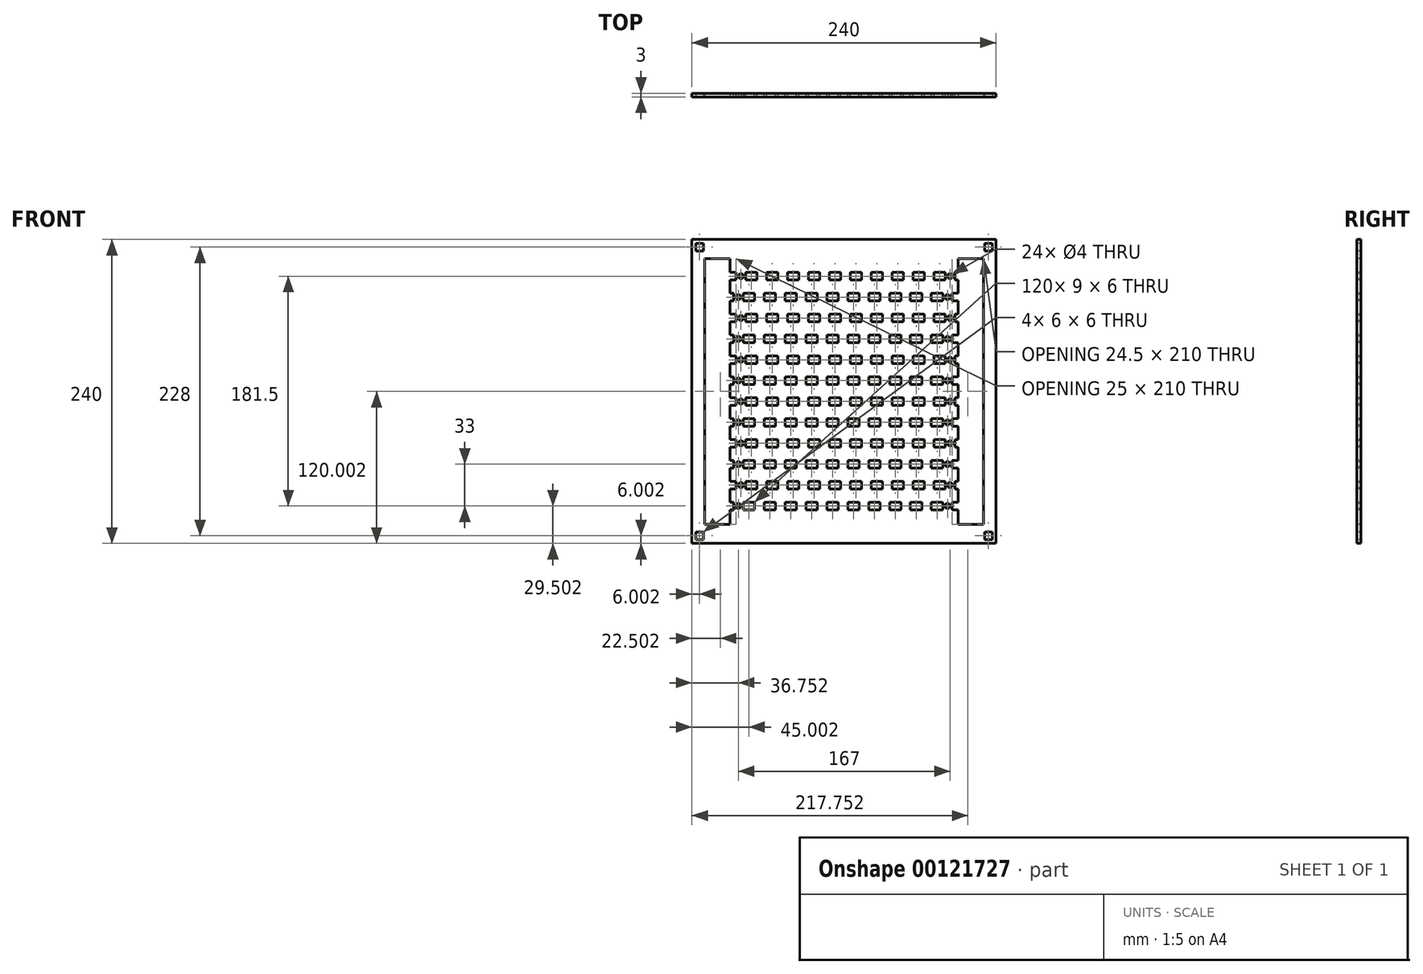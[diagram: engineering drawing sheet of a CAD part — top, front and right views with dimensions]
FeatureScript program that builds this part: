
annotation { "Feature Type Name" : "Feature", "Feature Type Description" : "" }
export const myFeature = defineFeature(function(context is Context, id is Id, definition is map)
    precondition{}
    {
        {
            var Q0;
            Q0=qCreatedBy(makeId("Front.planeOp"),FACE);
            var sketch = newSketch(context, id + "F0", { "sketchPlane" : qUnion([Q0])});
            skLineSegment(sketch, "E0.bottom", {"start": v(-121.79, 157.74) * mm, "end": v(118.21, 157.74) * mm});
            skLineSegment(sketch, "E0.top", {"start": v(-121.79, -82.26) * mm, "end": v(118.21, -82.26) * mm});
            skLineSegment(sketch, "E0.left", {"start": v(-121.79, 157.74) * mm, "end": v(-121.79, -82.26) * mm});
            skLineSegment(sketch, "E0.right", {"start": v(118.21, 157.74) * mm, "end": v(118.21, -82.26) * mm});
            skLineSegment(sketch, "E1.bottom", {"start": v(-95.79, 131.74) * mm, "end": v(-86.79, 131.74) * mm});
            skLineSegment(sketch, "E1.top", {"start": v(-95.79, 125.74) * mm, "end": v(-86.79, 125.74) * mm});
            skLineSegment(sketch, "E1.left", {"start": v(-95.79, 131.74) * mm, "end": v(-95.79, 125.74) * mm});
            skLineSegment(sketch, "E1.right", {"start": v(-86.79, 131.74) * mm, "end": v(-86.79, 125.74) * mm});
            skLineSegment(sketch, "E2.direction1", {"start": v(-95.79, 125.74) * mm, "end": v(-85.79, 125.74) * mm, "construction": true});
            skLineSegment(sketch, "E3.direction1", {"start": v(-95.79, 125.74) * mm, "end": v(-79.29, 125.74) * mm, "construction": true});
            skLineSegment(sketch, "E3.direction2", {"start": v(-95.79, 125.74) * mm, "end": v(-95.79, 92.74) * mm, "construction": true});
            skLineSegment(sketch, "E4.0.1.0", {"start": v(-79.29, 125.74) * mm, "end": v(-69.29, 125.74) * mm, "construction": true});
            skLineSegment(sketch, "E4.3.1.0", {"start": v(-70.29, 131.74) * mm, "end": v(-70.29, 125.74) * mm});
            skLineSegment(sketch, "E4.6.1.0", {"start": v(-79.29, 131.74) * mm, "end": v(-79.29, 125.74) * mm});
            skLineSegment(sketch, "E4.9.1.0", {"start": v(-79.29, 131.74) * mm, "end": v(-70.29, 131.74) * mm});
            skLineSegment(sketch, "E4.12.1.0", {"start": v(-79.29, 125.74) * mm, "end": v(-70.29, 125.74) * mm});
            skLineSegment(sketch, "E4.0.2.0", {"start": v(-62.79, 125.74) * mm, "end": v(-52.79, 125.74) * mm, "construction": true});
            skLineSegment(sketch, "E4.3.2.0", {"start": v(-53.79, 131.74) * mm, "end": v(-53.79, 125.74) * mm});
            skLineSegment(sketch, "E4.6.2.0", {"start": v(-62.79, 131.74) * mm, "end": v(-62.79, 125.74) * mm});
            skLineSegment(sketch, "E4.9.2.0", {"start": v(-62.79, 131.74) * mm, "end": v(-53.79, 131.74) * mm});
            skLineSegment(sketch, "E4.12.2.0", {"start": v(-62.79, 125.74) * mm, "end": v(-53.79, 125.74) * mm});
            skLineSegment(sketch, "E4.0.3.0", {"start": v(-46.29, 125.74) * mm, "end": v(-36.29, 125.74) * mm, "construction": true});
            skLineSegment(sketch, "E4.3.3.0", {"start": v(-37.29, 131.74) * mm, "end": v(-37.29, 125.74) * mm});
            skLineSegment(sketch, "E4.6.3.0", {"start": v(-46.29, 131.74) * mm, "end": v(-46.29, 125.74) * mm});
            skLineSegment(sketch, "E4.9.3.0", {"start": v(-46.29, 131.74) * mm, "end": v(-37.29, 131.74) * mm});
            skLineSegment(sketch, "E4.12.3.0", {"start": v(-46.29, 125.74) * mm, "end": v(-37.29, 125.74) * mm});
            skLineSegment(sketch, "E4.0.4.0", {"start": v(-29.79, 125.74) * mm, "end": v(-19.79, 125.74) * mm, "construction": true});
            skLineSegment(sketch, "E4.3.4.0", {"start": v(-20.79, 131.74) * mm, "end": v(-20.79, 125.74) * mm});
            skLineSegment(sketch, "E4.6.4.0", {"start": v(-29.79, 131.74) * mm, "end": v(-29.79, 125.74) * mm});
            skLineSegment(sketch, "E4.9.4.0", {"start": v(-29.79, 131.74) * mm, "end": v(-20.79, 131.74) * mm});
            skLineSegment(sketch, "E4.12.4.0", {"start": v(-29.79, 125.74) * mm, "end": v(-20.79, 125.74) * mm});
            skLineSegment(sketch, "E4.0.5.0", {"start": v(-13.29, 125.74) * mm, "end": v(-3.29, 125.74) * mm, "construction": true});
            skLineSegment(sketch, "E4.3.5.0", {"start": v(-4.29, 131.74) * mm, "end": v(-4.29, 125.74) * mm});
            skLineSegment(sketch, "E4.6.5.0", {"start": v(-13.29, 131.74) * mm, "end": v(-13.29, 125.74) * mm});
            skLineSegment(sketch, "E4.9.5.0", {"start": v(-13.29, 131.74) * mm, "end": v(-4.29, 131.74) * mm});
            skLineSegment(sketch, "E4.12.5.0", {"start": v(-13.29, 125.74) * mm, "end": v(-4.29, 125.74) * mm});
            skLineSegment(sketch, "E4.0.6.0", {"start": v(3.21, 125.74) * mm, "end": v(13.21, 125.74) * mm, "construction": true});
            skLineSegment(sketch, "E4.3.6.0", {"start": v(12.21, 131.74) * mm, "end": v(12.21, 125.74) * mm});
            skLineSegment(sketch, "E4.6.6.0", {"start": v(3.21, 131.74) * mm, "end": v(3.21, 125.74) * mm});
            skLineSegment(sketch, "E4.9.6.0", {"start": v(3.21, 131.74) * mm, "end": v(12.21, 131.74) * mm});
            skLineSegment(sketch, "E4.12.6.0", {"start": v(3.21, 125.74) * mm, "end": v(12.21, 125.74) * mm});
            skLineSegment(sketch, "E4.0.7.0", {"start": v(19.71, 125.74) * mm, "end": v(29.71, 125.74) * mm, "construction": true});
            skLineSegment(sketch, "E4.3.7.0", {"start": v(28.71, 131.74) * mm, "end": v(28.71, 125.74) * mm});
            skLineSegment(sketch, "E4.6.7.0", {"start": v(19.71, 131.74) * mm, "end": v(19.71, 125.74) * mm});
            skLineSegment(sketch, "E4.9.7.0", {"start": v(19.71, 131.74) * mm, "end": v(28.71, 131.74) * mm});
            skLineSegment(sketch, "E4.12.7.0", {"start": v(19.71, 125.74) * mm, "end": v(28.71, 125.74) * mm});
            skLineSegment(sketch, "E4.0.8.0", {"start": v(36.21, 125.74) * mm, "end": v(46.21, 125.74) * mm, "construction": true});
            skLineSegment(sketch, "E4.3.8.0", {"start": v(45.21, 131.74) * mm, "end": v(45.21, 125.74) * mm});
            skLineSegment(sketch, "E4.6.8.0", {"start": v(36.21, 131.74) * mm, "end": v(36.21, 125.74) * mm});
            skLineSegment(sketch, "E4.9.8.0", {"start": v(36.21, 131.74) * mm, "end": v(45.21, 131.74) * mm});
            skLineSegment(sketch, "E4.12.8.0", {"start": v(36.21, 125.74) * mm, "end": v(45.21, 125.74) * mm});
            skLineSegment(sketch, "E4.0.9.0", {"start": v(52.71, 125.74) * mm, "end": v(62.71, 125.74) * mm, "construction": true});
            skLineSegment(sketch, "E4.3.9.0", {"start": v(61.71, 131.74) * mm, "end": v(61.71, 125.74) * mm});
            skLineSegment(sketch, "E4.6.9.0", {"start": v(52.71, 131.74) * mm, "end": v(52.71, 125.74) * mm});
            skLineSegment(sketch, "E4.9.9.0", {"start": v(52.71, 131.74) * mm, "end": v(61.71, 131.74) * mm});
            skLineSegment(sketch, "E4.12.9.0", {"start": v(52.71, 125.74) * mm, "end": v(61.71, 125.74) * mm});
            skLineSegment(sketch, "E4.0.10.0", {"start": v(69.21, 125.74) * mm, "end": v(79.21, 125.74) * mm, "construction": true});
            skLineSegment(sketch, "E4.3.10.0", {"start": v(78.21, 131.74) * mm, "end": v(78.21, 125.74) * mm});
            skLineSegment(sketch, "E4.6.10.0", {"start": v(69.21, 131.74) * mm, "end": v(69.21, 125.74) * mm});
            skLineSegment(sketch, "E4.9.10.0", {"start": v(69.21, 131.74) * mm, "end": v(78.21, 131.74) * mm});
            skLineSegment(sketch, "E4.12.10.0", {"start": v(69.21, 125.74) * mm, "end": v(78.21, 125.74) * mm});
            skLineSegment(sketch, "E4.0.11.0", {"start": v(85.71, 125.74) * mm, "end": v(95.71, 125.74) * mm, "construction": true});
            skLineSegment(sketch, "E4.3.11.0", {"start": v(94.71, 131.74) * mm, "end": v(94.71, 125.74) * mm});
            skLineSegment(sketch, "E4.6.11.0", {"start": v(85.71, 131.74) * mm, "end": v(85.71, 125.74) * mm});
            skLineSegment(sketch, "E4.9.11.0", {"start": v(85.71, 131.74) * mm, "end": v(94.71, 131.74) * mm});
            skLineSegment(sketch, "E4.12.11.0", {"start": v(85.71, 125.74) * mm, "end": v(94.71, 125.74) * mm});
            skLineSegment(sketch, "E5.0.0.1", {"start": v(-95.79, 92.74) * mm, "end": v(-85.79, 92.74) * mm, "construction": true});
            skLineSegment(sketch, "E5.3.0.1", {"start": v(-86.79, 98.74) * mm, "end": v(-86.79, 92.74) * mm});
            skLineSegment(sketch, "E5.6.0.1", {"start": v(-95.79, 98.74) * mm, "end": v(-95.79, 92.74) * mm});
            skLineSegment(sketch, "E5.9.0.1", {"start": v(-95.79, 98.74) * mm, "end": v(-86.79, 98.74) * mm});
            skLineSegment(sketch, "E5.12.0.1", {"start": v(-95.79, 92.74) * mm, "end": v(-86.79, 92.74) * mm});
            skLineSegment(sketch, "E5.0.0.2", {"start": v(-95.79, 59.74) * mm, "end": v(-85.79, 59.74) * mm, "construction": true});
            skLineSegment(sketch, "E5.3.0.2", {"start": v(-86.79, 65.74) * mm, "end": v(-86.79, 59.74) * mm});
            skLineSegment(sketch, "E5.6.0.2", {"start": v(-95.79, 65.74) * mm, "end": v(-95.79, 59.74) * mm});
            skLineSegment(sketch, "E5.9.0.2", {"start": v(-95.79, 65.74) * mm, "end": v(-86.79, 65.74) * mm});
            skLineSegment(sketch, "E5.12.0.2", {"start": v(-95.79, 59.74) * mm, "end": v(-86.79, 59.74) * mm});
            skLineSegment(sketch, "E5.0.0.3", {"start": v(-95.79, 26.74) * mm, "end": v(-85.79, 26.74) * mm, "construction": true});
            skLineSegment(sketch, "E5.3.0.3", {"start": v(-86.79, 32.74) * mm, "end": v(-86.79, 26.74) * mm});
            skLineSegment(sketch, "E5.6.0.3", {"start": v(-95.79, 32.74) * mm, "end": v(-95.79, 26.74) * mm});
            skLineSegment(sketch, "E5.9.0.3", {"start": v(-95.79, 32.74) * mm, "end": v(-86.79, 32.74) * mm});
            skLineSegment(sketch, "E5.12.0.3", {"start": v(-95.79, 26.74) * mm, "end": v(-86.79, 26.74) * mm});
            skLineSegment(sketch, "E5.0.0.4", {"start": v(-95.79, -6.26) * mm, "end": v(-85.79, -6.26) * mm, "construction": true});
            skLineSegment(sketch, "E5.3.0.4", {"start": v(-86.79, -0.26) * mm, "end": v(-86.79, -6.26) * mm});
            skLineSegment(sketch, "E5.6.0.4", {"start": v(-95.79, -0.26) * mm, "end": v(-95.79, -6.26) * mm});
            skLineSegment(sketch, "E5.9.0.4", {"start": v(-95.79, -0.26) * mm, "end": v(-86.79, -0.26) * mm});
            skLineSegment(sketch, "E5.12.0.4", {"start": v(-95.79, -6.26) * mm, "end": v(-86.79, -6.26) * mm});
            skLineSegment(sketch, "E5.0.0.5", {"start": v(-95.79, -39.26) * mm, "end": v(-85.79, -39.26) * mm, "construction": true});
            skLineSegment(sketch, "E5.3.0.5", {"start": v(-86.79, -33.26) * mm, "end": v(-86.79, -39.26) * mm});
            skLineSegment(sketch, "E5.6.0.5", {"start": v(-95.79, -33.26) * mm, "end": v(-95.79, -39.26) * mm});
            skLineSegment(sketch, "E5.9.0.5", {"start": v(-95.79, -33.26) * mm, "end": v(-86.79, -33.26) * mm});
            skLineSegment(sketch, "E5.12.0.5", {"start": v(-95.79, -39.26) * mm, "end": v(-86.79, -39.26) * mm});
            skLineSegment(sketch, "E5.0.1.1", {"start": v(-79.29, 92.74) * mm, "end": v(-69.29, 92.74) * mm, "construction": true});
            skLineSegment(sketch, "E5.3.1.1", {"start": v(-70.29, 98.74) * mm, "end": v(-70.29, 92.74) * mm});
            skLineSegment(sketch, "E5.6.1.1", {"start": v(-79.29, 98.74) * mm, "end": v(-79.29, 92.74) * mm});
            skLineSegment(sketch, "E5.9.1.1", {"start": v(-79.29, 98.74) * mm, "end": v(-70.29, 98.74) * mm});
            skLineSegment(sketch, "E5.12.1.1", {"start": v(-79.29, 92.74) * mm, "end": v(-70.29, 92.74) * mm});
            skLineSegment(sketch, "E5.0.1.2", {"start": v(-79.29, 59.74) * mm, "end": v(-69.29, 59.74) * mm, "construction": true});
            skLineSegment(sketch, "E5.3.1.2", {"start": v(-70.29, 65.74) * mm, "end": v(-70.29, 59.74) * mm});
            skLineSegment(sketch, "E5.6.1.2", {"start": v(-79.29, 65.74) * mm, "end": v(-79.29, 59.74) * mm});
            skLineSegment(sketch, "E5.9.1.2", {"start": v(-79.29, 65.74) * mm, "end": v(-70.29, 65.74) * mm});
            skLineSegment(sketch, "E5.12.1.2", {"start": v(-79.29, 59.74) * mm, "end": v(-70.29, 59.74) * mm});
            skLineSegment(sketch, "E5.0.1.3", {"start": v(-79.29, 26.74) * mm, "end": v(-69.29, 26.74) * mm, "construction": true});
            skLineSegment(sketch, "E5.3.1.3", {"start": v(-70.29, 32.74) * mm, "end": v(-70.29, 26.74) * mm});
            skLineSegment(sketch, "E5.6.1.3", {"start": v(-79.29, 32.74) * mm, "end": v(-79.29, 26.74) * mm});
            skLineSegment(sketch, "E5.9.1.3", {"start": v(-79.29, 32.74) * mm, "end": v(-70.29, 32.74) * mm});
            skLineSegment(sketch, "E5.12.1.3", {"start": v(-79.29, 26.74) * mm, "end": v(-70.29, 26.74) * mm});
            skLineSegment(sketch, "E5.0.1.4", {"start": v(-79.29, -6.26) * mm, "end": v(-69.29, -6.26) * mm, "construction": true});
            skLineSegment(sketch, "E5.3.1.4", {"start": v(-70.29, -0.26) * mm, "end": v(-70.29, -6.26) * mm});
            skLineSegment(sketch, "E5.6.1.4", {"start": v(-79.29, -0.26) * mm, "end": v(-79.29, -6.26) * mm});
            skLineSegment(sketch, "E5.9.1.4", {"start": v(-79.29, -0.26) * mm, "end": v(-70.29, -0.26) * mm});
            skLineSegment(sketch, "E5.12.1.4", {"start": v(-79.29, -6.26) * mm, "end": v(-70.29, -6.26) * mm});
            skLineSegment(sketch, "E5.0.1.5", {"start": v(-79.29, -39.26) * mm, "end": v(-69.29, -39.26) * mm, "construction": true});
            skLineSegment(sketch, "E5.3.1.5", {"start": v(-70.29, -33.26) * mm, "end": v(-70.29, -39.26) * mm});
            skLineSegment(sketch, "E5.6.1.5", {"start": v(-79.29, -33.26) * mm, "end": v(-79.29, -39.26) * mm});
            skLineSegment(sketch, "E5.9.1.5", {"start": v(-79.29, -33.26) * mm, "end": v(-70.29, -33.26) * mm});
            skLineSegment(sketch, "E5.12.1.5", {"start": v(-79.29, -39.26) * mm, "end": v(-70.29, -39.26) * mm});
            skLineSegment(sketch, "E5.0.2.1", {"start": v(-62.79, 92.74) * mm, "end": v(-52.79, 92.74) * mm, "construction": true});
            skLineSegment(sketch, "E5.3.2.1", {"start": v(-53.79, 98.74) * mm, "end": v(-53.79, 92.74) * mm});
            skLineSegment(sketch, "E5.6.2.1", {"start": v(-62.79, 98.74) * mm, "end": v(-62.79, 92.74) * mm});
            skLineSegment(sketch, "E5.9.2.1", {"start": v(-62.79, 98.74) * mm, "end": v(-53.79, 98.74) * mm});
            skLineSegment(sketch, "E5.12.2.1", {"start": v(-62.79, 92.74) * mm, "end": v(-53.79, 92.74) * mm});
            skLineSegment(sketch, "E5.0.2.2", {"start": v(-62.79, 59.74) * mm, "end": v(-52.79, 59.74) * mm, "construction": true});
            skLineSegment(sketch, "E5.3.2.2", {"start": v(-53.79, 65.74) * mm, "end": v(-53.79, 59.74) * mm});
            skLineSegment(sketch, "E5.6.2.2", {"start": v(-62.79, 65.74) * mm, "end": v(-62.79, 59.74) * mm});
            skLineSegment(sketch, "E5.9.2.2", {"start": v(-62.79, 65.74) * mm, "end": v(-53.79, 65.74) * mm});
            skLineSegment(sketch, "E5.12.2.2", {"start": v(-62.79, 59.74) * mm, "end": v(-53.79, 59.74) * mm});
            skLineSegment(sketch, "E5.0.2.3", {"start": v(-62.79, 26.74) * mm, "end": v(-52.79, 26.74) * mm, "construction": true});
            skLineSegment(sketch, "E5.3.2.3", {"start": v(-53.79, 32.74) * mm, "end": v(-53.79, 26.74) * mm});
            skLineSegment(sketch, "E5.6.2.3", {"start": v(-62.79, 32.74) * mm, "end": v(-62.79, 26.74) * mm});
            skLineSegment(sketch, "E5.9.2.3", {"start": v(-62.79, 32.74) * mm, "end": v(-53.79, 32.74) * mm});
            skLineSegment(sketch, "E5.12.2.3", {"start": v(-62.79, 26.74) * mm, "end": v(-53.79, 26.74) * mm});
            skLineSegment(sketch, "E5.0.2.4", {"start": v(-62.79, -6.26) * mm, "end": v(-52.79, -6.26) * mm, "construction": true});
            skLineSegment(sketch, "E5.3.2.4", {"start": v(-53.79, -0.26) * mm, "end": v(-53.79, -6.26) * mm});
            skLineSegment(sketch, "E5.6.2.4", {"start": v(-62.79, -0.26) * mm, "end": v(-62.79, -6.26) * mm});
            skLineSegment(sketch, "E5.9.2.4", {"start": v(-62.79, -0.26) * mm, "end": v(-53.79, -0.26) * mm});
            skLineSegment(sketch, "E5.12.2.4", {"start": v(-62.79, -6.26) * mm, "end": v(-53.79, -6.26) * mm});
            skLineSegment(sketch, "E5.0.2.5", {"start": v(-62.79, -39.26) * mm, "end": v(-52.79, -39.26) * mm, "construction": true});
            skLineSegment(sketch, "E5.3.2.5", {"start": v(-53.79, -33.26) * mm, "end": v(-53.79, -39.26) * mm});
            skLineSegment(sketch, "E5.6.2.5", {"start": v(-62.79, -33.26) * mm, "end": v(-62.79, -39.26) * mm});
            skLineSegment(sketch, "E5.9.2.5", {"start": v(-62.79, -33.26) * mm, "end": v(-53.79, -33.26) * mm});
            skLineSegment(sketch, "E5.12.2.5", {"start": v(-62.79, -39.26) * mm, "end": v(-53.79, -39.26) * mm});
            skLineSegment(sketch, "E5.0.3.1", {"start": v(-46.29, 92.74) * mm, "end": v(-36.29, 92.74) * mm, "construction": true});
            skLineSegment(sketch, "E5.3.3.1", {"start": v(-37.29, 98.74) * mm, "end": v(-37.29, 92.74) * mm});
            skLineSegment(sketch, "E5.6.3.1", {"start": v(-46.29, 98.74) * mm, "end": v(-46.29, 92.74) * mm});
            skLineSegment(sketch, "E5.9.3.1", {"start": v(-46.29, 98.74) * mm, "end": v(-37.29, 98.74) * mm});
            skLineSegment(sketch, "E5.12.3.1", {"start": v(-46.29, 92.74) * mm, "end": v(-37.29, 92.74) * mm});
            skLineSegment(sketch, "E5.0.3.2", {"start": v(-46.29, 59.74) * mm, "end": v(-36.29, 59.74) * mm, "construction": true});
            skLineSegment(sketch, "E5.3.3.2", {"start": v(-37.29, 65.74) * mm, "end": v(-37.29, 59.74) * mm});
            skLineSegment(sketch, "E5.6.3.2", {"start": v(-46.29, 65.74) * mm, "end": v(-46.29, 59.74) * mm});
            skLineSegment(sketch, "E5.9.3.2", {"start": v(-46.29, 65.74) * mm, "end": v(-37.29, 65.74) * mm});
            skLineSegment(sketch, "E5.12.3.2", {"start": v(-46.29, 59.74) * mm, "end": v(-37.29, 59.74) * mm});
            skLineSegment(sketch, "E5.0.3.3", {"start": v(-46.29, 26.74) * mm, "end": v(-36.29, 26.74) * mm, "construction": true});
            skLineSegment(sketch, "E5.3.3.3", {"start": v(-37.29, 32.74) * mm, "end": v(-37.29, 26.74) * mm});
            skLineSegment(sketch, "E5.6.3.3", {"start": v(-46.29, 32.74) * mm, "end": v(-46.29, 26.74) * mm});
            skLineSegment(sketch, "E5.9.3.3", {"start": v(-46.29, 32.74) * mm, "end": v(-37.29, 32.74) * mm});
            skLineSegment(sketch, "E5.12.3.3", {"start": v(-46.29, 26.74) * mm, "end": v(-37.29, 26.74) * mm});
            skLineSegment(sketch, "E5.0.3.4", {"start": v(-46.29, -6.26) * mm, "end": v(-36.29, -6.26) * mm, "construction": true});
            skLineSegment(sketch, "E5.3.3.4", {"start": v(-37.29, -0.26) * mm, "end": v(-37.29, -6.26) * mm});
            skLineSegment(sketch, "E5.6.3.4", {"start": v(-46.29, -0.26) * mm, "end": v(-46.29, -6.26) * mm});
            skLineSegment(sketch, "E5.9.3.4", {"start": v(-46.29, -0.26) * mm, "end": v(-37.29, -0.26) * mm});
            skLineSegment(sketch, "E5.12.3.4", {"start": v(-46.29, -6.26) * mm, "end": v(-37.29, -6.26) * mm});
            skLineSegment(sketch, "E5.0.3.5", {"start": v(-46.29, -39.26) * mm, "end": v(-36.29, -39.26) * mm, "construction": true});
            skLineSegment(sketch, "E5.3.3.5", {"start": v(-37.29, -33.26) * mm, "end": v(-37.29, -39.26) * mm});
            skLineSegment(sketch, "E5.6.3.5", {"start": v(-46.29, -33.26) * mm, "end": v(-46.29, -39.26) * mm});
            skLineSegment(sketch, "E5.9.3.5", {"start": v(-46.29, -33.26) * mm, "end": v(-37.29, -33.26) * mm});
            skLineSegment(sketch, "E5.12.3.5", {"start": v(-46.29, -39.26) * mm, "end": v(-37.29, -39.26) * mm});
            skLineSegment(sketch, "E5.0.4.1", {"start": v(-29.79, 92.74) * mm, "end": v(-19.79, 92.74) * mm, "construction": true});
            skLineSegment(sketch, "E5.3.4.1", {"start": v(-20.79, 98.74) * mm, "end": v(-20.79, 92.74) * mm});
            skLineSegment(sketch, "E5.6.4.1", {"start": v(-29.79, 98.74) * mm, "end": v(-29.79, 92.74) * mm});
            skLineSegment(sketch, "E5.9.4.1", {"start": v(-29.79, 98.74) * mm, "end": v(-20.79, 98.74) * mm});
            skLineSegment(sketch, "E5.12.4.1", {"start": v(-29.79, 92.74) * mm, "end": v(-20.79, 92.74) * mm});
            skLineSegment(sketch, "E5.0.4.2", {"start": v(-29.79, 59.74) * mm, "end": v(-19.79, 59.74) * mm, "construction": true});
            skLineSegment(sketch, "E5.3.4.2", {"start": v(-20.79, 65.74) * mm, "end": v(-20.79, 59.74) * mm});
            skLineSegment(sketch, "E5.6.4.2", {"start": v(-29.79, 65.74) * mm, "end": v(-29.79, 59.74) * mm});
            skLineSegment(sketch, "E5.9.4.2", {"start": v(-29.79, 65.74) * mm, "end": v(-20.79, 65.74) * mm});
            skLineSegment(sketch, "E5.12.4.2", {"start": v(-29.79, 59.74) * mm, "end": v(-20.79, 59.74) * mm});
            skLineSegment(sketch, "E5.0.4.3", {"start": v(-29.79, 26.74) * mm, "end": v(-19.79, 26.74) * mm, "construction": true});
            skLineSegment(sketch, "E5.3.4.3", {"start": v(-20.79, 32.74) * mm, "end": v(-20.79, 26.74) * mm});
            skLineSegment(sketch, "E5.6.4.3", {"start": v(-29.79, 32.74) * mm, "end": v(-29.79, 26.74) * mm});
            skLineSegment(sketch, "E5.9.4.3", {"start": v(-29.79, 32.74) * mm, "end": v(-20.79, 32.74) * mm});
            skLineSegment(sketch, "E5.12.4.3", {"start": v(-29.79, 26.74) * mm, "end": v(-20.79, 26.74) * mm});
            skLineSegment(sketch, "E5.0.4.4", {"start": v(-29.79, -6.26) * mm, "end": v(-19.79, -6.26) * mm, "construction": true});
            skLineSegment(sketch, "E5.3.4.4", {"start": v(-20.79, -0.26) * mm, "end": v(-20.79, -6.26) * mm});
            skLineSegment(sketch, "E5.6.4.4", {"start": v(-29.79, -0.26) * mm, "end": v(-29.79, -6.26) * mm});
            skLineSegment(sketch, "E5.9.4.4", {"start": v(-29.79, -0.26) * mm, "end": v(-20.79, -0.26) * mm});
            skLineSegment(sketch, "E5.12.4.4", {"start": v(-29.79, -6.26) * mm, "end": v(-20.79, -6.26) * mm});
            skLineSegment(sketch, "E5.0.4.5", {"start": v(-29.79, -39.26) * mm, "end": v(-19.79, -39.26) * mm, "construction": true});
            skLineSegment(sketch, "E5.3.4.5", {"start": v(-20.79, -33.26) * mm, "end": v(-20.79, -39.26) * mm});
            skLineSegment(sketch, "E5.6.4.5", {"start": v(-29.79, -33.26) * mm, "end": v(-29.79, -39.26) * mm});
            skLineSegment(sketch, "E5.9.4.5", {"start": v(-29.79, -33.26) * mm, "end": v(-20.79, -33.26) * mm});
            skLineSegment(sketch, "E5.12.4.5", {"start": v(-29.79, -39.26) * mm, "end": v(-20.79, -39.26) * mm});
            skLineSegment(sketch, "E5.0.5.1", {"start": v(-13.29, 92.74) * mm, "end": v(-3.29, 92.74) * mm, "construction": true});
            skLineSegment(sketch, "E5.3.5.1", {"start": v(-4.29, 98.74) * mm, "end": v(-4.29, 92.74) * mm});
            skLineSegment(sketch, "E5.6.5.1", {"start": v(-13.29, 98.74) * mm, "end": v(-13.29, 92.74) * mm});
            skLineSegment(sketch, "E5.9.5.1", {"start": v(-13.29, 98.74) * mm, "end": v(-4.29, 98.74) * mm});
            skLineSegment(sketch, "E5.12.5.1", {"start": v(-13.29, 92.74) * mm, "end": v(-4.29, 92.74) * mm});
            skLineSegment(sketch, "E5.0.5.2", {"start": v(-13.29, 59.74) * mm, "end": v(-3.29, 59.74) * mm, "construction": true});
            skLineSegment(sketch, "E5.3.5.2", {"start": v(-4.29, 65.74) * mm, "end": v(-4.29, 59.74) * mm});
            skLineSegment(sketch, "E5.6.5.2", {"start": v(-13.29, 65.74) * mm, "end": v(-13.29, 59.74) * mm});
            skLineSegment(sketch, "E5.9.5.2", {"start": v(-13.29, 65.74) * mm, "end": v(-4.29, 65.74) * mm});
            skLineSegment(sketch, "E5.12.5.2", {"start": v(-13.29, 59.74) * mm, "end": v(-4.29, 59.74) * mm});
            skLineSegment(sketch, "E5.0.5.3", {"start": v(-13.29, 26.74) * mm, "end": v(-3.29, 26.74) * mm, "construction": true});
            skLineSegment(sketch, "E5.3.5.3", {"start": v(-4.29, 32.74) * mm, "end": v(-4.29, 26.74) * mm});
            skLineSegment(sketch, "E5.6.5.3", {"start": v(-13.29, 32.74) * mm, "end": v(-13.29, 26.74) * mm});
            skLineSegment(sketch, "E5.9.5.3", {"start": v(-13.29, 32.74) * mm, "end": v(-4.29, 32.74) * mm});
            skLineSegment(sketch, "E5.12.5.3", {"start": v(-13.29, 26.74) * mm, "end": v(-4.29, 26.74) * mm});
            skLineSegment(sketch, "E5.0.5.4", {"start": v(-13.29, -6.26) * mm, "end": v(-3.29, -6.26) * mm, "construction": true});
            skLineSegment(sketch, "E5.3.5.4", {"start": v(-4.29, -0.26) * mm, "end": v(-4.29, -6.26) * mm});
            skLineSegment(sketch, "E5.6.5.4", {"start": v(-13.29, -0.26) * mm, "end": v(-13.29, -6.26) * mm});
            skLineSegment(sketch, "E5.9.5.4", {"start": v(-13.29, -0.26) * mm, "end": v(-4.29, -0.26) * mm});
            skLineSegment(sketch, "E5.12.5.4", {"start": v(-13.29, -6.26) * mm, "end": v(-4.29, -6.26) * mm});
            skLineSegment(sketch, "E5.0.5.5", {"start": v(-13.29, -39.26) * mm, "end": v(-3.29, -39.26) * mm, "construction": true});
            skLineSegment(sketch, "E5.3.5.5", {"start": v(-4.29, -33.26) * mm, "end": v(-4.29, -39.26) * mm});
            skLineSegment(sketch, "E5.6.5.5", {"start": v(-13.29, -33.26) * mm, "end": v(-13.29, -39.26) * mm});
            skLineSegment(sketch, "E5.9.5.5", {"start": v(-13.29, -33.26) * mm, "end": v(-4.29, -33.26) * mm});
            skLineSegment(sketch, "E5.12.5.5", {"start": v(-13.29, -39.26) * mm, "end": v(-4.29, -39.26) * mm});
            skLineSegment(sketch, "E5.0.6.1", {"start": v(3.21, 92.74) * mm, "end": v(13.21, 92.74) * mm, "construction": true});
            skLineSegment(sketch, "E5.3.6.1", {"start": v(12.21, 98.74) * mm, "end": v(12.21, 92.74) * mm});
            skLineSegment(sketch, "E5.6.6.1", {"start": v(3.21, 98.74) * mm, "end": v(3.21, 92.74) * mm});
            skLineSegment(sketch, "E5.9.6.1", {"start": v(3.21, 98.74) * mm, "end": v(12.21, 98.74) * mm});
            skLineSegment(sketch, "E5.12.6.1", {"start": v(3.21, 92.74) * mm, "end": v(12.21, 92.74) * mm});
            skLineSegment(sketch, "E5.0.6.2", {"start": v(3.21, 59.74) * mm, "end": v(13.21, 59.74) * mm, "construction": true});
            skLineSegment(sketch, "E5.3.6.2", {"start": v(12.21, 65.74) * mm, "end": v(12.21, 59.74) * mm});
            skLineSegment(sketch, "E5.6.6.2", {"start": v(3.21, 65.74) * mm, "end": v(3.21, 59.74) * mm});
            skLineSegment(sketch, "E5.9.6.2", {"start": v(3.21, 65.74) * mm, "end": v(12.21, 65.74) * mm});
            skLineSegment(sketch, "E5.12.6.2", {"start": v(3.21, 59.74) * mm, "end": v(12.21, 59.74) * mm});
            skLineSegment(sketch, "E5.0.6.3", {"start": v(3.21, 26.74) * mm, "end": v(13.21, 26.74) * mm, "construction": true});
            skLineSegment(sketch, "E5.3.6.3", {"start": v(12.21, 32.74) * mm, "end": v(12.21, 26.74) * mm});
            skLineSegment(sketch, "E5.6.6.3", {"start": v(3.21, 32.74) * mm, "end": v(3.21, 26.74) * mm});
            skLineSegment(sketch, "E5.9.6.3", {"start": v(3.21, 32.74) * mm, "end": v(12.21, 32.74) * mm});
            skLineSegment(sketch, "E5.12.6.3", {"start": v(3.21, 26.74) * mm, "end": v(12.21, 26.74) * mm});
            skLineSegment(sketch, "E5.0.6.4", {"start": v(3.21, -6.26) * mm, "end": v(13.21, -6.26) * mm, "construction": true});
            skLineSegment(sketch, "E5.3.6.4", {"start": v(12.21, -0.26) * mm, "end": v(12.21, -6.26) * mm});
            skLineSegment(sketch, "E5.6.6.4", {"start": v(3.21, -0.26) * mm, "end": v(3.21, -6.26) * mm});
            skLineSegment(sketch, "E5.9.6.4", {"start": v(3.21, -0.26) * mm, "end": v(12.21, -0.26) * mm});
            skLineSegment(sketch, "E5.12.6.4", {"start": v(3.21, -6.26) * mm, "end": v(12.21, -6.26) * mm});
            skLineSegment(sketch, "E5.0.6.5", {"start": v(3.21, -39.26) * mm, "end": v(13.21, -39.26) * mm, "construction": true});
            skLineSegment(sketch, "E5.3.6.5", {"start": v(12.21, -33.26) * mm, "end": v(12.21, -39.26) * mm});
            skLineSegment(sketch, "E5.6.6.5", {"start": v(3.21, -33.26) * mm, "end": v(3.21, -39.26) * mm});
            skLineSegment(sketch, "E5.9.6.5", {"start": v(3.21, -33.26) * mm, "end": v(12.21, -33.26) * mm});
            skLineSegment(sketch, "E5.12.6.5", {"start": v(3.21, -39.26) * mm, "end": v(12.21, -39.26) * mm});
            skLineSegment(sketch, "E5.0.7.1", {"start": v(19.71, 92.74) * mm, "end": v(29.71, 92.74) * mm, "construction": true});
            skLineSegment(sketch, "E5.3.7.1", {"start": v(28.71, 98.74) * mm, "end": v(28.71, 92.74) * mm});
            skLineSegment(sketch, "E5.6.7.1", {"start": v(19.71, 98.74) * mm, "end": v(19.71, 92.74) * mm});
            skLineSegment(sketch, "E5.9.7.1", {"start": v(19.71, 98.74) * mm, "end": v(28.71, 98.74) * mm});
            skLineSegment(sketch, "E5.12.7.1", {"start": v(19.71, 92.74) * mm, "end": v(28.71, 92.74) * mm});
            skLineSegment(sketch, "E5.0.7.2", {"start": v(19.71, 59.74) * mm, "end": v(29.71, 59.74) * mm, "construction": true});
            skLineSegment(sketch, "E5.3.7.2", {"start": v(28.71, 65.74) * mm, "end": v(28.71, 59.74) * mm});
            skLineSegment(sketch, "E5.6.7.2", {"start": v(19.71, 65.74) * mm, "end": v(19.71, 59.74) * mm});
            skLineSegment(sketch, "E5.9.7.2", {"start": v(19.71, 65.74) * mm, "end": v(28.71, 65.74) * mm});
            skLineSegment(sketch, "E5.12.7.2", {"start": v(19.71, 59.74) * mm, "end": v(28.71, 59.74) * mm});
            skLineSegment(sketch, "E5.0.7.3", {"start": v(19.71, 26.74) * mm, "end": v(29.71, 26.74) * mm, "construction": true});
            skLineSegment(sketch, "E5.3.7.3", {"start": v(28.71, 32.74) * mm, "end": v(28.71, 26.74) * mm});
            skLineSegment(sketch, "E5.6.7.3", {"start": v(19.71, 32.74) * mm, "end": v(19.71, 26.74) * mm});
            skLineSegment(sketch, "E5.9.7.3", {"start": v(19.71, 32.74) * mm, "end": v(28.71, 32.74) * mm});
            skLineSegment(sketch, "E5.12.7.3", {"start": v(19.71, 26.74) * mm, "end": v(28.71, 26.74) * mm});
            skLineSegment(sketch, "E5.0.7.4", {"start": v(19.71, -6.26) * mm, "end": v(29.71, -6.26) * mm, "construction": true});
            skLineSegment(sketch, "E5.3.7.4", {"start": v(28.71, -0.26) * mm, "end": v(28.71, -6.26) * mm});
            skLineSegment(sketch, "E5.6.7.4", {"start": v(19.71, -0.26) * mm, "end": v(19.71, -6.26) * mm});
            skLineSegment(sketch, "E5.9.7.4", {"start": v(19.71, -0.26) * mm, "end": v(28.71, -0.26) * mm});
            skLineSegment(sketch, "E5.12.7.4", {"start": v(19.71, -6.26) * mm, "end": v(28.71, -6.26) * mm});
            skLineSegment(sketch, "E5.0.7.5", {"start": v(19.71, -39.26) * mm, "end": v(29.71, -39.26) * mm, "construction": true});
            skLineSegment(sketch, "E5.3.7.5", {"start": v(28.71, -33.26) * mm, "end": v(28.71, -39.26) * mm});
            skLineSegment(sketch, "E5.6.7.5", {"start": v(19.71, -33.26) * mm, "end": v(19.71, -39.26) * mm});
            skLineSegment(sketch, "E5.9.7.5", {"start": v(19.71, -33.26) * mm, "end": v(28.71, -33.26) * mm});
            skLineSegment(sketch, "E5.12.7.5", {"start": v(19.71, -39.26) * mm, "end": v(28.71, -39.26) * mm});
            skLineSegment(sketch, "E5.0.8.1", {"start": v(36.21, 92.74) * mm, "end": v(46.21, 92.74) * mm, "construction": true});
            skLineSegment(sketch, "E5.3.8.1", {"start": v(45.21, 98.74) * mm, "end": v(45.21, 92.74) * mm});
            skLineSegment(sketch, "E5.6.8.1", {"start": v(36.21, 98.74) * mm, "end": v(36.21, 92.74) * mm});
            skLineSegment(sketch, "E5.9.8.1", {"start": v(36.21, 98.74) * mm, "end": v(45.21, 98.74) * mm});
            skLineSegment(sketch, "E5.12.8.1", {"start": v(36.21, 92.74) * mm, "end": v(45.21, 92.74) * mm});
            skLineSegment(sketch, "E5.0.8.2", {"start": v(36.21, 59.74) * mm, "end": v(46.21, 59.74) * mm, "construction": true});
            skLineSegment(sketch, "E5.3.8.2", {"start": v(45.21, 65.74) * mm, "end": v(45.21, 59.74) * mm});
            skLineSegment(sketch, "E5.6.8.2", {"start": v(36.21, 65.74) * mm, "end": v(36.21, 59.74) * mm});
            skLineSegment(sketch, "E5.9.8.2", {"start": v(36.21, 65.74) * mm, "end": v(45.21, 65.74) * mm});
            skLineSegment(sketch, "E5.12.8.2", {"start": v(36.21, 59.74) * mm, "end": v(45.21, 59.74) * mm});
            skLineSegment(sketch, "E5.0.8.3", {"start": v(36.21, 26.74) * mm, "end": v(46.21, 26.74) * mm, "construction": true});
            skLineSegment(sketch, "E5.3.8.3", {"start": v(45.21, 32.74) * mm, "end": v(45.21, 26.74) * mm});
            skLineSegment(sketch, "E5.6.8.3", {"start": v(36.21, 32.74) * mm, "end": v(36.21, 26.74) * mm});
            skLineSegment(sketch, "E5.9.8.3", {"start": v(36.21, 32.74) * mm, "end": v(45.21, 32.74) * mm});
            skLineSegment(sketch, "E5.12.8.3", {"start": v(36.21, 26.74) * mm, "end": v(45.21, 26.74) * mm});
            skLineSegment(sketch, "E5.0.8.4", {"start": v(36.21, -6.26) * mm, "end": v(46.21, -6.26) * mm, "construction": true});
            skLineSegment(sketch, "E5.3.8.4", {"start": v(45.21, -0.26) * mm, "end": v(45.21, -6.26) * mm});
            skLineSegment(sketch, "E5.6.8.4", {"start": v(36.21, -0.26) * mm, "end": v(36.21, -6.26) * mm});
            skLineSegment(sketch, "E5.9.8.4", {"start": v(36.21, -0.26) * mm, "end": v(45.21, -0.26) * mm});
            skLineSegment(sketch, "E5.12.8.4", {"start": v(36.21, -6.26) * mm, "end": v(45.21, -6.26) * mm});
            skLineSegment(sketch, "E5.0.8.5", {"start": v(36.21, -39.26) * mm, "end": v(46.21, -39.26) * mm, "construction": true});
            skLineSegment(sketch, "E5.3.8.5", {"start": v(45.21, -33.26) * mm, "end": v(45.21, -39.26) * mm});
            skLineSegment(sketch, "E5.6.8.5", {"start": v(36.21, -33.26) * mm, "end": v(36.21, -39.26) * mm});
            skLineSegment(sketch, "E5.9.8.5", {"start": v(36.21, -33.26) * mm, "end": v(45.21, -33.26) * mm});
            skLineSegment(sketch, "E5.12.8.5", {"start": v(36.21, -39.26) * mm, "end": v(45.21, -39.26) * mm});
            skLineSegment(sketch, "E5.0.9.1", {"start": v(52.71, 92.74) * mm, "end": v(62.71, 92.74) * mm, "construction": true});
            skLineSegment(sketch, "E5.3.9.1", {"start": v(61.71, 98.74) * mm, "end": v(61.71, 92.74) * mm});
            skLineSegment(sketch, "E5.6.9.1", {"start": v(52.71, 98.74) * mm, "end": v(52.71, 92.74) * mm});
            skLineSegment(sketch, "E5.9.9.1", {"start": v(52.71, 98.74) * mm, "end": v(61.71, 98.74) * mm});
            skLineSegment(sketch, "E5.12.9.1", {"start": v(52.71, 92.74) * mm, "end": v(61.71, 92.74) * mm});
            skLineSegment(sketch, "E5.0.9.2", {"start": v(52.71, 59.74) * mm, "end": v(62.71, 59.74) * mm, "construction": true});
            skLineSegment(sketch, "E5.3.9.2", {"start": v(61.71, 65.74) * mm, "end": v(61.71, 59.74) * mm});
            skLineSegment(sketch, "E5.6.9.2", {"start": v(52.71, 65.74) * mm, "end": v(52.71, 59.74) * mm});
            skLineSegment(sketch, "E5.9.9.2", {"start": v(52.71, 65.74) * mm, "end": v(61.71, 65.74) * mm});
            skLineSegment(sketch, "E5.12.9.2", {"start": v(52.71, 59.74) * mm, "end": v(61.71, 59.74) * mm});
            skLineSegment(sketch, "E5.0.9.3", {"start": v(52.71, 26.74) * mm, "end": v(62.71, 26.74) * mm, "construction": true});
            skLineSegment(sketch, "E5.3.9.3", {"start": v(61.71, 32.74) * mm, "end": v(61.71, 26.74) * mm});
            skLineSegment(sketch, "E5.6.9.3", {"start": v(52.71, 32.74) * mm, "end": v(52.71, 26.74) * mm});
            skLineSegment(sketch, "E5.9.9.3", {"start": v(52.71, 32.74) * mm, "end": v(61.71, 32.74) * mm});
            skLineSegment(sketch, "E5.12.9.3", {"start": v(52.71, 26.74) * mm, "end": v(61.71, 26.74) * mm});
            skLineSegment(sketch, "E5.0.9.4", {"start": v(52.71, -6.26) * mm, "end": v(62.71, -6.26) * mm, "construction": true});
            skLineSegment(sketch, "E5.3.9.4", {"start": v(61.71, -0.26) * mm, "end": v(61.71, -6.26) * mm});
            skLineSegment(sketch, "E5.6.9.4", {"start": v(52.71, -0.26) * mm, "end": v(52.71, -6.26) * mm});
            skLineSegment(sketch, "E5.9.9.4", {"start": v(52.71, -0.26) * mm, "end": v(61.71, -0.26) * mm});
            skLineSegment(sketch, "E5.12.9.4", {"start": v(52.71, -6.26) * mm, "end": v(61.71, -6.26) * mm});
            skLineSegment(sketch, "E5.0.9.5", {"start": v(52.71, -39.26) * mm, "end": v(62.71, -39.26) * mm, "construction": true});
            skLineSegment(sketch, "E5.3.9.5", {"start": v(61.71, -33.26) * mm, "end": v(61.71, -39.26) * mm});
            skLineSegment(sketch, "E5.6.9.5", {"start": v(52.71, -33.26) * mm, "end": v(52.71, -39.26) * mm});
            skLineSegment(sketch, "E5.9.9.5", {"start": v(52.71, -33.26) * mm, "end": v(61.71, -33.26) * mm});
            skLineSegment(sketch, "E5.12.9.5", {"start": v(52.71, -39.26) * mm, "end": v(61.71, -39.26) * mm});
            skLineSegment(sketch, "E5.0.10.1", {"start": v(69.21, 92.74) * mm, "end": v(79.21, 92.74) * mm, "construction": true});
            skLineSegment(sketch, "E5.3.10.1", {"start": v(78.21, 98.74) * mm, "end": v(78.21, 92.74) * mm});
            skLineSegment(sketch, "E5.6.10.1", {"start": v(69.21, 98.74) * mm, "end": v(69.21, 92.74) * mm});
            skLineSegment(sketch, "E5.9.10.1", {"start": v(69.21, 98.74) * mm, "end": v(78.21, 98.74) * mm});
            skLineSegment(sketch, "E5.12.10.1", {"start": v(69.21, 92.74) * mm, "end": v(78.21, 92.74) * mm});
            skLineSegment(sketch, "E5.0.10.2", {"start": v(69.21, 59.74) * mm, "end": v(79.21, 59.74) * mm, "construction": true});
            skLineSegment(sketch, "E5.3.10.2", {"start": v(78.21, 65.74) * mm, "end": v(78.21, 59.74) * mm});
            skLineSegment(sketch, "E5.6.10.2", {"start": v(69.21, 65.74) * mm, "end": v(69.21, 59.74) * mm});
            skLineSegment(sketch, "E5.9.10.2", {"start": v(69.21, 65.74) * mm, "end": v(78.21, 65.74) * mm});
            skLineSegment(sketch, "E5.12.10.2", {"start": v(69.21, 59.74) * mm, "end": v(78.21, 59.74) * mm});
            skLineSegment(sketch, "E5.0.10.3", {"start": v(69.21, 26.74) * mm, "end": v(79.21, 26.74) * mm, "construction": true});
            skLineSegment(sketch, "E5.3.10.3", {"start": v(78.21, 32.74) * mm, "end": v(78.21, 26.74) * mm});
            skLineSegment(sketch, "E5.6.10.3", {"start": v(69.21, 32.74) * mm, "end": v(69.21, 26.74) * mm});
            skLineSegment(sketch, "E5.9.10.3", {"start": v(69.21, 32.74) * mm, "end": v(78.21, 32.74) * mm});
            skLineSegment(sketch, "E5.12.10.3", {"start": v(69.21, 26.74) * mm, "end": v(78.21, 26.74) * mm});
            skLineSegment(sketch, "E5.0.10.4", {"start": v(69.21, -6.26) * mm, "end": v(79.21, -6.26) * mm, "construction": true});
            skLineSegment(sketch, "E5.3.10.4", {"start": v(78.21, -0.26) * mm, "end": v(78.21, -6.26) * mm});
            skLineSegment(sketch, "E5.6.10.4", {"start": v(69.21, -0.26) * mm, "end": v(69.21, -6.26) * mm});
            skLineSegment(sketch, "E5.9.10.4", {"start": v(69.21, -0.26) * mm, "end": v(78.21, -0.26) * mm});
            skLineSegment(sketch, "E5.12.10.4", {"start": v(69.21, -6.26) * mm, "end": v(78.21, -6.26) * mm});
            skLineSegment(sketch, "E5.0.10.5", {"start": v(69.21, -39.26) * mm, "end": v(79.21, -39.26) * mm, "construction": true});
            skLineSegment(sketch, "E5.3.10.5", {"start": v(78.21, -33.26) * mm, "end": v(78.21, -39.26) * mm});
            skLineSegment(sketch, "E5.6.10.5", {"start": v(69.21, -33.26) * mm, "end": v(69.21, -39.26) * mm});
            skLineSegment(sketch, "E5.9.10.5", {"start": v(69.21, -33.26) * mm, "end": v(78.21, -33.26) * mm});
            skLineSegment(sketch, "E5.12.10.5", {"start": v(69.21, -39.26) * mm, "end": v(78.21, -39.26) * mm});
            skLineSegment(sketch, "E5.0.11.1", {"start": v(85.71, 92.74) * mm, "end": v(95.71, 92.74) * mm, "construction": true});
            skLineSegment(sketch, "E5.3.11.1", {"start": v(94.71, 98.74) * mm, "end": v(94.71, 92.74) * mm});
            skLineSegment(sketch, "E5.6.11.1", {"start": v(85.71, 98.74) * mm, "end": v(85.71, 92.74) * mm});
            skLineSegment(sketch, "E5.9.11.1", {"start": v(85.71, 98.74) * mm, "end": v(94.71, 98.74) * mm});
            skLineSegment(sketch, "E5.12.11.1", {"start": v(85.71, 92.74) * mm, "end": v(94.71, 92.74) * mm});
            skLineSegment(sketch, "E5.0.11.2", {"start": v(85.71, 59.74) * mm, "end": v(95.71, 59.74) * mm, "construction": true});
            skLineSegment(sketch, "E5.3.11.2", {"start": v(94.71, 65.74) * mm, "end": v(94.71, 59.74) * mm});
            skLineSegment(sketch, "E5.6.11.2", {"start": v(85.71, 65.74) * mm, "end": v(85.71, 59.74) * mm});
            skLineSegment(sketch, "E5.9.11.2", {"start": v(85.71, 65.74) * mm, "end": v(94.71, 65.74) * mm});
            skLineSegment(sketch, "E5.12.11.2", {"start": v(85.71, 59.74) * mm, "end": v(94.71, 59.74) * mm});
            skLineSegment(sketch, "E5.0.11.3", {"start": v(85.71, 26.74) * mm, "end": v(95.71, 26.74) * mm, "construction": true});
            skLineSegment(sketch, "E5.3.11.3", {"start": v(94.71, 32.74) * mm, "end": v(94.71, 26.74) * mm});
            skLineSegment(sketch, "E5.6.11.3", {"start": v(85.71, 32.74) * mm, "end": v(85.71, 26.74) * mm});
            skLineSegment(sketch, "E5.9.11.3", {"start": v(85.71, 32.74) * mm, "end": v(94.71, 32.74) * mm});
            skLineSegment(sketch, "E5.12.11.3", {"start": v(85.71, 26.74) * mm, "end": v(94.71, 26.74) * mm});
            skLineSegment(sketch, "E5.0.11.4", {"start": v(85.71, -6.26) * mm, "end": v(95.71, -6.26) * mm, "construction": true});
            skLineSegment(sketch, "E5.3.11.4", {"start": v(94.71, -0.26) * mm, "end": v(94.71, -6.26) * mm});
            skLineSegment(sketch, "E5.6.11.4", {"start": v(85.71, -0.26) * mm, "end": v(85.71, -6.26) * mm});
            skLineSegment(sketch, "E5.9.11.4", {"start": v(85.71, -0.26) * mm, "end": v(94.71, -0.26) * mm});
            skLineSegment(sketch, "E5.12.11.4", {"start": v(85.71, -6.26) * mm, "end": v(94.71, -6.26) * mm});
            skLineSegment(sketch, "E5.0.11.5", {"start": v(85.71, -39.26) * mm, "end": v(95.71, -39.26) * mm, "construction": true});
            skLineSegment(sketch, "E5.3.11.5", {"start": v(94.71, -33.26) * mm, "end": v(94.71, -39.26) * mm});
            skLineSegment(sketch, "E5.6.11.5", {"start": v(85.71, -33.26) * mm, "end": v(85.71, -39.26) * mm});
            skLineSegment(sketch, "E5.9.11.5", {"start": v(85.71, -33.26) * mm, "end": v(94.71, -33.26) * mm});
            skLineSegment(sketch, "E5.12.11.5", {"start": v(85.71, -39.26) * mm, "end": v(94.71, -39.26) * mm});
            skLineSegment(sketch, "E6.bottom", {"start": v(-97.79, 115.24) * mm, "end": v(-88.79, 115.24) * mm});
            skLineSegment(sketch, "E6.top", {"start": v(-97.79, 109.24) * mm, "end": v(-88.79, 109.24) * mm});
            skLineSegment(sketch, "E6.left", {"start": v(-97.79, 115.24) * mm, "end": v(-97.79, 109.24) * mm});
            skLineSegment(sketch, "E6.right", {"start": v(-88.79, 115.24) * mm, "end": v(-88.79, 109.24) * mm});
            skLineSegment(sketch, "E7.0.1.0", {"start": v(-97.79, 82.24) * mm, "end": v(-88.79, 82.24) * mm});
            skLineSegment(sketch, "E7.0.1.1", {"start": v(-88.79, 82.24) * mm, "end": v(-88.79, 76.24) * mm});
            skLineSegment(sketch, "E7.0.1.2", {"start": v(-97.79, 76.24) * mm, "end": v(-88.79, 76.24) * mm});
            skLineSegment(sketch, "E7.0.1.3", {"start": v(-97.79, 82.24) * mm, "end": v(-97.79, 76.24) * mm});
            skLineSegment(sketch, "E7.0.2.0", {"start": v(-97.79, 49.24) * mm, "end": v(-88.79, 49.24) * mm});
            skLineSegment(sketch, "E7.0.2.1", {"start": v(-88.79, 49.24) * mm, "end": v(-88.79, 43.24) * mm});
            skLineSegment(sketch, "E7.0.2.2", {"start": v(-97.79, 43.24) * mm, "end": v(-88.79, 43.24) * mm});
            skLineSegment(sketch, "E7.0.2.3", {"start": v(-97.79, 49.24) * mm, "end": v(-97.79, 43.24) * mm});
            skLineSegment(sketch, "E7.0.3.0", {"start": v(-97.79, 16.24) * mm, "end": v(-88.79, 16.24) * mm});
            skLineSegment(sketch, "E7.0.3.1", {"start": v(-88.79, 16.24) * mm, "end": v(-88.79, 10.24) * mm});
            skLineSegment(sketch, "E7.0.3.2", {"start": v(-97.79, 10.24) * mm, "end": v(-88.79, 10.24) * mm});
            skLineSegment(sketch, "E7.0.3.3", {"start": v(-97.79, 16.24) * mm, "end": v(-97.79, 10.24) * mm});
            skLineSegment(sketch, "E7.0.4.0", {"start": v(-97.79, -16.76) * mm, "end": v(-88.79, -16.76) * mm});
            skLineSegment(sketch, "E7.0.4.1", {"start": v(-88.79, -16.76) * mm, "end": v(-88.79, -22.76) * mm});
            skLineSegment(sketch, "E7.0.4.2", {"start": v(-97.79, -22.76) * mm, "end": v(-88.79, -22.76) * mm});
            skLineSegment(sketch, "E7.0.4.3", {"start": v(-97.79, -16.76) * mm, "end": v(-97.79, -22.76) * mm});
            skLineSegment(sketch, "E7.0.5.0", {"start": v(-97.79, -49.76) * mm, "end": v(-88.79, -49.76) * mm});
            skLineSegment(sketch, "E7.0.5.1", {"start": v(-88.79, -49.76) * mm, "end": v(-88.79, -55.76) * mm});
            skLineSegment(sketch, "E7.0.5.2", {"start": v(-97.79, -55.76) * mm, "end": v(-88.79, -55.76) * mm});
            skLineSegment(sketch, "E7.0.5.3", {"start": v(-97.79, -49.76) * mm, "end": v(-97.79, -55.76) * mm});
            skLineSegment(sketch, "E7.1.0.0", {"start": v(-81.29, 115.24) * mm, "end": v(-72.29, 115.24) * mm});
            skLineSegment(sketch, "E7.1.0.1", {"start": v(-72.29, 115.24) * mm, "end": v(-72.29, 109.24) * mm});
            skLineSegment(sketch, "E7.1.0.2", {"start": v(-81.29, 109.24) * mm, "end": v(-72.29, 109.24) * mm});
            skLineSegment(sketch, "E7.1.0.3", {"start": v(-81.29, 115.24) * mm, "end": v(-81.29, 109.24) * mm});
            skLineSegment(sketch, "E7.1.1.0", {"start": v(-81.29, 82.24) * mm, "end": v(-72.29, 82.24) * mm});
            skLineSegment(sketch, "E7.1.1.1", {"start": v(-72.29, 82.24) * mm, "end": v(-72.29, 76.24) * mm});
            skLineSegment(sketch, "E7.1.1.2", {"start": v(-81.29, 76.24) * mm, "end": v(-72.29, 76.24) * mm});
            skLineSegment(sketch, "E7.1.1.3", {"start": v(-81.29, 82.24) * mm, "end": v(-81.29, 76.24) * mm});
            skLineSegment(sketch, "E7.1.2.0", {"start": v(-81.29, 49.24) * mm, "end": v(-72.29, 49.24) * mm});
            skLineSegment(sketch, "E7.1.2.1", {"start": v(-72.29, 49.24) * mm, "end": v(-72.29, 43.24) * mm});
            skLineSegment(sketch, "E7.1.2.2", {"start": v(-81.29, 43.24) * mm, "end": v(-72.29, 43.24) * mm});
            skLineSegment(sketch, "E7.1.2.3", {"start": v(-81.29, 49.24) * mm, "end": v(-81.29, 43.24) * mm});
            skLineSegment(sketch, "E7.1.3.0", {"start": v(-81.29, 16.24) * mm, "end": v(-72.29, 16.24) * mm});
            skLineSegment(sketch, "E7.1.3.1", {"start": v(-72.29, 16.24) * mm, "end": v(-72.29, 10.24) * mm});
            skLineSegment(sketch, "E7.1.3.2", {"start": v(-81.29, 10.24) * mm, "end": v(-72.29, 10.24) * mm});
            skLineSegment(sketch, "E7.1.3.3", {"start": v(-81.29, 16.24) * mm, "end": v(-81.29, 10.24) * mm});
            skLineSegment(sketch, "E7.1.4.0", {"start": v(-81.29, -16.76) * mm, "end": v(-72.29, -16.76) * mm});
            skLineSegment(sketch, "E7.1.4.1", {"start": v(-72.29, -16.76) * mm, "end": v(-72.29, -22.76) * mm});
            skLineSegment(sketch, "E7.1.4.2", {"start": v(-81.29, -22.76) * mm, "end": v(-72.29, -22.76) * mm});
            skLineSegment(sketch, "E7.1.4.3", {"start": v(-81.29, -16.76) * mm, "end": v(-81.29, -22.76) * mm});
            skLineSegment(sketch, "E7.1.5.0", {"start": v(-81.29, -49.76) * mm, "end": v(-72.29, -49.76) * mm});
            skLineSegment(sketch, "E7.1.5.1", {"start": v(-72.29, -49.76) * mm, "end": v(-72.29, -55.76) * mm});
            skLineSegment(sketch, "E7.1.5.2", {"start": v(-81.29, -55.76) * mm, "end": v(-72.29, -55.76) * mm});
            skLineSegment(sketch, "E7.1.5.3", {"start": v(-81.29, -49.76) * mm, "end": v(-81.29, -55.76) * mm});
            skLineSegment(sketch, "E7.2.0.0", {"start": v(-64.79, 115.24) * mm, "end": v(-55.79, 115.24) * mm});
            skLineSegment(sketch, "E7.2.0.1", {"start": v(-55.79, 115.24) * mm, "end": v(-55.79, 109.24) * mm});
            skLineSegment(sketch, "E7.2.0.2", {"start": v(-64.79, 109.24) * mm, "end": v(-55.79, 109.24) * mm});
            skLineSegment(sketch, "E7.2.0.3", {"start": v(-64.79, 115.24) * mm, "end": v(-64.79, 109.24) * mm});
            skLineSegment(sketch, "E7.2.1.0", {"start": v(-64.79, 82.24) * mm, "end": v(-55.79, 82.24) * mm});
            skLineSegment(sketch, "E7.2.1.1", {"start": v(-55.79, 82.24) * mm, "end": v(-55.79, 76.24) * mm});
            skLineSegment(sketch, "E7.2.1.2", {"start": v(-64.79, 76.24) * mm, "end": v(-55.79, 76.24) * mm});
            skLineSegment(sketch, "E7.2.1.3", {"start": v(-64.79, 82.24) * mm, "end": v(-64.79, 76.24) * mm});
            skLineSegment(sketch, "E7.2.2.0", {"start": v(-64.79, 49.24) * mm, "end": v(-55.79, 49.24) * mm});
            skLineSegment(sketch, "E7.2.2.1", {"start": v(-55.79, 49.24) * mm, "end": v(-55.79, 43.24) * mm});
            skLineSegment(sketch, "E7.2.2.2", {"start": v(-64.79, 43.24) * mm, "end": v(-55.79, 43.24) * mm});
            skLineSegment(sketch, "E7.2.2.3", {"start": v(-64.79, 49.24) * mm, "end": v(-64.79, 43.24) * mm});
            skLineSegment(sketch, "E7.2.3.0", {"start": v(-64.79, 16.24) * mm, "end": v(-55.79, 16.24) * mm});
            skLineSegment(sketch, "E7.2.3.1", {"start": v(-55.79, 16.24) * mm, "end": v(-55.79, 10.24) * mm});
            skLineSegment(sketch, "E7.2.3.2", {"start": v(-64.79, 10.24) * mm, "end": v(-55.79, 10.24) * mm});
            skLineSegment(sketch, "E7.2.3.3", {"start": v(-64.79, 16.24) * mm, "end": v(-64.79, 10.24) * mm});
            skLineSegment(sketch, "E7.2.4.0", {"start": v(-64.79, -16.76) * mm, "end": v(-55.79, -16.76) * mm});
            skLineSegment(sketch, "E7.2.4.1", {"start": v(-55.79, -16.76) * mm, "end": v(-55.79, -22.76) * mm});
            skLineSegment(sketch, "E7.2.4.2", {"start": v(-64.79, -22.76) * mm, "end": v(-55.79, -22.76) * mm});
            skLineSegment(sketch, "E7.2.4.3", {"start": v(-64.79, -16.76) * mm, "end": v(-64.79, -22.76) * mm});
            skLineSegment(sketch, "E7.2.5.0", {"start": v(-64.79, -49.76) * mm, "end": v(-55.79, -49.76) * mm});
            skLineSegment(sketch, "E7.2.5.1", {"start": v(-55.79, -49.76) * mm, "end": v(-55.79, -55.76) * mm});
            skLineSegment(sketch, "E7.2.5.2", {"start": v(-64.79, -55.76) * mm, "end": v(-55.79, -55.76) * mm});
            skLineSegment(sketch, "E7.2.5.3", {"start": v(-64.79, -49.76) * mm, "end": v(-64.79, -55.76) * mm});
            skLineSegment(sketch, "E7.3.0.0", {"start": v(-48.29, 115.24) * mm, "end": v(-39.29, 115.24) * mm});
            skLineSegment(sketch, "E7.3.0.1", {"start": v(-39.29, 115.24) * mm, "end": v(-39.29, 109.24) * mm});
            skLineSegment(sketch, "E7.3.0.2", {"start": v(-48.29, 109.24) * mm, "end": v(-39.29, 109.24) * mm});
            skLineSegment(sketch, "E7.3.0.3", {"start": v(-48.29, 115.24) * mm, "end": v(-48.29, 109.24) * mm});
            skLineSegment(sketch, "E7.3.1.0", {"start": v(-48.29, 82.24) * mm, "end": v(-39.29, 82.24) * mm});
            skLineSegment(sketch, "E7.3.1.1", {"start": v(-39.29, 82.24) * mm, "end": v(-39.29, 76.24) * mm});
            skLineSegment(sketch, "E7.3.1.2", {"start": v(-48.29, 76.24) * mm, "end": v(-39.29, 76.24) * mm});
            skLineSegment(sketch, "E7.3.1.3", {"start": v(-48.29, 82.24) * mm, "end": v(-48.29, 76.24) * mm});
            skLineSegment(sketch, "E7.3.2.0", {"start": v(-48.29, 49.24) * mm, "end": v(-39.29, 49.24) * mm});
            skLineSegment(sketch, "E7.3.2.1", {"start": v(-39.29, 49.24) * mm, "end": v(-39.29, 43.24) * mm});
            skLineSegment(sketch, "E7.3.2.2", {"start": v(-48.29, 43.24) * mm, "end": v(-39.29, 43.24) * mm});
            skLineSegment(sketch, "E7.3.2.3", {"start": v(-48.29, 49.24) * mm, "end": v(-48.29, 43.24) * mm});
            skLineSegment(sketch, "E7.3.3.0", {"start": v(-48.29, 16.24) * mm, "end": v(-39.29, 16.24) * mm});
            skLineSegment(sketch, "E7.3.3.1", {"start": v(-39.29, 16.24) * mm, "end": v(-39.29, 10.24) * mm});
            skLineSegment(sketch, "E7.3.3.2", {"start": v(-48.29, 10.24) * mm, "end": v(-39.29, 10.24) * mm});
            skLineSegment(sketch, "E7.3.3.3", {"start": v(-48.29, 16.24) * mm, "end": v(-48.29, 10.24) * mm});
            skLineSegment(sketch, "E7.3.4.0", {"start": v(-48.29, -16.76) * mm, "end": v(-39.29, -16.76) * mm});
            skLineSegment(sketch, "E7.3.4.1", {"start": v(-39.29, -16.76) * mm, "end": v(-39.29, -22.76) * mm});
            skLineSegment(sketch, "E7.3.4.2", {"start": v(-48.29, -22.76) * mm, "end": v(-39.29, -22.76) * mm});
            skLineSegment(sketch, "E7.3.4.3", {"start": v(-48.29, -16.76) * mm, "end": v(-48.29, -22.76) * mm});
            skLineSegment(sketch, "E7.3.5.0", {"start": v(-48.29, -49.76) * mm, "end": v(-39.29, -49.76) * mm});
            skLineSegment(sketch, "E7.3.5.1", {"start": v(-39.29, -49.76) * mm, "end": v(-39.29, -55.76) * mm});
            skLineSegment(sketch, "E7.3.5.2", {"start": v(-48.29, -55.76) * mm, "end": v(-39.29, -55.76) * mm});
            skLineSegment(sketch, "E7.3.5.3", {"start": v(-48.29, -49.76) * mm, "end": v(-48.29, -55.76) * mm});
            skLineSegment(sketch, "E7.4.0.0", {"start": v(-31.79, 115.24) * mm, "end": v(-22.79, 115.24) * mm});
            skLineSegment(sketch, "E7.4.0.1", {"start": v(-22.79, 115.24) * mm, "end": v(-22.79, 109.24) * mm});
            skLineSegment(sketch, "E7.4.0.2", {"start": v(-31.79, 109.24) * mm, "end": v(-22.79, 109.24) * mm});
            skLineSegment(sketch, "E7.4.0.3", {"start": v(-31.79, 115.24) * mm, "end": v(-31.79, 109.24) * mm});
            skLineSegment(sketch, "E7.4.1.0", {"start": v(-31.79, 82.24) * mm, "end": v(-22.79, 82.24) * mm});
            skLineSegment(sketch, "E7.4.1.1", {"start": v(-22.79, 82.24) * mm, "end": v(-22.79, 76.24) * mm});
            skLineSegment(sketch, "E7.4.1.2", {"start": v(-31.79, 76.24) * mm, "end": v(-22.79, 76.24) * mm});
            skLineSegment(sketch, "E7.4.1.3", {"start": v(-31.79, 82.24) * mm, "end": v(-31.79, 76.24) * mm});
            skLineSegment(sketch, "E7.4.2.0", {"start": v(-31.79, 49.24) * mm, "end": v(-22.79, 49.24) * mm});
            skLineSegment(sketch, "E7.4.2.1", {"start": v(-22.79, 49.24) * mm, "end": v(-22.79, 43.24) * mm});
            skLineSegment(sketch, "E7.4.2.2", {"start": v(-31.79, 43.24) * mm, "end": v(-22.79, 43.24) * mm});
            skLineSegment(sketch, "E7.4.2.3", {"start": v(-31.79, 49.24) * mm, "end": v(-31.79, 43.24) * mm});
            skLineSegment(sketch, "E7.4.3.0", {"start": v(-31.79, 16.24) * mm, "end": v(-22.79, 16.24) * mm});
            skLineSegment(sketch, "E7.4.3.1", {"start": v(-22.79, 16.24) * mm, "end": v(-22.79, 10.24) * mm});
            skLineSegment(sketch, "E7.4.3.2", {"start": v(-31.79, 10.24) * mm, "end": v(-22.79, 10.24) * mm});
            skLineSegment(sketch, "E7.4.3.3", {"start": v(-31.79, 16.24) * mm, "end": v(-31.79, 10.24) * mm});
            skLineSegment(sketch, "E7.4.4.0", {"start": v(-31.79, -16.76) * mm, "end": v(-22.79, -16.76) * mm});
            skLineSegment(sketch, "E7.4.4.1", {"start": v(-22.79, -16.76) * mm, "end": v(-22.79, -22.76) * mm});
            skLineSegment(sketch, "E7.4.4.2", {"start": v(-31.79, -22.76) * mm, "end": v(-22.79, -22.76) * mm});
            skLineSegment(sketch, "E7.4.4.3", {"start": v(-31.79, -16.76) * mm, "end": v(-31.79, -22.76) * mm});
            skLineSegment(sketch, "E7.4.5.0", {"start": v(-31.79, -49.76) * mm, "end": v(-22.79, -49.76) * mm});
            skLineSegment(sketch, "E7.4.5.1", {"start": v(-22.79, -49.76) * mm, "end": v(-22.79, -55.76) * mm});
            skLineSegment(sketch, "E7.4.5.2", {"start": v(-31.79, -55.76) * mm, "end": v(-22.79, -55.76) * mm});
            skLineSegment(sketch, "E7.4.5.3", {"start": v(-31.79, -49.76) * mm, "end": v(-31.79, -55.76) * mm});
            skLineSegment(sketch, "E7.5.0.0", {"start": v(-15.29, 115.24) * mm, "end": v(-6.29, 115.24) * mm});
            skLineSegment(sketch, "E7.5.0.1", {"start": v(-6.29, 115.24) * mm, "end": v(-6.29, 109.24) * mm});
            skLineSegment(sketch, "E7.5.0.2", {"start": v(-15.29, 109.24) * mm, "end": v(-6.29, 109.24) * mm});
            skLineSegment(sketch, "E7.5.0.3", {"start": v(-15.29, 115.24) * mm, "end": v(-15.29, 109.24) * mm});
            skLineSegment(sketch, "E7.5.1.0", {"start": v(-15.29, 82.24) * mm, "end": v(-6.29, 82.24) * mm});
            skLineSegment(sketch, "E7.5.1.1", {"start": v(-6.29, 82.24) * mm, "end": v(-6.29, 76.24) * mm});
            skLineSegment(sketch, "E7.5.1.2", {"start": v(-15.29, 76.24) * mm, "end": v(-6.29, 76.24) * mm});
            skLineSegment(sketch, "E7.5.1.3", {"start": v(-15.29, 82.24) * mm, "end": v(-15.29, 76.24) * mm});
            skLineSegment(sketch, "E7.5.2.0", {"start": v(-15.29, 49.24) * mm, "end": v(-6.29, 49.24) * mm});
            skLineSegment(sketch, "E7.5.2.1", {"start": v(-6.29, 49.24) * mm, "end": v(-6.29, 43.24) * mm});
            skLineSegment(sketch, "E7.5.2.2", {"start": v(-15.29, 43.24) * mm, "end": v(-6.29, 43.24) * mm});
            skLineSegment(sketch, "E7.5.2.3", {"start": v(-15.29, 49.24) * mm, "end": v(-15.29, 43.24) * mm});
            skLineSegment(sketch, "E7.5.3.0", {"start": v(-15.29, 16.24) * mm, "end": v(-6.29, 16.24) * mm});
            skLineSegment(sketch, "E7.5.3.1", {"start": v(-6.29, 16.24) * mm, "end": v(-6.29, 10.24) * mm});
            skLineSegment(sketch, "E7.5.3.2", {"start": v(-15.29, 10.24) * mm, "end": v(-6.29, 10.24) * mm});
            skLineSegment(sketch, "E7.5.3.3", {"start": v(-15.29, 16.24) * mm, "end": v(-15.29, 10.24) * mm});
            skLineSegment(sketch, "E7.5.4.0", {"start": v(-15.29, -16.76) * mm, "end": v(-6.29, -16.76) * mm});
            skLineSegment(sketch, "E7.5.4.1", {"start": v(-6.29, -16.76) * mm, "end": v(-6.29, -22.76) * mm});
            skLineSegment(sketch, "E7.5.4.2", {"start": v(-15.29, -22.76) * mm, "end": v(-6.29, -22.76) * mm});
            skLineSegment(sketch, "E7.5.4.3", {"start": v(-15.29, -16.76) * mm, "end": v(-15.29, -22.76) * mm});
            skLineSegment(sketch, "E7.5.5.0", {"start": v(-15.29, -49.76) * mm, "end": v(-6.29, -49.76) * mm});
            skLineSegment(sketch, "E7.5.5.1", {"start": v(-6.29, -49.76) * mm, "end": v(-6.29, -55.76) * mm});
            skLineSegment(sketch, "E7.5.5.2", {"start": v(-15.29, -55.76) * mm, "end": v(-6.29, -55.76) * mm});
            skLineSegment(sketch, "E7.5.5.3", {"start": v(-15.29, -49.76) * mm, "end": v(-15.29, -55.76) * mm});
            skLineSegment(sketch, "E7.6.0.0", {"start": v(1.21, 115.24) * mm, "end": v(10.21, 115.24) * mm});
            skLineSegment(sketch, "E7.6.0.1", {"start": v(10.21, 115.24) * mm, "end": v(10.21, 109.24) * mm});
            skLineSegment(sketch, "E7.6.0.2", {"start": v(1.21, 109.24) * mm, "end": v(10.21, 109.24) * mm});
            skLineSegment(sketch, "E7.6.0.3", {"start": v(1.21, 115.24) * mm, "end": v(1.21, 109.24) * mm});
            skLineSegment(sketch, "E7.6.1.0", {"start": v(1.21, 82.24) * mm, "end": v(10.21, 82.24) * mm});
            skLineSegment(sketch, "E7.6.1.1", {"start": v(10.21, 82.24) * mm, "end": v(10.21, 76.24) * mm});
            skLineSegment(sketch, "E7.6.1.2", {"start": v(1.21, 76.24) * mm, "end": v(10.21, 76.24) * mm});
            skLineSegment(sketch, "E7.6.1.3", {"start": v(1.21, 82.24) * mm, "end": v(1.21, 76.24) * mm});
            skLineSegment(sketch, "E7.6.2.0", {"start": v(1.21, 49.24) * mm, "end": v(10.21, 49.24) * mm});
            skLineSegment(sketch, "E7.6.2.1", {"start": v(10.21, 49.24) * mm, "end": v(10.21, 43.24) * mm});
            skLineSegment(sketch, "E7.6.2.2", {"start": v(1.21, 43.24) * mm, "end": v(10.21, 43.24) * mm});
            skLineSegment(sketch, "E7.6.2.3", {"start": v(1.21, 49.24) * mm, "end": v(1.21, 43.24) * mm});
            skLineSegment(sketch, "E7.6.3.0", {"start": v(1.21, 16.24) * mm, "end": v(10.21, 16.24) * mm});
            skLineSegment(sketch, "E7.6.3.1", {"start": v(10.21, 16.24) * mm, "end": v(10.21, 10.24) * mm});
            skLineSegment(sketch, "E7.6.3.2", {"start": v(1.21, 10.24) * mm, "end": v(10.21, 10.24) * mm});
            skLineSegment(sketch, "E7.6.3.3", {"start": v(1.21, 16.24) * mm, "end": v(1.21, 10.24) * mm});
            skLineSegment(sketch, "E7.6.4.0", {"start": v(1.21, -16.76) * mm, "end": v(10.21, -16.76) * mm});
            skLineSegment(sketch, "E7.6.4.1", {"start": v(10.21, -16.76) * mm, "end": v(10.21, -22.76) * mm});
            skLineSegment(sketch, "E7.6.4.2", {"start": v(1.21, -22.76) * mm, "end": v(10.21, -22.76) * mm});
            skLineSegment(sketch, "E7.6.4.3", {"start": v(1.21, -16.76) * mm, "end": v(1.21, -22.76) * mm});
            skLineSegment(sketch, "E7.6.5.0", {"start": v(1.21, -49.76) * mm, "end": v(10.21, -49.76) * mm});
            skLineSegment(sketch, "E7.6.5.1", {"start": v(10.21, -49.76) * mm, "end": v(10.21, -55.76) * mm});
            skLineSegment(sketch, "E7.6.5.2", {"start": v(1.21, -55.76) * mm, "end": v(10.21, -55.76) * mm});
            skLineSegment(sketch, "E7.6.5.3", {"start": v(1.21, -49.76) * mm, "end": v(1.21, -55.76) * mm});
            skLineSegment(sketch, "E7.7.0.0", {"start": v(17.71, 115.24) * mm, "end": v(26.71, 115.24) * mm});
            skLineSegment(sketch, "E7.7.0.1", {"start": v(26.71, 115.24) * mm, "end": v(26.71, 109.24) * mm});
            skLineSegment(sketch, "E7.7.0.2", {"start": v(17.71, 109.24) * mm, "end": v(26.71, 109.24) * mm});
            skLineSegment(sketch, "E7.7.0.3", {"start": v(17.71, 115.24) * mm, "end": v(17.71, 109.24) * mm});
            skLineSegment(sketch, "E7.7.1.0", {"start": v(17.71, 82.24) * mm, "end": v(26.71, 82.24) * mm});
            skLineSegment(sketch, "E7.7.1.1", {"start": v(26.71, 82.24) * mm, "end": v(26.71, 76.24) * mm});
            skLineSegment(sketch, "E7.7.1.2", {"start": v(17.71, 76.24) * mm, "end": v(26.71, 76.24) * mm});
            skLineSegment(sketch, "E7.7.1.3", {"start": v(17.71, 82.24) * mm, "end": v(17.71, 76.24) * mm});
            skLineSegment(sketch, "E7.7.2.0", {"start": v(17.71, 49.24) * mm, "end": v(26.71, 49.24) * mm});
            skLineSegment(sketch, "E7.7.2.1", {"start": v(26.71, 49.24) * mm, "end": v(26.71, 43.24) * mm});
            skLineSegment(sketch, "E7.7.2.2", {"start": v(17.71, 43.24) * mm, "end": v(26.71, 43.24) * mm});
            skLineSegment(sketch, "E7.7.2.3", {"start": v(17.71, 49.24) * mm, "end": v(17.71, 43.24) * mm});
            skLineSegment(sketch, "E7.7.3.0", {"start": v(17.71, 16.24) * mm, "end": v(26.71, 16.24) * mm});
            skLineSegment(sketch, "E7.7.3.1", {"start": v(26.71, 16.24) * mm, "end": v(26.71, 10.24) * mm});
            skLineSegment(sketch, "E7.7.3.2", {"start": v(17.71, 10.24) * mm, "end": v(26.71, 10.24) * mm});
            skLineSegment(sketch, "E7.7.3.3", {"start": v(17.71, 16.24) * mm, "end": v(17.71, 10.24) * mm});
            skLineSegment(sketch, "E7.7.4.0", {"start": v(17.71, -16.76) * mm, "end": v(26.71, -16.76) * mm});
            skLineSegment(sketch, "E7.7.4.1", {"start": v(26.71, -16.76) * mm, "end": v(26.71, -22.76) * mm});
            skLineSegment(sketch, "E7.7.4.2", {"start": v(17.71, -22.76) * mm, "end": v(26.71, -22.76) * mm});
            skLineSegment(sketch, "E7.7.4.3", {"start": v(17.71, -16.76) * mm, "end": v(17.71, -22.76) * mm});
            skLineSegment(sketch, "E7.7.5.0", {"start": v(17.71, -49.76) * mm, "end": v(26.71, -49.76) * mm});
            skLineSegment(sketch, "E7.7.5.1", {"start": v(26.71, -49.76) * mm, "end": v(26.71, -55.76) * mm});
            skLineSegment(sketch, "E7.7.5.2", {"start": v(17.71, -55.76) * mm, "end": v(26.71, -55.76) * mm});
            skLineSegment(sketch, "E7.7.5.3", {"start": v(17.71, -49.76) * mm, "end": v(17.71, -55.76) * mm});
            skLineSegment(sketch, "E7.8.0.0", {"start": v(34.21, 115.24) * mm, "end": v(43.21, 115.24) * mm});
            skLineSegment(sketch, "E7.8.0.1", {"start": v(43.21, 115.24) * mm, "end": v(43.21, 109.24) * mm});
            skLineSegment(sketch, "E7.8.0.2", {"start": v(34.21, 109.24) * mm, "end": v(43.21, 109.24) * mm});
            skLineSegment(sketch, "E7.8.0.3", {"start": v(34.21, 115.24) * mm, "end": v(34.21, 109.24) * mm});
            skLineSegment(sketch, "E7.8.1.0", {"start": v(34.21, 82.24) * mm, "end": v(43.21, 82.24) * mm});
            skLineSegment(sketch, "E7.8.1.1", {"start": v(43.21, 82.24) * mm, "end": v(43.21, 76.24) * mm});
            skLineSegment(sketch, "E7.8.1.2", {"start": v(34.21, 76.24) * mm, "end": v(43.21, 76.24) * mm});
            skLineSegment(sketch, "E7.8.1.3", {"start": v(34.21, 82.24) * mm, "end": v(34.21, 76.24) * mm});
            skLineSegment(sketch, "E7.8.2.0", {"start": v(34.21, 49.24) * mm, "end": v(43.21, 49.24) * mm});
            skLineSegment(sketch, "E7.8.2.1", {"start": v(43.21, 49.24) * mm, "end": v(43.21, 43.24) * mm});
            skLineSegment(sketch, "E7.8.2.2", {"start": v(34.21, 43.24) * mm, "end": v(43.21, 43.24) * mm});
            skLineSegment(sketch, "E7.8.2.3", {"start": v(34.21, 49.24) * mm, "end": v(34.21, 43.24) * mm});
            skLineSegment(sketch, "E7.8.3.0", {"start": v(34.21, 16.24) * mm, "end": v(43.21, 16.24) * mm});
            skLineSegment(sketch, "E7.8.3.1", {"start": v(43.21, 16.24) * mm, "end": v(43.21, 10.24) * mm});
            skLineSegment(sketch, "E7.8.3.2", {"start": v(34.21, 10.24) * mm, "end": v(43.21, 10.24) * mm});
            skLineSegment(sketch, "E7.8.3.3", {"start": v(34.21, 16.24) * mm, "end": v(34.21, 10.24) * mm});
            skLineSegment(sketch, "E7.8.4.0", {"start": v(34.21, -16.76) * mm, "end": v(43.21, -16.76) * mm});
            skLineSegment(sketch, "E7.8.4.1", {"start": v(43.21, -16.76) * mm, "end": v(43.21, -22.76) * mm});
            skLineSegment(sketch, "E7.8.4.2", {"start": v(34.21, -22.76) * mm, "end": v(43.21, -22.76) * mm});
            skLineSegment(sketch, "E7.8.4.3", {"start": v(34.21, -16.76) * mm, "end": v(34.21, -22.76) * mm});
            skLineSegment(sketch, "E7.8.5.0", {"start": v(34.21, -49.76) * mm, "end": v(43.21, -49.76) * mm});
            skLineSegment(sketch, "E7.8.5.1", {"start": v(43.21, -49.76) * mm, "end": v(43.21, -55.76) * mm});
            skLineSegment(sketch, "E7.8.5.2", {"start": v(34.21, -55.76) * mm, "end": v(43.21, -55.76) * mm});
            skLineSegment(sketch, "E7.8.5.3", {"start": v(34.21, -49.76) * mm, "end": v(34.21, -55.76) * mm});
            skLineSegment(sketch, "E7.9.0.0", {"start": v(50.71, 115.24) * mm, "end": v(59.71, 115.24) * mm});
            skLineSegment(sketch, "E7.9.0.1", {"start": v(59.71, 115.24) * mm, "end": v(59.71, 109.24) * mm});
            skLineSegment(sketch, "E7.9.0.2", {"start": v(50.71, 109.24) * mm, "end": v(59.71, 109.24) * mm});
            skLineSegment(sketch, "E7.9.0.3", {"start": v(50.71, 115.24) * mm, "end": v(50.71, 109.24) * mm});
            skLineSegment(sketch, "E7.9.1.0", {"start": v(50.71, 82.24) * mm, "end": v(59.71, 82.24) * mm});
            skLineSegment(sketch, "E7.9.1.1", {"start": v(59.71, 82.24) * mm, "end": v(59.71, 76.24) * mm});
            skLineSegment(sketch, "E7.9.1.2", {"start": v(50.71, 76.24) * mm, "end": v(59.71, 76.24) * mm});
            skLineSegment(sketch, "E7.9.1.3", {"start": v(50.71, 82.24) * mm, "end": v(50.71, 76.24) * mm});
            skLineSegment(sketch, "E7.9.2.0", {"start": v(50.71, 49.24) * mm, "end": v(59.71, 49.24) * mm});
            skLineSegment(sketch, "E7.9.2.1", {"start": v(59.71, 49.24) * mm, "end": v(59.71, 43.24) * mm});
            skLineSegment(sketch, "E7.9.2.2", {"start": v(50.71, 43.24) * mm, "end": v(59.71, 43.24) * mm});
            skLineSegment(sketch, "E7.9.2.3", {"start": v(50.71, 49.24) * mm, "end": v(50.71, 43.24) * mm});
            skLineSegment(sketch, "E7.9.3.0", {"start": v(50.71, 16.24) * mm, "end": v(59.71, 16.24) * mm});
            skLineSegment(sketch, "E7.9.3.1", {"start": v(59.71, 16.24) * mm, "end": v(59.71, 10.24) * mm});
            skLineSegment(sketch, "E7.9.3.2", {"start": v(50.71, 10.24) * mm, "end": v(59.71, 10.24) * mm});
            skLineSegment(sketch, "E7.9.3.3", {"start": v(50.71, 16.24) * mm, "end": v(50.71, 10.24) * mm});
            skLineSegment(sketch, "E7.9.4.0", {"start": v(50.71, -16.76) * mm, "end": v(59.71, -16.76) * mm});
            skLineSegment(sketch, "E7.9.4.1", {"start": v(59.71, -16.76) * mm, "end": v(59.71, -22.76) * mm});
            skLineSegment(sketch, "E7.9.4.2", {"start": v(50.71, -22.76) * mm, "end": v(59.71, -22.76) * mm});
            skLineSegment(sketch, "E7.9.4.3", {"start": v(50.71, -16.76) * mm, "end": v(50.71, -22.76) * mm});
            skLineSegment(sketch, "E7.9.5.0", {"start": v(50.71, -49.76) * mm, "end": v(59.71, -49.76) * mm});
            skLineSegment(sketch, "E7.9.5.1", {"start": v(59.71, -49.76) * mm, "end": v(59.71, -55.76) * mm});
            skLineSegment(sketch, "E7.9.5.2", {"start": v(50.71, -55.76) * mm, "end": v(59.71, -55.76) * mm});
            skLineSegment(sketch, "E7.9.5.3", {"start": v(50.71, -49.76) * mm, "end": v(50.71, -55.76) * mm});
            skLineSegment(sketch, "E7.10.0.0", {"start": v(67.21, 115.24) * mm, "end": v(76.21, 115.24) * mm});
            skLineSegment(sketch, "E7.10.0.1", {"start": v(76.21, 115.24) * mm, "end": v(76.21, 109.24) * mm});
            skLineSegment(sketch, "E7.10.0.2", {"start": v(67.21, 109.24) * mm, "end": v(76.21, 109.24) * mm});
            skLineSegment(sketch, "E7.10.0.3", {"start": v(67.21, 115.24) * mm, "end": v(67.21, 109.24) * mm});
            skLineSegment(sketch, "E7.10.1.0", {"start": v(67.21, 82.24) * mm, "end": v(76.21, 82.24) * mm});
            skLineSegment(sketch, "E7.10.1.1", {"start": v(76.21, 82.24) * mm, "end": v(76.21, 76.24) * mm});
            skLineSegment(sketch, "E7.10.1.2", {"start": v(67.21, 76.24) * mm, "end": v(76.21, 76.24) * mm});
            skLineSegment(sketch, "E7.10.1.3", {"start": v(67.21, 82.24) * mm, "end": v(67.21, 76.24) * mm});
            skLineSegment(sketch, "E7.10.2.0", {"start": v(67.21, 49.24) * mm, "end": v(76.21, 49.24) * mm});
            skLineSegment(sketch, "E7.10.2.1", {"start": v(76.21, 49.24) * mm, "end": v(76.21, 43.24) * mm});
            skLineSegment(sketch, "E7.10.2.2", {"start": v(67.21, 43.24) * mm, "end": v(76.21, 43.24) * mm});
            skLineSegment(sketch, "E7.10.2.3", {"start": v(67.21, 49.24) * mm, "end": v(67.21, 43.24) * mm});
            skLineSegment(sketch, "E7.10.3.0", {"start": v(67.21, 16.24) * mm, "end": v(76.21, 16.24) * mm});
            skLineSegment(sketch, "E7.10.3.1", {"start": v(76.21, 16.24) * mm, "end": v(76.21, 10.24) * mm});
            skLineSegment(sketch, "E7.10.3.2", {"start": v(67.21, 10.24) * mm, "end": v(76.21, 10.24) * mm});
            skLineSegment(sketch, "E7.10.3.3", {"start": v(67.21, 16.24) * mm, "end": v(67.21, 10.24) * mm});
            skLineSegment(sketch, "E7.10.4.0", {"start": v(67.21, -16.76) * mm, "end": v(76.21, -16.76) * mm});
            skLineSegment(sketch, "E7.10.4.1", {"start": v(76.21, -16.76) * mm, "end": v(76.21, -22.76) * mm});
            skLineSegment(sketch, "E7.10.4.2", {"start": v(67.21, -22.76) * mm, "end": v(76.21, -22.76) * mm});
            skLineSegment(sketch, "E7.10.4.3", {"start": v(67.21, -16.76) * mm, "end": v(67.21, -22.76) * mm});
            skLineSegment(sketch, "E7.10.5.0", {"start": v(67.21, -49.76) * mm, "end": v(76.21, -49.76) * mm});
            skLineSegment(sketch, "E7.10.5.1", {"start": v(76.21, -49.76) * mm, "end": v(76.21, -55.76) * mm});
            skLineSegment(sketch, "E7.10.5.2", {"start": v(67.21, -55.76) * mm, "end": v(76.21, -55.76) * mm});
            skLineSegment(sketch, "E7.10.5.3", {"start": v(67.21, -49.76) * mm, "end": v(67.21, -55.76) * mm});
            skLineSegment(sketch, "E7.11.0.0", {"start": v(83.71, 115.24) * mm, "end": v(92.71, 115.24) * mm});
            skLineSegment(sketch, "E7.11.0.1", {"start": v(92.71, 115.24) * mm, "end": v(92.71, 109.24) * mm});
            skLineSegment(sketch, "E7.11.0.2", {"start": v(83.71, 109.24) * mm, "end": v(92.71, 109.24) * mm});
            skLineSegment(sketch, "E7.11.0.3", {"start": v(83.71, 115.24) * mm, "end": v(83.71, 109.24) * mm});
            skLineSegment(sketch, "E7.11.1.0", {"start": v(83.71, 82.24) * mm, "end": v(92.71, 82.24) * mm});
            skLineSegment(sketch, "E7.11.1.1", {"start": v(92.71, 82.24) * mm, "end": v(92.71, 76.24) * mm});
            skLineSegment(sketch, "E7.11.1.2", {"start": v(83.71, 76.24) * mm, "end": v(92.71, 76.24) * mm});
            skLineSegment(sketch, "E7.11.1.3", {"start": v(83.71, 82.24) * mm, "end": v(83.71, 76.24) * mm});
            skLineSegment(sketch, "E7.11.2.0", {"start": v(83.71, 49.24) * mm, "end": v(92.71, 49.24) * mm});
            skLineSegment(sketch, "E7.11.2.1", {"start": v(92.71, 49.24) * mm, "end": v(92.71, 43.24) * mm});
            skLineSegment(sketch, "E7.11.2.2", {"start": v(83.71, 43.24) * mm, "end": v(92.71, 43.24) * mm});
            skLineSegment(sketch, "E7.11.2.3", {"start": v(83.71, 49.24) * mm, "end": v(83.71, 43.24) * mm});
            skLineSegment(sketch, "E7.11.3.0", {"start": v(83.71, 16.24) * mm, "end": v(92.71, 16.24) * mm});
            skLineSegment(sketch, "E7.11.3.1", {"start": v(92.71, 16.24) * mm, "end": v(92.71, 10.24) * mm});
            skLineSegment(sketch, "E7.11.3.2", {"start": v(83.71, 10.24) * mm, "end": v(92.71, 10.24) * mm});
            skLineSegment(sketch, "E7.11.3.3", {"start": v(83.71, 16.24) * mm, "end": v(83.71, 10.24) * mm});
            skLineSegment(sketch, "E7.11.4.0", {"start": v(83.71, -16.76) * mm, "end": v(92.71, -16.76) * mm});
            skLineSegment(sketch, "E7.11.4.1", {"start": v(92.71, -16.76) * mm, "end": v(92.71, -22.76) * mm});
            skLineSegment(sketch, "E7.11.4.2", {"start": v(83.71, -22.76) * mm, "end": v(92.71, -22.76) * mm});
            skLineSegment(sketch, "E7.11.4.3", {"start": v(83.71, -16.76) * mm, "end": v(83.71, -22.76) * mm});
            skLineSegment(sketch, "E7.11.5.0", {"start": v(83.71, -49.76) * mm, "end": v(92.71, -49.76) * mm});
            skLineSegment(sketch, "E7.11.5.1", {"start": v(92.71, -49.76) * mm, "end": v(92.71, -55.76) * mm});
            skLineSegment(sketch, "E7.11.5.2", {"start": v(83.71, -55.76) * mm, "end": v(92.71, -55.76) * mm});
            skLineSegment(sketch, "E7.11.5.3", {"start": v(83.71, -49.76) * mm, "end": v(83.71, -55.76) * mm});
            skLineSegment(sketch, "E7.direction1", {"start": v(-97.79, 115.24) * mm, "end": v(-81.29, 115.24) * mm, "construction": true});
            skLineSegment(sketch, "E7.direction2", {"start": v(-97.79, 115.24) * mm, "end": v(-97.79, 82.24) * mm, "construction": true});
            skSolve(sketch);
        }
        {
            var Q0;
            Q0=makeQuery(id+"F0.imprint","IMPRINT",FACE,{"disambiguationData":[TD([[makeQuery(id+"F0.imprint","IMPRINT",EDGE,{"derivedFrom":sQuery(id+"F0.wireOp",EDGE,"E0.bottom")}),-1.0]])]});
            extrude(context, id + "F1", {"entities" : qUnion([Q0]), "depth" : 3 * mm});
        }
        {
            var Q0;
            Q0=makeQuery(id+"F1.opExtrude","CAP_FACE",FACE,{"disambiguationData":[OSD([sQuery(id+"F0.wireOp",EDGE,"E0.bottom"),sQuery(id+"F0.wireOp",EDGE,"E0.top"),sQuery(id+"F0.wireOp",EDGE,"E0.left"),sQuery(id+"F0.wireOp",EDGE,"E0.right"),sQuery(id+"F0.wireOp",EDGE,"E1.bottom"),sQuery(id+"F0.wireOp",EDGE,"E1.top"),sQuery(id+"F0.wireOp",EDGE,"E1.left"),sQuery(id+"F0.wireOp",EDGE,"E1.right"),sQuery(id+"F0.wireOp",EDGE,"E4.3.1.0"),sQuery(id+"F0.wireOp",EDGE,"E4.6.1.0"),sQuery(id+"F0.wireOp",EDGE,"E4.9.1.0"),sQuery(id+"F0.wireOp",EDGE,"E4.12.1.0"),sQuery(id+"F0.wireOp",EDGE,"E4.3.2.0"),sQuery(id+"F0.wireOp",EDGE,"E4.6.2.0"),sQuery(id+"F0.wireOp",EDGE,"E4.9.2.0"),sQuery(id+"F0.wireOp",EDGE,"E4.12.2.0"),sQuery(id+"F0.wireOp",EDGE,"E4.3.3.0"),sQuery(id+"F0.wireOp",EDGE,"E4.6.3.0"),sQuery(id+"F0.wireOp",EDGE,"E4.9.3.0"),sQuery(id+"F0.wireOp",EDGE,"E4.12.3.0"),sQuery(id+"F0.wireOp",EDGE,"E4.3.4.0"),sQuery(id+"F0.wireOp",EDGE,"E4.6.4.0"),sQuery(id+"F0.wireOp",EDGE,"E4.9.4.0"),sQuery(id+"F0.wireOp",EDGE,"E4.12.4.0"),sQuery(id+"F0.wireOp",EDGE,"E4.3.5.0"),sQuery(id+"F0.wireOp",EDGE,"E4.6.5.0"),sQuery(id+"F0.wireOp",EDGE,"E4.9.5.0"),sQuery(id+"F0.wireOp",EDGE,"E4.12.5.0"),sQuery(id+"F0.wireOp",EDGE,"E4.3.6.0"),sQuery(id+"F0.wireOp",EDGE,"E4.6.6.0"),sQuery(id+"F0.wireOp",EDGE,"E4.9.6.0"),sQuery(id+"F0.wireOp",EDGE,"E4.12.6.0"),sQuery(id+"F0.wireOp",EDGE,"E4.3.7.0"),sQuery(id+"F0.wireOp",EDGE,"E4.6.7.0"),sQuery(id+"F0.wireOp",EDGE,"E4.9.7.0"),sQuery(id+"F0.wireOp",EDGE,"E4.12.7.0"),sQuery(id+"F0.wireOp",EDGE,"E4.3.8.0"),sQuery(id+"F0.wireOp",EDGE,"E4.6.8.0"),sQuery(id+"F0.wireOp",EDGE,"E4.9.8.0"),sQuery(id+"F0.wireOp",EDGE,"E4.12.8.0"),sQuery(id+"F0.wireOp",EDGE,"E4.3.9.0"),sQuery(id+"F0.wireOp",EDGE,"E4.6.9.0"),sQuery(id+"F0.wireOp",EDGE,"E4.9.9.0"),sQuery(id+"F0.wireOp",EDGE,"E4.12.9.0"),sQuery(id+"F0.wireOp",EDGE,"E4.3.10.0"),sQuery(id+"F0.wireOp",EDGE,"E4.6.10.0"),sQuery(id+"F0.wireOp",EDGE,"E4.9.10.0"),sQuery(id+"F0.wireOp",EDGE,"E4.12.10.0"),sQuery(id+"F0.wireOp",EDGE,"E4.3.11.0"),sQuery(id+"F0.wireOp",EDGE,"E4.6.11.0"),sQuery(id+"F0.wireOp",EDGE,"E4.9.11.0"),sQuery(id+"F0.wireOp",EDGE,"E4.12.11.0"),sQuery(id+"F0.wireOp",EDGE,"E5.3.0.1"),sQuery(id+"F0.wireOp",EDGE,"E5.6.0.1"),sQuery(id+"F0.wireOp",EDGE,"E5.9.0.1"),sQuery(id+"F0.wireOp",EDGE,"E5.12.0.1"),sQuery(id+"F0.wireOp",EDGE,"E5.3.0.2"),sQuery(id+"F0.wireOp",EDGE,"E5.6.0.2"),sQuery(id+"F0.wireOp",EDGE,"E5.9.0.2"),sQuery(id+"F0.wireOp",EDGE,"E5.12.0.2"),sQuery(id+"F0.wireOp",EDGE,"E5.3.0.3"),sQuery(id+"F0.wireOp",EDGE,"E5.6.0.3"),sQuery(id+"F0.wireOp",EDGE,"E5.9.0.3"),sQuery(id+"F0.wireOp",EDGE,"E5.12.0.3"),sQuery(id+"F0.wireOp",EDGE,"E5.3.0.4"),sQuery(id+"F0.wireOp",EDGE,"E5.6.0.4"),sQuery(id+"F0.wireOp",EDGE,"E5.9.0.4"),sQuery(id+"F0.wireOp",EDGE,"E5.12.0.4"),sQuery(id+"F0.wireOp",EDGE,"E5.3.0.5"),sQuery(id+"F0.wireOp",EDGE,"E5.6.0.5"),sQuery(id+"F0.wireOp",EDGE,"E5.9.0.5"),sQuery(id+"F0.wireOp",EDGE,"E5.12.0.5"),sQuery(id+"F0.wireOp",EDGE,"E5.3.1.1"),sQuery(id+"F0.wireOp",EDGE,"E5.6.1.1"),sQuery(id+"F0.wireOp",EDGE,"E5.9.1.1"),sQuery(id+"F0.wireOp",EDGE,"E5.12.1.1"),sQuery(id+"F0.wireOp",EDGE,"E5.3.1.2"),sQuery(id+"F0.wireOp",EDGE,"E5.6.1.2"),sQuery(id+"F0.wireOp",EDGE,"E5.9.1.2"),sQuery(id+"F0.wireOp",EDGE,"E5.12.1.2"),sQuery(id+"F0.wireOp",EDGE,"E5.3.1.3"),sQuery(id+"F0.wireOp",EDGE,"E5.6.1.3"),sQuery(id+"F0.wireOp",EDGE,"E5.9.1.3"),sQuery(id+"F0.wireOp",EDGE,"E5.12.1.3"),sQuery(id+"F0.wireOp",EDGE,"E5.3.1.4"),sQuery(id+"F0.wireOp",EDGE,"E5.6.1.4"),sQuery(id+"F0.wireOp",EDGE,"E5.9.1.4"),sQuery(id+"F0.wireOp",EDGE,"E5.12.1.4"),sQuery(id+"F0.wireOp",EDGE,"E5.3.1.5"),sQuery(id+"F0.wireOp",EDGE,"E5.6.1.5"),sQuery(id+"F0.wireOp",EDGE,"E5.9.1.5"),sQuery(id+"F0.wireOp",EDGE,"E5.12.1.5"),sQuery(id+"F0.wireOp",EDGE,"E5.3.2.1"),sQuery(id+"F0.wireOp",EDGE,"E5.6.2.1"),sQuery(id+"F0.wireOp",EDGE,"E5.9.2.1"),sQuery(id+"F0.wireOp",EDGE,"E5.12.2.1"),sQuery(id+"F0.wireOp",EDGE,"E5.3.2.2"),sQuery(id+"F0.wireOp",EDGE,"E5.6.2.2"),sQuery(id+"F0.wireOp",EDGE,"E5.9.2.2"),sQuery(id+"F0.wireOp",EDGE,"E5.12.2.2"),sQuery(id+"F0.wireOp",EDGE,"E5.3.2.3"),sQuery(id+"F0.wireOp",EDGE,"E5.6.2.3"),sQuery(id+"F0.wireOp",EDGE,"E5.9.2.3"),sQuery(id+"F0.wireOp",EDGE,"E5.12.2.3"),sQuery(id+"F0.wireOp",EDGE,"E5.3.2.4"),sQuery(id+"F0.wireOp",EDGE,"E5.6.2.4"),sQuery(id+"F0.wireOp",EDGE,"E5.9.2.4"),sQuery(id+"F0.wireOp",EDGE,"E5.12.2.4"),sQuery(id+"F0.wireOp",EDGE,"E5.3.2.5"),sQuery(id+"F0.wireOp",EDGE,"E5.6.2.5"),sQuery(id+"F0.wireOp",EDGE,"E5.9.2.5"),sQuery(id+"F0.wireOp",EDGE,"E5.12.2.5"),sQuery(id+"F0.wireOp",EDGE,"E5.3.3.1"),sQuery(id+"F0.wireOp",EDGE,"E5.6.3.1"),sQuery(id+"F0.wireOp",EDGE,"E5.9.3.1"),sQuery(id+"F0.wireOp",EDGE,"E5.12.3.1"),sQuery(id+"F0.wireOp",EDGE,"E5.3.3.2"),sQuery(id+"F0.wireOp",EDGE,"E5.6.3.2"),sQuery(id+"F0.wireOp",EDGE,"E5.9.3.2"),sQuery(id+"F0.wireOp",EDGE,"E5.12.3.2"),sQuery(id+"F0.wireOp",EDGE,"E5.3.3.3"),sQuery(id+"F0.wireOp",EDGE,"E5.6.3.3"),sQuery(id+"F0.wireOp",EDGE,"E5.9.3.3"),sQuery(id+"F0.wireOp",EDGE,"E5.12.3.3"),sQuery(id+"F0.wireOp",EDGE,"E5.3.3.4"),sQuery(id+"F0.wireOp",EDGE,"E5.6.3.4"),sQuery(id+"F0.wireOp",EDGE,"E5.9.3.4"),sQuery(id+"F0.wireOp",EDGE,"E5.12.3.4"),sQuery(id+"F0.wireOp",EDGE,"E5.3.3.5"),sQuery(id+"F0.wireOp",EDGE,"E5.6.3.5"),sQuery(id+"F0.wireOp",EDGE,"E5.9.3.5"),sQuery(id+"F0.wireOp",EDGE,"E5.12.3.5"),sQuery(id+"F0.wireOp",EDGE,"E5.3.4.1"),sQuery(id+"F0.wireOp",EDGE,"E5.6.4.1"),sQuery(id+"F0.wireOp",EDGE,"E5.9.4.1"),sQuery(id+"F0.wireOp",EDGE,"E5.12.4.1"),sQuery(id+"F0.wireOp",EDGE,"E5.3.4.2"),sQuery(id+"F0.wireOp",EDGE,"E5.6.4.2"),sQuery(id+"F0.wireOp",EDGE,"E5.9.4.2"),sQuery(id+"F0.wireOp",EDGE,"E5.12.4.2"),sQuery(id+"F0.wireOp",EDGE,"E5.3.4.3"),sQuery(id+"F0.wireOp",EDGE,"E5.6.4.3"),sQuery(id+"F0.wireOp",EDGE,"E5.9.4.3"),sQuery(id+"F0.wireOp",EDGE,"E5.12.4.3"),sQuery(id+"F0.wireOp",EDGE,"E5.3.4.4"),sQuery(id+"F0.wireOp",EDGE,"E5.6.4.4"),sQuery(id+"F0.wireOp",EDGE,"E5.9.4.4"),sQuery(id+"F0.wireOp",EDGE,"E5.12.4.4"),sQuery(id+"F0.wireOp",EDGE,"E5.3.4.5"),sQuery(id+"F0.wireOp",EDGE,"E5.6.4.5"),sQuery(id+"F0.wireOp",EDGE,"E5.9.4.5"),sQuery(id+"F0.wireOp",EDGE,"E5.12.4.5"),sQuery(id+"F0.wireOp",EDGE,"E5.3.5.1"),sQuery(id+"F0.wireOp",EDGE,"E5.6.5.1"),sQuery(id+"F0.wireOp",EDGE,"E5.9.5.1"),sQuery(id+"F0.wireOp",EDGE,"E5.12.5.1"),sQuery(id+"F0.wireOp",EDGE,"E5.3.5.2"),sQuery(id+"F0.wireOp",EDGE,"E5.6.5.2"),sQuery(id+"F0.wireOp",EDGE,"E5.9.5.2"),sQuery(id+"F0.wireOp",EDGE,"E5.12.5.2"),sQuery(id+"F0.wireOp",EDGE,"E5.3.5.3"),sQuery(id+"F0.wireOp",EDGE,"E5.6.5.3"),sQuery(id+"F0.wireOp",EDGE,"E5.9.5.3"),sQuery(id+"F0.wireOp",EDGE,"E5.12.5.3"),sQuery(id+"F0.wireOp",EDGE,"E5.3.5.4"),sQuery(id+"F0.wireOp",EDGE,"E5.6.5.4"),sQuery(id+"F0.wireOp",EDGE,"E5.9.5.4"),sQuery(id+"F0.wireOp",EDGE,"E5.12.5.4"),sQuery(id+"F0.wireOp",EDGE,"E5.3.5.5"),sQuery(id+"F0.wireOp",EDGE,"E5.6.5.5"),sQuery(id+"F0.wireOp",EDGE,"E5.9.5.5"),sQuery(id+"F0.wireOp",EDGE,"E5.12.5.5"),sQuery(id+"F0.wireOp",EDGE,"E5.3.6.1"),sQuery(id+"F0.wireOp",EDGE,"E5.6.6.1"),sQuery(id+"F0.wireOp",EDGE,"E5.9.6.1"),sQuery(id+"F0.wireOp",EDGE,"E5.12.6.1"),sQuery(id+"F0.wireOp",EDGE,"E5.3.6.2"),sQuery(id+"F0.wireOp",EDGE,"E5.6.6.2"),sQuery(id+"F0.wireOp",EDGE,"E5.9.6.2"),sQuery(id+"F0.wireOp",EDGE,"E5.12.6.2"),sQuery(id+"F0.wireOp",EDGE,"E5.3.6.3"),sQuery(id+"F0.wireOp",EDGE,"E5.6.6.3"),sQuery(id+"F0.wireOp",EDGE,"E5.9.6.3"),sQuery(id+"F0.wireOp",EDGE,"E5.12.6.3"),sQuery(id+"F0.wireOp",EDGE,"E5.3.6.4"),sQuery(id+"F0.wireOp",EDGE,"E5.6.6.4"),sQuery(id+"F0.wireOp",EDGE,"E5.9.6.4"),sQuery(id+"F0.wireOp",EDGE,"E5.12.6.4"),sQuery(id+"F0.wireOp",EDGE,"E5.3.6.5"),sQuery(id+"F0.wireOp",EDGE,"E5.6.6.5"),sQuery(id+"F0.wireOp",EDGE,"E5.9.6.5"),sQuery(id+"F0.wireOp",EDGE,"E5.12.6.5"),sQuery(id+"F0.wireOp",EDGE,"E5.3.7.1"),sQuery(id+"F0.wireOp",EDGE,"E5.6.7.1"),sQuery(id+"F0.wireOp",EDGE,"E5.9.7.1"),sQuery(id+"F0.wireOp",EDGE,"E5.12.7.1"),sQuery(id+"F0.wireOp",EDGE,"E5.3.7.2"),sQuery(id+"F0.wireOp",EDGE,"E5.6.7.2"),sQuery(id+"F0.wireOp",EDGE,"E5.9.7.2"),sQuery(id+"F0.wireOp",EDGE,"E5.12.7.2"),sQuery(id+"F0.wireOp",EDGE,"E5.3.7.3"),sQuery(id+"F0.wireOp",EDGE,"E5.6.7.3"),sQuery(id+"F0.wireOp",EDGE,"E5.9.7.3"),sQuery(id+"F0.wireOp",EDGE,"E5.12.7.3"),sQuery(id+"F0.wireOp",EDGE,"E5.3.7.4"),sQuery(id+"F0.wireOp",EDGE,"E5.6.7.4"),sQuery(id+"F0.wireOp",EDGE,"E5.9.7.4"),sQuery(id+"F0.wireOp",EDGE,"E5.12.7.4"),sQuery(id+"F0.wireOp",EDGE,"E5.3.7.5"),sQuery(id+"F0.wireOp",EDGE,"E5.6.7.5"),sQuery(id+"F0.wireOp",EDGE,"E5.9.7.5"),sQuery(id+"F0.wireOp",EDGE,"E5.12.7.5"),sQuery(id+"F0.wireOp",EDGE,"E5.3.8.1"),sQuery(id+"F0.wireOp",EDGE,"E5.6.8.1"),sQuery(id+"F0.wireOp",EDGE,"E5.9.8.1"),sQuery(id+"F0.wireOp",EDGE,"E5.12.8.1"),sQuery(id+"F0.wireOp",EDGE,"E5.3.8.2"),sQuery(id+"F0.wireOp",EDGE,"E5.6.8.2"),sQuery(id+"F0.wireOp",EDGE,"E5.9.8.2"),sQuery(id+"F0.wireOp",EDGE,"E5.12.8.2"),sQuery(id+"F0.wireOp",EDGE,"E5.3.8.3"),sQuery(id+"F0.wireOp",EDGE,"E5.6.8.3"),sQuery(id+"F0.wireOp",EDGE,"E5.9.8.3"),sQuery(id+"F0.wireOp",EDGE,"E5.12.8.3"),sQuery(id+"F0.wireOp",EDGE,"E5.3.8.4"),sQuery(id+"F0.wireOp",EDGE,"E5.6.8.4"),sQuery(id+"F0.wireOp",EDGE,"E5.9.8.4"),sQuery(id+"F0.wireOp",EDGE,"E5.12.8.4"),sQuery(id+"F0.wireOp",EDGE,"E5.3.8.5"),sQuery(id+"F0.wireOp",EDGE,"E5.6.8.5"),sQuery(id+"F0.wireOp",EDGE,"E5.9.8.5"),sQuery(id+"F0.wireOp",EDGE,"E5.12.8.5"),sQuery(id+"F0.wireOp",EDGE,"E5.3.9.1"),sQuery(id+"F0.wireOp",EDGE,"E5.6.9.1"),sQuery(id+"F0.wireOp",EDGE,"E5.9.9.1"),sQuery(id+"F0.wireOp",EDGE,"E5.12.9.1"),sQuery(id+"F0.wireOp",EDGE,"E5.3.9.2"),sQuery(id+"F0.wireOp",EDGE,"E5.6.9.2"),sQuery(id+"F0.wireOp",EDGE,"E5.9.9.2"),sQuery(id+"F0.wireOp",EDGE,"E5.12.9.2"),sQuery(id+"F0.wireOp",EDGE,"E5.3.9.3"),sQuery(id+"F0.wireOp",EDGE,"E5.6.9.3"),sQuery(id+"F0.wireOp",EDGE,"E5.9.9.3"),sQuery(id+"F0.wireOp",EDGE,"E5.12.9.3"),sQuery(id+"F0.wireOp",EDGE,"E5.3.9.4"),sQuery(id+"F0.wireOp",EDGE,"E5.6.9.4"),sQuery(id+"F0.wireOp",EDGE,"E5.9.9.4"),sQuery(id+"F0.wireOp",EDGE,"E5.12.9.4"),sQuery(id+"F0.wireOp",EDGE,"E5.3.9.5"),sQuery(id+"F0.wireOp",EDGE,"E5.6.9.5"),sQuery(id+"F0.wireOp",EDGE,"E5.9.9.5"),sQuery(id+"F0.wireOp",EDGE,"E5.12.9.5"),sQuery(id+"F0.wireOp",EDGE,"E5.3.10.1"),sQuery(id+"F0.wireOp",EDGE,"E5.6.10.1"),sQuery(id+"F0.wireOp",EDGE,"E5.9.10.1"),sQuery(id+"F0.wireOp",EDGE,"E5.12.10.1"),sQuery(id+"F0.wireOp",EDGE,"E5.3.10.2"),sQuery(id+"F0.wireOp",EDGE,"E5.6.10.2"),sQuery(id+"F0.wireOp",EDGE,"E5.9.10.2"),sQuery(id+"F0.wireOp",EDGE,"E5.12.10.2"),sQuery(id+"F0.wireOp",EDGE,"E5.3.10.3"),sQuery(id+"F0.wireOp",EDGE,"E5.6.10.3"),sQuery(id+"F0.wireOp",EDGE,"E5.9.10.3"),sQuery(id+"F0.wireOp",EDGE,"E5.12.10.3"),sQuery(id+"F0.wireOp",EDGE,"E5.3.10.4"),sQuery(id+"F0.wireOp",EDGE,"E5.6.10.4"),sQuery(id+"F0.wireOp",EDGE,"E5.9.10.4"),sQuery(id+"F0.wireOp",EDGE,"E5.12.10.4"),sQuery(id+"F0.wireOp",EDGE,"E5.3.10.5"),sQuery(id+"F0.wireOp",EDGE,"E5.6.10.5"),sQuery(id+"F0.wireOp",EDGE,"E5.9.10.5"),sQuery(id+"F0.wireOp",EDGE,"E5.12.10.5"),sQuery(id+"F0.wireOp",EDGE,"E5.3.11.1"),sQuery(id+"F0.wireOp",EDGE,"E5.6.11.1"),sQuery(id+"F0.wireOp",EDGE,"E5.9.11.1"),sQuery(id+"F0.wireOp",EDGE,"E5.12.11.1"),sQuery(id+"F0.wireOp",EDGE,"E5.3.11.2"),sQuery(id+"F0.wireOp",EDGE,"E5.6.11.2"),sQuery(id+"F0.wireOp",EDGE,"E5.9.11.2"),sQuery(id+"F0.wireOp",EDGE,"E5.12.11.2"),sQuery(id+"F0.wireOp",EDGE,"E5.3.11.3"),sQuery(id+"F0.wireOp",EDGE,"E5.6.11.3"),sQuery(id+"F0.wireOp",EDGE,"E5.9.11.3"),sQuery(id+"F0.wireOp",EDGE,"E5.12.11.3"),sQuery(id+"F0.wireOp",EDGE,"E5.3.11.4"),sQuery(id+"F0.wireOp",EDGE,"E5.6.11.4"),sQuery(id+"F0.wireOp",EDGE,"E5.9.11.4"),sQuery(id+"F0.wireOp",EDGE,"E5.12.11.4"),sQuery(id+"F0.wireOp",EDGE,"E5.3.11.5"),sQuery(id+"F0.wireOp",EDGE,"E5.6.11.5"),sQuery(id+"F0.wireOp",EDGE,"E5.9.11.5"),sQuery(id+"F0.wireOp",EDGE,"E5.12.11.5"),sQuery(id+"F0.wireOp",EDGE,"E6.bottom"),sQuery(id+"F0.wireOp",EDGE,"E6.top"),sQuery(id+"F0.wireOp",EDGE,"E6.left"),sQuery(id+"F0.wireOp",EDGE,"E6.right"),sQuery(id+"F0.wireOp",EDGE,"E7.0.1.0"),sQuery(id+"F0.wireOp",EDGE,"E7.0.1.1"),sQuery(id+"F0.wireOp",EDGE,"E7.0.1.2"),sQuery(id+"F0.wireOp",EDGE,"E7.0.1.3"),sQuery(id+"F0.wireOp",EDGE,"E7.0.2.0"),sQuery(id+"F0.wireOp",EDGE,"E7.0.2.1"),sQuery(id+"F0.wireOp",EDGE,"E7.0.2.2"),sQuery(id+"F0.wireOp",EDGE,"E7.0.2.3"),sQuery(id+"F0.wireOp",EDGE,"E7.0.3.0"),sQuery(id+"F0.wireOp",EDGE,"E7.0.3.1"),sQuery(id+"F0.wireOp",EDGE,"E7.0.3.2"),sQuery(id+"F0.wireOp",EDGE,"E7.0.3.3"),sQuery(id+"F0.wireOp",EDGE,"E7.0.4.0"),sQuery(id+"F0.wireOp",EDGE,"E7.0.4.1"),sQuery(id+"F0.wireOp",EDGE,"E7.0.4.2"),sQuery(id+"F0.wireOp",EDGE,"E7.0.4.3"),sQuery(id+"F0.wireOp",EDGE,"E7.0.5.0"),sQuery(id+"F0.wireOp",EDGE,"E7.0.5.1"),sQuery(id+"F0.wireOp",EDGE,"E7.0.5.2"),sQuery(id+"F0.wireOp",EDGE,"E7.0.5.3"),sQuery(id+"F0.wireOp",EDGE,"E7.1.0.0"),sQuery(id+"F0.wireOp",EDGE,"E7.1.0.1"),sQuery(id+"F0.wireOp",EDGE,"E7.1.0.2"),sQuery(id+"F0.wireOp",EDGE,"E7.1.0.3"),sQuery(id+"F0.wireOp",EDGE,"E7.1.1.0"),sQuery(id+"F0.wireOp",EDGE,"E7.1.1.1"),sQuery(id+"F0.wireOp",EDGE,"E7.1.1.2"),sQuery(id+"F0.wireOp",EDGE,"E7.1.1.3"),sQuery(id+"F0.wireOp",EDGE,"E7.1.2.0"),sQuery(id+"F0.wireOp",EDGE,"E7.1.2.1"),sQuery(id+"F0.wireOp",EDGE,"E7.1.2.2"),sQuery(id+"F0.wireOp",EDGE,"E7.1.2.3"),sQuery(id+"F0.wireOp",EDGE,"E7.1.3.0"),sQuery(id+"F0.wireOp",EDGE,"E7.1.3.1"),sQuery(id+"F0.wireOp",EDGE,"E7.1.3.2"),sQuery(id+"F0.wireOp",EDGE,"E7.1.3.3"),sQuery(id+"F0.wireOp",EDGE,"E7.1.4.0"),sQuery(id+"F0.wireOp",EDGE,"E7.1.4.1"),sQuery(id+"F0.wireOp",EDGE,"E7.1.4.2"),sQuery(id+"F0.wireOp",EDGE,"E7.1.4.3"),sQuery(id+"F0.wireOp",EDGE,"E7.1.5.0"),sQuery(id+"F0.wireOp",EDGE,"E7.1.5.1"),sQuery(id+"F0.wireOp",EDGE,"E7.1.5.2"),sQuery(id+"F0.wireOp",EDGE,"E7.1.5.3"),sQuery(id+"F0.wireOp",EDGE,"E7.2.0.0"),sQuery(id+"F0.wireOp",EDGE,"E7.2.0.1"),sQuery(id+"F0.wireOp",EDGE,"E7.2.0.2"),sQuery(id+"F0.wireOp",EDGE,"E7.2.0.3"),sQuery(id+"F0.wireOp",EDGE,"E7.2.1.0"),sQuery(id+"F0.wireOp",EDGE,"E7.2.1.1"),sQuery(id+"F0.wireOp",EDGE,"E7.2.1.2"),sQuery(id+"F0.wireOp",EDGE,"E7.2.1.3"),sQuery(id+"F0.wireOp",EDGE,"E7.2.2.0"),sQuery(id+"F0.wireOp",EDGE,"E7.2.2.1"),sQuery(id+"F0.wireOp",EDGE,"E7.2.2.2"),sQuery(id+"F0.wireOp",EDGE,"E7.2.2.3"),sQuery(id+"F0.wireOp",EDGE,"E7.2.3.0"),sQuery(id+"F0.wireOp",EDGE,"E7.2.3.1"),sQuery(id+"F0.wireOp",EDGE,"E7.2.3.2"),sQuery(id+"F0.wireOp",EDGE,"E7.2.3.3"),sQuery(id+"F0.wireOp",EDGE,"E7.2.4.0"),sQuery(id+"F0.wireOp",EDGE,"E7.2.4.1"),sQuery(id+"F0.wireOp",EDGE,"E7.2.4.2"),sQuery(id+"F0.wireOp",EDGE,"E7.2.4.3"),sQuery(id+"F0.wireOp",EDGE,"E7.2.5.0"),sQuery(id+"F0.wireOp",EDGE,"E7.2.5.1"),sQuery(id+"F0.wireOp",EDGE,"E7.2.5.2"),sQuery(id+"F0.wireOp",EDGE,"E7.2.5.3"),sQuery(id+"F0.wireOp",EDGE,"E7.3.0.0"),sQuery(id+"F0.wireOp",EDGE,"E7.3.0.1"),sQuery(id+"F0.wireOp",EDGE,"E7.3.0.2"),sQuery(id+"F0.wireOp",EDGE,"E7.3.0.3"),sQuery(id+"F0.wireOp",EDGE,"E7.3.1.0"),sQuery(id+"F0.wireOp",EDGE,"E7.3.1.1"),sQuery(id+"F0.wireOp",EDGE,"E7.3.1.2"),sQuery(id+"F0.wireOp",EDGE,"E7.3.1.3"),sQuery(id+"F0.wireOp",EDGE,"E7.3.2.0"),sQuery(id+"F0.wireOp",EDGE,"E7.3.2.1"),sQuery(id+"F0.wireOp",EDGE,"E7.3.2.2"),sQuery(id+"F0.wireOp",EDGE,"E7.3.2.3"),sQuery(id+"F0.wireOp",EDGE,"E7.3.3.0"),sQuery(id+"F0.wireOp",EDGE,"E7.3.3.1"),sQuery(id+"F0.wireOp",EDGE,"E7.3.3.2"),sQuery(id+"F0.wireOp",EDGE,"E7.3.3.3"),sQuery(id+"F0.wireOp",EDGE,"E7.3.4.0"),sQuery(id+"F0.wireOp",EDGE,"E7.3.4.1"),sQuery(id+"F0.wireOp",EDGE,"E7.3.4.2"),sQuery(id+"F0.wireOp",EDGE,"E7.3.4.3"),sQuery(id+"F0.wireOp",EDGE,"E7.3.5.0"),sQuery(id+"F0.wireOp",EDGE,"E7.3.5.1"),sQuery(id+"F0.wireOp",EDGE,"E7.3.5.2"),sQuery(id+"F0.wireOp",EDGE,"E7.3.5.3"),sQuery(id+"F0.wireOp",EDGE,"E7.4.0.0"),sQuery(id+"F0.wireOp",EDGE,"E7.4.0.1"),sQuery(id+"F0.wireOp",EDGE,"E7.4.0.2"),sQuery(id+"F0.wireOp",EDGE,"E7.4.0.3"),sQuery(id+"F0.wireOp",EDGE,"E7.4.1.0"),sQuery(id+"F0.wireOp",EDGE,"E7.4.1.1"),sQuery(id+"F0.wireOp",EDGE,"E7.4.1.2"),sQuery(id+"F0.wireOp",EDGE,"E7.4.1.3"),sQuery(id+"F0.wireOp",EDGE,"E7.4.2.0"),sQuery(id+"F0.wireOp",EDGE,"E7.4.2.1"),sQuery(id+"F0.wireOp",EDGE,"E7.4.2.2"),sQuery(id+"F0.wireOp",EDGE,"E7.4.2.3"),sQuery(id+"F0.wireOp",EDGE,"E7.4.3.0"),sQuery(id+"F0.wireOp",EDGE,"E7.4.3.1"),sQuery(id+"F0.wireOp",EDGE,"E7.4.3.2"),sQuery(id+"F0.wireOp",EDGE,"E7.4.3.3"),sQuery(id+"F0.wireOp",EDGE,"E7.4.4.0"),sQuery(id+"F0.wireOp",EDGE,"E7.4.4.1"),sQuery(id+"F0.wireOp",EDGE,"E7.4.4.2"),sQuery(id+"F0.wireOp",EDGE,"E7.4.4.3"),sQuery(id+"F0.wireOp",EDGE,"E7.4.5.0"),sQuery(id+"F0.wireOp",EDGE,"E7.4.5.1"),sQuery(id+"F0.wireOp",EDGE,"E7.4.5.2"),sQuery(id+"F0.wireOp",EDGE,"E7.4.5.3"),sQuery(id+"F0.wireOp",EDGE,"E7.5.0.0"),sQuery(id+"F0.wireOp",EDGE,"E7.5.0.1"),sQuery(id+"F0.wireOp",EDGE,"E7.5.0.2"),sQuery(id+"F0.wireOp",EDGE,"E7.5.0.3"),sQuery(id+"F0.wireOp",EDGE,"E7.5.1.0"),sQuery(id+"F0.wireOp",EDGE,"E7.5.1.1"),sQuery(id+"F0.wireOp",EDGE,"E7.5.1.2"),sQuery(id+"F0.wireOp",EDGE,"E7.5.1.3"),sQuery(id+"F0.wireOp",EDGE,"E7.5.2.0"),sQuery(id+"F0.wireOp",EDGE,"E7.5.2.1"),sQuery(id+"F0.wireOp",EDGE,"E7.5.2.2"),sQuery(id+"F0.wireOp",EDGE,"E7.5.2.3"),sQuery(id+"F0.wireOp",EDGE,"E7.5.3.0"),sQuery(id+"F0.wireOp",EDGE,"E7.5.3.1"),sQuery(id+"F0.wireOp",EDGE,"E7.5.3.2"),sQuery(id+"F0.wireOp",EDGE,"E7.5.3.3"),sQuery(id+"F0.wireOp",EDGE,"E7.5.4.0"),sQuery(id+"F0.wireOp",EDGE,"E7.5.4.1"),sQuery(id+"F0.wireOp",EDGE,"E7.5.4.2"),sQuery(id+"F0.wireOp",EDGE,"E7.5.4.3"),sQuery(id+"F0.wireOp",EDGE,"E7.5.5.0"),sQuery(id+"F0.wireOp",EDGE,"E7.5.5.1"),sQuery(id+"F0.wireOp",EDGE,"E7.5.5.2"),sQuery(id+"F0.wireOp",EDGE,"E7.5.5.3"),sQuery(id+"F0.wireOp",EDGE,"E7.6.0.0"),sQuery(id+"F0.wireOp",EDGE,"E7.6.0.1"),sQuery(id+"F0.wireOp",EDGE,"E7.6.0.2"),sQuery(id+"F0.wireOp",EDGE,"E7.6.0.3"),sQuery(id+"F0.wireOp",EDGE,"E7.6.1.0"),sQuery(id+"F0.wireOp",EDGE,"E7.6.1.1"),sQuery(id+"F0.wireOp",EDGE,"E7.6.1.2"),sQuery(id+"F0.wireOp",EDGE,"E7.6.1.3"),sQuery(id+"F0.wireOp",EDGE,"E7.6.2.0"),sQuery(id+"F0.wireOp",EDGE,"E7.6.2.1"),sQuery(id+"F0.wireOp",EDGE,"E7.6.2.2"),sQuery(id+"F0.wireOp",EDGE,"E7.6.2.3"),sQuery(id+"F0.wireOp",EDGE,"E7.6.3.0"),sQuery(id+"F0.wireOp",EDGE,"E7.6.3.1"),sQuery(id+"F0.wireOp",EDGE,"E7.6.3.2"),sQuery(id+"F0.wireOp",EDGE,"E7.6.3.3"),sQuery(id+"F0.wireOp",EDGE,"E7.6.4.0"),sQuery(id+"F0.wireOp",EDGE,"E7.6.4.1"),sQuery(id+"F0.wireOp",EDGE,"E7.6.4.2"),sQuery(id+"F0.wireOp",EDGE,"E7.6.4.3"),sQuery(id+"F0.wireOp",EDGE,"E7.6.5.0"),sQuery(id+"F0.wireOp",EDGE,"E7.6.5.1"),sQuery(id+"F0.wireOp",EDGE,"E7.6.5.2"),sQuery(id+"F0.wireOp",EDGE,"E7.6.5.3"),sQuery(id+"F0.wireOp",EDGE,"E7.7.0.0"),sQuery(id+"F0.wireOp",EDGE,"E7.7.0.1"),sQuery(id+"F0.wireOp",EDGE,"E7.7.0.2"),sQuery(id+"F0.wireOp",EDGE,"E7.7.0.3"),sQuery(id+"F0.wireOp",EDGE,"E7.7.1.0"),sQuery(id+"F0.wireOp",EDGE,"E7.7.1.1"),sQuery(id+"F0.wireOp",EDGE,"E7.7.1.2"),sQuery(id+"F0.wireOp",EDGE,"E7.7.1.3"),sQuery(id+"F0.wireOp",EDGE,"E7.7.2.0"),sQuery(id+"F0.wireOp",EDGE,"E7.7.2.1"),sQuery(id+"F0.wireOp",EDGE,"E7.7.2.2"),sQuery(id+"F0.wireOp",EDGE,"E7.7.2.3"),sQuery(id+"F0.wireOp",EDGE,"E7.7.3.0"),sQuery(id+"F0.wireOp",EDGE,"E7.7.3.1"),sQuery(id+"F0.wireOp",EDGE,"E7.7.3.2"),sQuery(id+"F0.wireOp",EDGE,"E7.7.3.3"),sQuery(id+"F0.wireOp",EDGE,"E7.7.4.0"),sQuery(id+"F0.wireOp",EDGE,"E7.7.4.1"),sQuery(id+"F0.wireOp",EDGE,"E7.7.4.2"),sQuery(id+"F0.wireOp",EDGE,"E7.7.4.3"),sQuery(id+"F0.wireOp",EDGE,"E7.7.5.0"),sQuery(id+"F0.wireOp",EDGE,"E7.7.5.1"),sQuery(id+"F0.wireOp",EDGE,"E7.7.5.2"),sQuery(id+"F0.wireOp",EDGE,"E7.7.5.3"),sQuery(id+"F0.wireOp",EDGE,"E7.8.0.0"),sQuery(id+"F0.wireOp",EDGE,"E7.8.0.1"),sQuery(id+"F0.wireOp",EDGE,"E7.8.0.2"),sQuery(id+"F0.wireOp",EDGE,"E7.8.0.3"),sQuery(id+"F0.wireOp",EDGE,"E7.8.1.0"),sQuery(id+"F0.wireOp",EDGE,"E7.8.1.1"),sQuery(id+"F0.wireOp",EDGE,"E7.8.1.2"),sQuery(id+"F0.wireOp",EDGE,"E7.8.1.3"),sQuery(id+"F0.wireOp",EDGE,"E7.8.2.0"),sQuery(id+"F0.wireOp",EDGE,"E7.8.2.1"),sQuery(id+"F0.wireOp",EDGE,"E7.8.2.2"),sQuery(id+"F0.wireOp",EDGE,"E7.8.2.3"),sQuery(id+"F0.wireOp",EDGE,"E7.8.3.0"),sQuery(id+"F0.wireOp",EDGE,"E7.8.3.1"),sQuery(id+"F0.wireOp",EDGE,"E7.8.3.2"),sQuery(id+"F0.wireOp",EDGE,"E7.8.3.3"),sQuery(id+"F0.wireOp",EDGE,"E7.8.4.0"),sQuery(id+"F0.wireOp",EDGE,"E7.8.4.1"),sQuery(id+"F0.wireOp",EDGE,"E7.8.4.2"),sQuery(id+"F0.wireOp",EDGE,"E7.8.4.3"),sQuery(id+"F0.wireOp",EDGE,"E7.8.5.0"),sQuery(id+"F0.wireOp",EDGE,"E7.8.5.1"),sQuery(id+"F0.wireOp",EDGE,"E7.8.5.2"),sQuery(id+"F0.wireOp",EDGE,"E7.8.5.3"),sQuery(id+"F0.wireOp",EDGE,"E7.9.0.0"),sQuery(id+"F0.wireOp",EDGE,"E7.9.0.1"),sQuery(id+"F0.wireOp",EDGE,"E7.9.0.2"),sQuery(id+"F0.wireOp",EDGE,"E7.9.0.3"),sQuery(id+"F0.wireOp",EDGE,"E7.9.1.0"),sQuery(id+"F0.wireOp",EDGE,"E7.9.1.1"),sQuery(id+"F0.wireOp",EDGE,"E7.9.1.2"),sQuery(id+"F0.wireOp",EDGE,"E7.9.1.3"),sQuery(id+"F0.wireOp",EDGE,"E7.9.2.0"),sQuery(id+"F0.wireOp",EDGE,"E7.9.2.1"),sQuery(id+"F0.wireOp",EDGE,"E7.9.2.2"),sQuery(id+"F0.wireOp",EDGE,"E7.9.2.3"),sQuery(id+"F0.wireOp",EDGE,"E7.9.3.0"),sQuery(id+"F0.wireOp",EDGE,"E7.9.3.1"),sQuery(id+"F0.wireOp",EDGE,"E7.9.3.2"),sQuery(id+"F0.wireOp",EDGE,"E7.9.3.3"),sQuery(id+"F0.wireOp",EDGE,"E7.9.4.0"),sQuery(id+"F0.wireOp",EDGE,"E7.9.4.1"),sQuery(id+"F0.wireOp",EDGE,"E7.9.4.2"),sQuery(id+"F0.wireOp",EDGE,"E7.9.4.3"),sQuery(id+"F0.wireOp",EDGE,"E7.9.5.0"),sQuery(id+"F0.wireOp",EDGE,"E7.9.5.1"),sQuery(id+"F0.wireOp",EDGE,"E7.9.5.2"),sQuery(id+"F0.wireOp",EDGE,"E7.9.5.3"),sQuery(id+"F0.wireOp",EDGE,"E7.10.0.0"),sQuery(id+"F0.wireOp",EDGE,"E7.10.0.1"),sQuery(id+"F0.wireOp",EDGE,"E7.10.0.2"),sQuery(id+"F0.wireOp",EDGE,"E7.10.0.3"),sQuery(id+"F0.wireOp",EDGE,"E7.10.1.0"),sQuery(id+"F0.wireOp",EDGE,"E7.10.1.1"),sQuery(id+"F0.wireOp",EDGE,"E7.10.1.2"),sQuery(id+"F0.wireOp",EDGE,"E7.10.1.3"),sQuery(id+"F0.wireOp",EDGE,"E7.10.2.0"),sQuery(id+"F0.wireOp",EDGE,"E7.10.2.1"),sQuery(id+"F0.wireOp",EDGE,"E7.10.2.2"),sQuery(id+"F0.wireOp",EDGE,"E7.10.2.3"),sQuery(id+"F0.wireOp",EDGE,"E7.10.3.0"),sQuery(id+"F0.wireOp",EDGE,"E7.10.3.1"),sQuery(id+"F0.wireOp",EDGE,"E7.10.3.2"),sQuery(id+"F0.wireOp",EDGE,"E7.10.3.3"),sQuery(id+"F0.wireOp",EDGE,"E7.10.4.0"),sQuery(id+"F0.wireOp",EDGE,"E7.10.4.1"),sQuery(id+"F0.wireOp",EDGE,"E7.10.4.2"),sQuery(id+"F0.wireOp",EDGE,"E7.10.4.3"),sQuery(id+"F0.wireOp",EDGE,"E7.10.5.0"),sQuery(id+"F0.wireOp",EDGE,"E7.10.5.1"),sQuery(id+"F0.wireOp",EDGE,"E7.10.5.2"),sQuery(id+"F0.wireOp",EDGE,"E7.10.5.3"),sQuery(id+"F0.wireOp",EDGE,"E7.11.0.0"),sQuery(id+"F0.wireOp",EDGE,"E7.11.0.1"),sQuery(id+"F0.wireOp",EDGE,"E7.11.0.2"),sQuery(id+"F0.wireOp",EDGE,"E7.11.0.3"),sQuery(id+"F0.wireOp",EDGE,"E7.11.1.0"),sQuery(id+"F0.wireOp",EDGE,"E7.11.1.1"),sQuery(id+"F0.wireOp",EDGE,"E7.11.1.2"),sQuery(id+"F0.wireOp",EDGE,"E7.11.1.3"),sQuery(id+"F0.wireOp",EDGE,"E7.11.2.0"),sQuery(id+"F0.wireOp",EDGE,"E7.11.2.1"),sQuery(id+"F0.wireOp",EDGE,"E7.11.2.2"),sQuery(id+"F0.wireOp",EDGE,"E7.11.2.3"),sQuery(id+"F0.wireOp",EDGE,"E7.11.3.0"),sQuery(id+"F0.wireOp",EDGE,"E7.11.3.1"),sQuery(id+"F0.wireOp",EDGE,"E7.11.3.2"),sQuery(id+"F0.wireOp",EDGE,"E7.11.3.3"),sQuery(id+"F0.wireOp",EDGE,"E7.11.4.0"),sQuery(id+"F0.wireOp",EDGE,"E7.11.4.1"),sQuery(id+"F0.wireOp",EDGE,"E7.11.4.2"),sQuery(id+"F0.wireOp",EDGE,"E7.11.4.3"),sQuery(id+"F0.wireOp",EDGE,"E7.11.5.0"),sQuery(id+"F0.wireOp",EDGE,"E7.11.5.1"),sQuery(id+"F0.wireOp",EDGE,"E7.11.5.2"),sQuery(id+"F0.wireOp",EDGE,"E7.11.5.3")])],"isStart":false});
            var Q1;
            Q1=makeQuery(id+"F1.opExtrude","CAP_FACE",FACE,{"disambiguationData":[OSD([sQuery(id+"F0.wireOp",EDGE,"E0.bottom"),sQuery(id+"F0.wireOp",EDGE,"E0.top"),sQuery(id+"F0.wireOp",EDGE,"E0.left"),sQuery(id+"F0.wireOp",EDGE,"E0.right"),sQuery(id+"F0.wireOp",EDGE,"E1.bottom"),sQuery(id+"F0.wireOp",EDGE,"E1.top"),sQuery(id+"F0.wireOp",EDGE,"E1.left"),sQuery(id+"F0.wireOp",EDGE,"E1.right"),sQuery(id+"F0.wireOp",EDGE,"E4.3.1.0"),sQuery(id+"F0.wireOp",EDGE,"E4.6.1.0"),sQuery(id+"F0.wireOp",EDGE,"E4.9.1.0"),sQuery(id+"F0.wireOp",EDGE,"E4.12.1.0"),sQuery(id+"F0.wireOp",EDGE,"E4.3.2.0"),sQuery(id+"F0.wireOp",EDGE,"E4.6.2.0"),sQuery(id+"F0.wireOp",EDGE,"E4.9.2.0"),sQuery(id+"F0.wireOp",EDGE,"E4.12.2.0"),sQuery(id+"F0.wireOp",EDGE,"E4.3.3.0"),sQuery(id+"F0.wireOp",EDGE,"E4.6.3.0"),sQuery(id+"F0.wireOp",EDGE,"E4.9.3.0"),sQuery(id+"F0.wireOp",EDGE,"E4.12.3.0"),sQuery(id+"F0.wireOp",EDGE,"E4.3.4.0"),sQuery(id+"F0.wireOp",EDGE,"E4.6.4.0"),sQuery(id+"F0.wireOp",EDGE,"E4.9.4.0"),sQuery(id+"F0.wireOp",EDGE,"E4.12.4.0"),sQuery(id+"F0.wireOp",EDGE,"E4.3.5.0"),sQuery(id+"F0.wireOp",EDGE,"E4.6.5.0"),sQuery(id+"F0.wireOp",EDGE,"E4.9.5.0"),sQuery(id+"F0.wireOp",EDGE,"E4.12.5.0"),sQuery(id+"F0.wireOp",EDGE,"E4.3.6.0"),sQuery(id+"F0.wireOp",EDGE,"E4.6.6.0"),sQuery(id+"F0.wireOp",EDGE,"E4.9.6.0"),sQuery(id+"F0.wireOp",EDGE,"E4.12.6.0"),sQuery(id+"F0.wireOp",EDGE,"E4.3.7.0"),sQuery(id+"F0.wireOp",EDGE,"E4.6.7.0"),sQuery(id+"F0.wireOp",EDGE,"E4.9.7.0"),sQuery(id+"F0.wireOp",EDGE,"E4.12.7.0"),sQuery(id+"F0.wireOp",EDGE,"E4.3.8.0"),sQuery(id+"F0.wireOp",EDGE,"E4.6.8.0"),sQuery(id+"F0.wireOp",EDGE,"E4.9.8.0"),sQuery(id+"F0.wireOp",EDGE,"E4.12.8.0"),sQuery(id+"F0.wireOp",EDGE,"E4.3.9.0"),sQuery(id+"F0.wireOp",EDGE,"E4.6.9.0"),sQuery(id+"F0.wireOp",EDGE,"E4.9.9.0"),sQuery(id+"F0.wireOp",EDGE,"E4.12.9.0"),sQuery(id+"F0.wireOp",EDGE,"E4.3.10.0"),sQuery(id+"F0.wireOp",EDGE,"E4.6.10.0"),sQuery(id+"F0.wireOp",EDGE,"E4.9.10.0"),sQuery(id+"F0.wireOp",EDGE,"E4.12.10.0"),sQuery(id+"F0.wireOp",EDGE,"E4.3.11.0"),sQuery(id+"F0.wireOp",EDGE,"E4.6.11.0"),sQuery(id+"F0.wireOp",EDGE,"E4.9.11.0"),sQuery(id+"F0.wireOp",EDGE,"E4.12.11.0"),sQuery(id+"F0.wireOp",EDGE,"E5.3.0.1"),sQuery(id+"F0.wireOp",EDGE,"E5.6.0.1"),sQuery(id+"F0.wireOp",EDGE,"E5.9.0.1"),sQuery(id+"F0.wireOp",EDGE,"E5.12.0.1"),sQuery(id+"F0.wireOp",EDGE,"E5.3.0.2"),sQuery(id+"F0.wireOp",EDGE,"E5.6.0.2"),sQuery(id+"F0.wireOp",EDGE,"E5.9.0.2"),sQuery(id+"F0.wireOp",EDGE,"E5.12.0.2"),sQuery(id+"F0.wireOp",EDGE,"E5.3.0.3"),sQuery(id+"F0.wireOp",EDGE,"E5.6.0.3"),sQuery(id+"F0.wireOp",EDGE,"E5.9.0.3"),sQuery(id+"F0.wireOp",EDGE,"E5.12.0.3"),sQuery(id+"F0.wireOp",EDGE,"E5.3.0.4"),sQuery(id+"F0.wireOp",EDGE,"E5.6.0.4"),sQuery(id+"F0.wireOp",EDGE,"E5.9.0.4"),sQuery(id+"F0.wireOp",EDGE,"E5.12.0.4"),sQuery(id+"F0.wireOp",EDGE,"E5.3.0.5"),sQuery(id+"F0.wireOp",EDGE,"E5.6.0.5"),sQuery(id+"F0.wireOp",EDGE,"E5.9.0.5"),sQuery(id+"F0.wireOp",EDGE,"E5.12.0.5"),sQuery(id+"F0.wireOp",EDGE,"E5.3.1.1"),sQuery(id+"F0.wireOp",EDGE,"E5.6.1.1"),sQuery(id+"F0.wireOp",EDGE,"E5.9.1.1"),sQuery(id+"F0.wireOp",EDGE,"E5.12.1.1"),sQuery(id+"F0.wireOp",EDGE,"E5.3.1.2"),sQuery(id+"F0.wireOp",EDGE,"E5.6.1.2"),sQuery(id+"F0.wireOp",EDGE,"E5.9.1.2"),sQuery(id+"F0.wireOp",EDGE,"E5.12.1.2"),sQuery(id+"F0.wireOp",EDGE,"E5.3.1.3"),sQuery(id+"F0.wireOp",EDGE,"E5.6.1.3"),sQuery(id+"F0.wireOp",EDGE,"E5.9.1.3"),sQuery(id+"F0.wireOp",EDGE,"E5.12.1.3"),sQuery(id+"F0.wireOp",EDGE,"E5.3.1.4"),sQuery(id+"F0.wireOp",EDGE,"E5.6.1.4"),sQuery(id+"F0.wireOp",EDGE,"E5.9.1.4"),sQuery(id+"F0.wireOp",EDGE,"E5.12.1.4"),sQuery(id+"F0.wireOp",EDGE,"E5.3.1.5"),sQuery(id+"F0.wireOp",EDGE,"E5.6.1.5"),sQuery(id+"F0.wireOp",EDGE,"E5.9.1.5"),sQuery(id+"F0.wireOp",EDGE,"E5.12.1.5"),sQuery(id+"F0.wireOp",EDGE,"E5.3.2.1"),sQuery(id+"F0.wireOp",EDGE,"E5.6.2.1"),sQuery(id+"F0.wireOp",EDGE,"E5.9.2.1"),sQuery(id+"F0.wireOp",EDGE,"E5.12.2.1"),sQuery(id+"F0.wireOp",EDGE,"E5.3.2.2"),sQuery(id+"F0.wireOp",EDGE,"E5.6.2.2"),sQuery(id+"F0.wireOp",EDGE,"E5.9.2.2"),sQuery(id+"F0.wireOp",EDGE,"E5.12.2.2"),sQuery(id+"F0.wireOp",EDGE,"E5.3.2.3"),sQuery(id+"F0.wireOp",EDGE,"E5.6.2.3"),sQuery(id+"F0.wireOp",EDGE,"E5.9.2.3"),sQuery(id+"F0.wireOp",EDGE,"E5.12.2.3"),sQuery(id+"F0.wireOp",EDGE,"E5.3.2.4"),sQuery(id+"F0.wireOp",EDGE,"E5.6.2.4"),sQuery(id+"F0.wireOp",EDGE,"E5.9.2.4"),sQuery(id+"F0.wireOp",EDGE,"E5.12.2.4"),sQuery(id+"F0.wireOp",EDGE,"E5.3.2.5"),sQuery(id+"F0.wireOp",EDGE,"E5.6.2.5"),sQuery(id+"F0.wireOp",EDGE,"E5.9.2.5"),sQuery(id+"F0.wireOp",EDGE,"E5.12.2.5"),sQuery(id+"F0.wireOp",EDGE,"E5.3.3.1"),sQuery(id+"F0.wireOp",EDGE,"E5.6.3.1"),sQuery(id+"F0.wireOp",EDGE,"E5.9.3.1"),sQuery(id+"F0.wireOp",EDGE,"E5.12.3.1"),sQuery(id+"F0.wireOp",EDGE,"E5.3.3.2"),sQuery(id+"F0.wireOp",EDGE,"E5.6.3.2"),sQuery(id+"F0.wireOp",EDGE,"E5.9.3.2"),sQuery(id+"F0.wireOp",EDGE,"E5.12.3.2"),sQuery(id+"F0.wireOp",EDGE,"E5.3.3.3"),sQuery(id+"F0.wireOp",EDGE,"E5.6.3.3"),sQuery(id+"F0.wireOp",EDGE,"E5.9.3.3"),sQuery(id+"F0.wireOp",EDGE,"E5.12.3.3"),sQuery(id+"F0.wireOp",EDGE,"E5.3.3.4"),sQuery(id+"F0.wireOp",EDGE,"E5.6.3.4"),sQuery(id+"F0.wireOp",EDGE,"E5.9.3.4"),sQuery(id+"F0.wireOp",EDGE,"E5.12.3.4"),sQuery(id+"F0.wireOp",EDGE,"E5.3.3.5"),sQuery(id+"F0.wireOp",EDGE,"E5.6.3.5"),sQuery(id+"F0.wireOp",EDGE,"E5.9.3.5"),sQuery(id+"F0.wireOp",EDGE,"E5.12.3.5"),sQuery(id+"F0.wireOp",EDGE,"E5.3.4.1"),sQuery(id+"F0.wireOp",EDGE,"E5.6.4.1"),sQuery(id+"F0.wireOp",EDGE,"E5.9.4.1"),sQuery(id+"F0.wireOp",EDGE,"E5.12.4.1"),sQuery(id+"F0.wireOp",EDGE,"E5.3.4.2"),sQuery(id+"F0.wireOp",EDGE,"E5.6.4.2"),sQuery(id+"F0.wireOp",EDGE,"E5.9.4.2"),sQuery(id+"F0.wireOp",EDGE,"E5.12.4.2"),sQuery(id+"F0.wireOp",EDGE,"E5.3.4.3"),sQuery(id+"F0.wireOp",EDGE,"E5.6.4.3"),sQuery(id+"F0.wireOp",EDGE,"E5.9.4.3"),sQuery(id+"F0.wireOp",EDGE,"E5.12.4.3"),sQuery(id+"F0.wireOp",EDGE,"E5.3.4.4"),sQuery(id+"F0.wireOp",EDGE,"E5.6.4.4"),sQuery(id+"F0.wireOp",EDGE,"E5.9.4.4"),sQuery(id+"F0.wireOp",EDGE,"E5.12.4.4"),sQuery(id+"F0.wireOp",EDGE,"E5.3.4.5"),sQuery(id+"F0.wireOp",EDGE,"E5.6.4.5"),sQuery(id+"F0.wireOp",EDGE,"E5.9.4.5"),sQuery(id+"F0.wireOp",EDGE,"E5.12.4.5"),sQuery(id+"F0.wireOp",EDGE,"E5.3.5.1"),sQuery(id+"F0.wireOp",EDGE,"E5.6.5.1"),sQuery(id+"F0.wireOp",EDGE,"E5.9.5.1"),sQuery(id+"F0.wireOp",EDGE,"E5.12.5.1"),sQuery(id+"F0.wireOp",EDGE,"E5.3.5.2"),sQuery(id+"F0.wireOp",EDGE,"E5.6.5.2"),sQuery(id+"F0.wireOp",EDGE,"E5.9.5.2"),sQuery(id+"F0.wireOp",EDGE,"E5.12.5.2"),sQuery(id+"F0.wireOp",EDGE,"E5.3.5.3"),sQuery(id+"F0.wireOp",EDGE,"E5.6.5.3"),sQuery(id+"F0.wireOp",EDGE,"E5.9.5.3"),sQuery(id+"F0.wireOp",EDGE,"E5.12.5.3"),sQuery(id+"F0.wireOp",EDGE,"E5.3.5.4"),sQuery(id+"F0.wireOp",EDGE,"E5.6.5.4"),sQuery(id+"F0.wireOp",EDGE,"E5.9.5.4"),sQuery(id+"F0.wireOp",EDGE,"E5.12.5.4"),sQuery(id+"F0.wireOp",EDGE,"E5.3.5.5"),sQuery(id+"F0.wireOp",EDGE,"E5.6.5.5"),sQuery(id+"F0.wireOp",EDGE,"E5.9.5.5"),sQuery(id+"F0.wireOp",EDGE,"E5.12.5.5"),sQuery(id+"F0.wireOp",EDGE,"E5.3.6.1"),sQuery(id+"F0.wireOp",EDGE,"E5.6.6.1"),sQuery(id+"F0.wireOp",EDGE,"E5.9.6.1"),sQuery(id+"F0.wireOp",EDGE,"E5.12.6.1"),sQuery(id+"F0.wireOp",EDGE,"E5.3.6.2"),sQuery(id+"F0.wireOp",EDGE,"E5.6.6.2"),sQuery(id+"F0.wireOp",EDGE,"E5.9.6.2"),sQuery(id+"F0.wireOp",EDGE,"E5.12.6.2"),sQuery(id+"F0.wireOp",EDGE,"E5.3.6.3"),sQuery(id+"F0.wireOp",EDGE,"E5.6.6.3"),sQuery(id+"F0.wireOp",EDGE,"E5.9.6.3"),sQuery(id+"F0.wireOp",EDGE,"E5.12.6.3"),sQuery(id+"F0.wireOp",EDGE,"E5.3.6.4"),sQuery(id+"F0.wireOp",EDGE,"E5.6.6.4"),sQuery(id+"F0.wireOp",EDGE,"E5.9.6.4"),sQuery(id+"F0.wireOp",EDGE,"E5.12.6.4"),sQuery(id+"F0.wireOp",EDGE,"E5.3.6.5"),sQuery(id+"F0.wireOp",EDGE,"E5.6.6.5"),sQuery(id+"F0.wireOp",EDGE,"E5.9.6.5"),sQuery(id+"F0.wireOp",EDGE,"E5.12.6.5"),sQuery(id+"F0.wireOp",EDGE,"E5.3.7.1"),sQuery(id+"F0.wireOp",EDGE,"E5.6.7.1"),sQuery(id+"F0.wireOp",EDGE,"E5.9.7.1"),sQuery(id+"F0.wireOp",EDGE,"E5.12.7.1"),sQuery(id+"F0.wireOp",EDGE,"E5.3.7.2"),sQuery(id+"F0.wireOp",EDGE,"E5.6.7.2"),sQuery(id+"F0.wireOp",EDGE,"E5.9.7.2"),sQuery(id+"F0.wireOp",EDGE,"E5.12.7.2"),sQuery(id+"F0.wireOp",EDGE,"E5.3.7.3"),sQuery(id+"F0.wireOp",EDGE,"E5.6.7.3"),sQuery(id+"F0.wireOp",EDGE,"E5.9.7.3"),sQuery(id+"F0.wireOp",EDGE,"E5.12.7.3"),sQuery(id+"F0.wireOp",EDGE,"E5.3.7.4"),sQuery(id+"F0.wireOp",EDGE,"E5.6.7.4"),sQuery(id+"F0.wireOp",EDGE,"E5.9.7.4"),sQuery(id+"F0.wireOp",EDGE,"E5.12.7.4"),sQuery(id+"F0.wireOp",EDGE,"E5.3.7.5"),sQuery(id+"F0.wireOp",EDGE,"E5.6.7.5"),sQuery(id+"F0.wireOp",EDGE,"E5.9.7.5"),sQuery(id+"F0.wireOp",EDGE,"E5.12.7.5"),sQuery(id+"F0.wireOp",EDGE,"E5.3.8.1"),sQuery(id+"F0.wireOp",EDGE,"E5.6.8.1"),sQuery(id+"F0.wireOp",EDGE,"E5.9.8.1"),sQuery(id+"F0.wireOp",EDGE,"E5.12.8.1"),sQuery(id+"F0.wireOp",EDGE,"E5.3.8.2"),sQuery(id+"F0.wireOp",EDGE,"E5.6.8.2"),sQuery(id+"F0.wireOp",EDGE,"E5.9.8.2"),sQuery(id+"F0.wireOp",EDGE,"E5.12.8.2"),sQuery(id+"F0.wireOp",EDGE,"E5.3.8.3"),sQuery(id+"F0.wireOp",EDGE,"E5.6.8.3"),sQuery(id+"F0.wireOp",EDGE,"E5.9.8.3"),sQuery(id+"F0.wireOp",EDGE,"E5.12.8.3"),sQuery(id+"F0.wireOp",EDGE,"E5.3.8.4"),sQuery(id+"F0.wireOp",EDGE,"E5.6.8.4"),sQuery(id+"F0.wireOp",EDGE,"E5.9.8.4"),sQuery(id+"F0.wireOp",EDGE,"E5.12.8.4"),sQuery(id+"F0.wireOp",EDGE,"E5.3.8.5"),sQuery(id+"F0.wireOp",EDGE,"E5.6.8.5"),sQuery(id+"F0.wireOp",EDGE,"E5.9.8.5"),sQuery(id+"F0.wireOp",EDGE,"E5.12.8.5"),sQuery(id+"F0.wireOp",EDGE,"E5.3.9.1"),sQuery(id+"F0.wireOp",EDGE,"E5.6.9.1"),sQuery(id+"F0.wireOp",EDGE,"E5.9.9.1"),sQuery(id+"F0.wireOp",EDGE,"E5.12.9.1"),sQuery(id+"F0.wireOp",EDGE,"E5.3.9.2"),sQuery(id+"F0.wireOp",EDGE,"E5.6.9.2"),sQuery(id+"F0.wireOp",EDGE,"E5.9.9.2"),sQuery(id+"F0.wireOp",EDGE,"E5.12.9.2"),sQuery(id+"F0.wireOp",EDGE,"E5.3.9.3"),sQuery(id+"F0.wireOp",EDGE,"E5.6.9.3"),sQuery(id+"F0.wireOp",EDGE,"E5.9.9.3"),sQuery(id+"F0.wireOp",EDGE,"E5.12.9.3"),sQuery(id+"F0.wireOp",EDGE,"E5.3.9.4"),sQuery(id+"F0.wireOp",EDGE,"E5.6.9.4"),sQuery(id+"F0.wireOp",EDGE,"E5.9.9.4"),sQuery(id+"F0.wireOp",EDGE,"E5.12.9.4"),sQuery(id+"F0.wireOp",EDGE,"E5.3.9.5"),sQuery(id+"F0.wireOp",EDGE,"E5.6.9.5"),sQuery(id+"F0.wireOp",EDGE,"E5.9.9.5"),sQuery(id+"F0.wireOp",EDGE,"E5.12.9.5"),sQuery(id+"F0.wireOp",EDGE,"E5.3.10.1"),sQuery(id+"F0.wireOp",EDGE,"E5.6.10.1"),sQuery(id+"F0.wireOp",EDGE,"E5.9.10.1"),sQuery(id+"F0.wireOp",EDGE,"E5.12.10.1"),sQuery(id+"F0.wireOp",EDGE,"E5.3.10.2"),sQuery(id+"F0.wireOp",EDGE,"E5.6.10.2"),sQuery(id+"F0.wireOp",EDGE,"E5.9.10.2"),sQuery(id+"F0.wireOp",EDGE,"E5.12.10.2"),sQuery(id+"F0.wireOp",EDGE,"E5.3.10.3"),sQuery(id+"F0.wireOp",EDGE,"E5.6.10.3"),sQuery(id+"F0.wireOp",EDGE,"E5.9.10.3"),sQuery(id+"F0.wireOp",EDGE,"E5.12.10.3"),sQuery(id+"F0.wireOp",EDGE,"E5.3.10.4"),sQuery(id+"F0.wireOp",EDGE,"E5.6.10.4"),sQuery(id+"F0.wireOp",EDGE,"E5.9.10.4"),sQuery(id+"F0.wireOp",EDGE,"E5.12.10.4"),sQuery(id+"F0.wireOp",EDGE,"E5.3.10.5"),sQuery(id+"F0.wireOp",EDGE,"E5.6.10.5"),sQuery(id+"F0.wireOp",EDGE,"E5.9.10.5"),sQuery(id+"F0.wireOp",EDGE,"E5.12.10.5"),sQuery(id+"F0.wireOp",EDGE,"E5.3.11.1"),sQuery(id+"F0.wireOp",EDGE,"E5.6.11.1"),sQuery(id+"F0.wireOp",EDGE,"E5.9.11.1"),sQuery(id+"F0.wireOp",EDGE,"E5.12.11.1"),sQuery(id+"F0.wireOp",EDGE,"E5.3.11.2"),sQuery(id+"F0.wireOp",EDGE,"E5.6.11.2"),sQuery(id+"F0.wireOp",EDGE,"E5.9.11.2"),sQuery(id+"F0.wireOp",EDGE,"E5.12.11.2"),sQuery(id+"F0.wireOp",EDGE,"E5.3.11.3"),sQuery(id+"F0.wireOp",EDGE,"E5.6.11.3"),sQuery(id+"F0.wireOp",EDGE,"E5.9.11.3"),sQuery(id+"F0.wireOp",EDGE,"E5.12.11.3"),sQuery(id+"F0.wireOp",EDGE,"E5.3.11.4"),sQuery(id+"F0.wireOp",EDGE,"E5.6.11.4"),sQuery(id+"F0.wireOp",EDGE,"E5.9.11.4"),sQuery(id+"F0.wireOp",EDGE,"E5.12.11.4"),sQuery(id+"F0.wireOp",EDGE,"E5.3.11.5"),sQuery(id+"F0.wireOp",EDGE,"E5.6.11.5"),sQuery(id+"F0.wireOp",EDGE,"E5.9.11.5"),sQuery(id+"F0.wireOp",EDGE,"E5.12.11.5"),sQuery(id+"F0.wireOp",EDGE,"E6.bottom"),sQuery(id+"F0.wireOp",EDGE,"E6.top"),sQuery(id+"F0.wireOp",EDGE,"E6.left"),sQuery(id+"F0.wireOp",EDGE,"E6.right"),sQuery(id+"F0.wireOp",EDGE,"E7.0.1.0"),sQuery(id+"F0.wireOp",EDGE,"E7.0.1.1"),sQuery(id+"F0.wireOp",EDGE,"E7.0.1.2"),sQuery(id+"F0.wireOp",EDGE,"E7.0.1.3"),sQuery(id+"F0.wireOp",EDGE,"E7.0.2.0"),sQuery(id+"F0.wireOp",EDGE,"E7.0.2.1"),sQuery(id+"F0.wireOp",EDGE,"E7.0.2.2"),sQuery(id+"F0.wireOp",EDGE,"E7.0.2.3"),sQuery(id+"F0.wireOp",EDGE,"E7.0.3.0"),sQuery(id+"F0.wireOp",EDGE,"E7.0.3.1"),sQuery(id+"F0.wireOp",EDGE,"E7.0.3.2"),sQuery(id+"F0.wireOp",EDGE,"E7.0.3.3"),sQuery(id+"F0.wireOp",EDGE,"E7.0.4.0"),sQuery(id+"F0.wireOp",EDGE,"E7.0.4.1"),sQuery(id+"F0.wireOp",EDGE,"E7.0.4.2"),sQuery(id+"F0.wireOp",EDGE,"E7.0.4.3"),sQuery(id+"F0.wireOp",EDGE,"E7.0.5.0"),sQuery(id+"F0.wireOp",EDGE,"E7.0.5.1"),sQuery(id+"F0.wireOp",EDGE,"E7.0.5.2"),sQuery(id+"F0.wireOp",EDGE,"E7.0.5.3"),sQuery(id+"F0.wireOp",EDGE,"E7.1.0.0"),sQuery(id+"F0.wireOp",EDGE,"E7.1.0.1"),sQuery(id+"F0.wireOp",EDGE,"E7.1.0.2"),sQuery(id+"F0.wireOp",EDGE,"E7.1.0.3"),sQuery(id+"F0.wireOp",EDGE,"E7.1.1.0"),sQuery(id+"F0.wireOp",EDGE,"E7.1.1.1"),sQuery(id+"F0.wireOp",EDGE,"E7.1.1.2"),sQuery(id+"F0.wireOp",EDGE,"E7.1.1.3"),sQuery(id+"F0.wireOp",EDGE,"E7.1.2.0"),sQuery(id+"F0.wireOp",EDGE,"E7.1.2.1"),sQuery(id+"F0.wireOp",EDGE,"E7.1.2.2"),sQuery(id+"F0.wireOp",EDGE,"E7.1.2.3"),sQuery(id+"F0.wireOp",EDGE,"E7.1.3.0"),sQuery(id+"F0.wireOp",EDGE,"E7.1.3.1"),sQuery(id+"F0.wireOp",EDGE,"E7.1.3.2"),sQuery(id+"F0.wireOp",EDGE,"E7.1.3.3"),sQuery(id+"F0.wireOp",EDGE,"E7.1.4.0"),sQuery(id+"F0.wireOp",EDGE,"E7.1.4.1"),sQuery(id+"F0.wireOp",EDGE,"E7.1.4.2"),sQuery(id+"F0.wireOp",EDGE,"E7.1.4.3"),sQuery(id+"F0.wireOp",EDGE,"E7.1.5.0"),sQuery(id+"F0.wireOp",EDGE,"E7.1.5.1"),sQuery(id+"F0.wireOp",EDGE,"E7.1.5.2"),sQuery(id+"F0.wireOp",EDGE,"E7.1.5.3"),sQuery(id+"F0.wireOp",EDGE,"E7.2.0.0"),sQuery(id+"F0.wireOp",EDGE,"E7.2.0.1"),sQuery(id+"F0.wireOp",EDGE,"E7.2.0.2"),sQuery(id+"F0.wireOp",EDGE,"E7.2.0.3"),sQuery(id+"F0.wireOp",EDGE,"E7.2.1.0"),sQuery(id+"F0.wireOp",EDGE,"E7.2.1.1"),sQuery(id+"F0.wireOp",EDGE,"E7.2.1.2"),sQuery(id+"F0.wireOp",EDGE,"E7.2.1.3"),sQuery(id+"F0.wireOp",EDGE,"E7.2.2.0"),sQuery(id+"F0.wireOp",EDGE,"E7.2.2.1"),sQuery(id+"F0.wireOp",EDGE,"E7.2.2.2"),sQuery(id+"F0.wireOp",EDGE,"E7.2.2.3"),sQuery(id+"F0.wireOp",EDGE,"E7.2.3.0"),sQuery(id+"F0.wireOp",EDGE,"E7.2.3.1"),sQuery(id+"F0.wireOp",EDGE,"E7.2.3.2"),sQuery(id+"F0.wireOp",EDGE,"E7.2.3.3"),sQuery(id+"F0.wireOp",EDGE,"E7.2.4.0"),sQuery(id+"F0.wireOp",EDGE,"E7.2.4.1"),sQuery(id+"F0.wireOp",EDGE,"E7.2.4.2"),sQuery(id+"F0.wireOp",EDGE,"E7.2.4.3"),sQuery(id+"F0.wireOp",EDGE,"E7.2.5.0"),sQuery(id+"F0.wireOp",EDGE,"E7.2.5.1"),sQuery(id+"F0.wireOp",EDGE,"E7.2.5.2"),sQuery(id+"F0.wireOp",EDGE,"E7.2.5.3"),sQuery(id+"F0.wireOp",EDGE,"E7.3.0.0"),sQuery(id+"F0.wireOp",EDGE,"E7.3.0.1"),sQuery(id+"F0.wireOp",EDGE,"E7.3.0.2"),sQuery(id+"F0.wireOp",EDGE,"E7.3.0.3"),sQuery(id+"F0.wireOp",EDGE,"E7.3.1.0"),sQuery(id+"F0.wireOp",EDGE,"E7.3.1.1"),sQuery(id+"F0.wireOp",EDGE,"E7.3.1.2"),sQuery(id+"F0.wireOp",EDGE,"E7.3.1.3"),sQuery(id+"F0.wireOp",EDGE,"E7.3.2.0"),sQuery(id+"F0.wireOp",EDGE,"E7.3.2.1"),sQuery(id+"F0.wireOp",EDGE,"E7.3.2.2"),sQuery(id+"F0.wireOp",EDGE,"E7.3.2.3"),sQuery(id+"F0.wireOp",EDGE,"E7.3.3.0"),sQuery(id+"F0.wireOp",EDGE,"E7.3.3.1"),sQuery(id+"F0.wireOp",EDGE,"E7.3.3.2"),sQuery(id+"F0.wireOp",EDGE,"E7.3.3.3"),sQuery(id+"F0.wireOp",EDGE,"E7.3.4.0"),sQuery(id+"F0.wireOp",EDGE,"E7.3.4.1"),sQuery(id+"F0.wireOp",EDGE,"E7.3.4.2"),sQuery(id+"F0.wireOp",EDGE,"E7.3.4.3"),sQuery(id+"F0.wireOp",EDGE,"E7.3.5.0"),sQuery(id+"F0.wireOp",EDGE,"E7.3.5.1"),sQuery(id+"F0.wireOp",EDGE,"E7.3.5.2"),sQuery(id+"F0.wireOp",EDGE,"E7.3.5.3"),sQuery(id+"F0.wireOp",EDGE,"E7.4.0.0"),sQuery(id+"F0.wireOp",EDGE,"E7.4.0.1"),sQuery(id+"F0.wireOp",EDGE,"E7.4.0.2"),sQuery(id+"F0.wireOp",EDGE,"E7.4.0.3"),sQuery(id+"F0.wireOp",EDGE,"E7.4.1.0"),sQuery(id+"F0.wireOp",EDGE,"E7.4.1.1"),sQuery(id+"F0.wireOp",EDGE,"E7.4.1.2"),sQuery(id+"F0.wireOp",EDGE,"E7.4.1.3"),sQuery(id+"F0.wireOp",EDGE,"E7.4.2.0"),sQuery(id+"F0.wireOp",EDGE,"E7.4.2.1"),sQuery(id+"F0.wireOp",EDGE,"E7.4.2.2"),sQuery(id+"F0.wireOp",EDGE,"E7.4.2.3"),sQuery(id+"F0.wireOp",EDGE,"E7.4.3.0"),sQuery(id+"F0.wireOp",EDGE,"E7.4.3.1"),sQuery(id+"F0.wireOp",EDGE,"E7.4.3.2"),sQuery(id+"F0.wireOp",EDGE,"E7.4.3.3"),sQuery(id+"F0.wireOp",EDGE,"E7.4.4.0"),sQuery(id+"F0.wireOp",EDGE,"E7.4.4.1"),sQuery(id+"F0.wireOp",EDGE,"E7.4.4.2"),sQuery(id+"F0.wireOp",EDGE,"E7.4.4.3"),sQuery(id+"F0.wireOp",EDGE,"E7.4.5.0"),sQuery(id+"F0.wireOp",EDGE,"E7.4.5.1"),sQuery(id+"F0.wireOp",EDGE,"E7.4.5.2"),sQuery(id+"F0.wireOp",EDGE,"E7.4.5.3"),sQuery(id+"F0.wireOp",EDGE,"E7.5.0.0"),sQuery(id+"F0.wireOp",EDGE,"E7.5.0.1"),sQuery(id+"F0.wireOp",EDGE,"E7.5.0.2"),sQuery(id+"F0.wireOp",EDGE,"E7.5.0.3"),sQuery(id+"F0.wireOp",EDGE,"E7.5.1.0"),sQuery(id+"F0.wireOp",EDGE,"E7.5.1.1"),sQuery(id+"F0.wireOp",EDGE,"E7.5.1.2"),sQuery(id+"F0.wireOp",EDGE,"E7.5.1.3"),sQuery(id+"F0.wireOp",EDGE,"E7.5.2.0"),sQuery(id+"F0.wireOp",EDGE,"E7.5.2.1"),sQuery(id+"F0.wireOp",EDGE,"E7.5.2.2"),sQuery(id+"F0.wireOp",EDGE,"E7.5.2.3"),sQuery(id+"F0.wireOp",EDGE,"E7.5.3.0"),sQuery(id+"F0.wireOp",EDGE,"E7.5.3.1"),sQuery(id+"F0.wireOp",EDGE,"E7.5.3.2"),sQuery(id+"F0.wireOp",EDGE,"E7.5.3.3"),sQuery(id+"F0.wireOp",EDGE,"E7.5.4.0"),sQuery(id+"F0.wireOp",EDGE,"E7.5.4.1"),sQuery(id+"F0.wireOp",EDGE,"E7.5.4.2"),sQuery(id+"F0.wireOp",EDGE,"E7.5.4.3"),sQuery(id+"F0.wireOp",EDGE,"E7.5.5.0"),sQuery(id+"F0.wireOp",EDGE,"E7.5.5.1"),sQuery(id+"F0.wireOp",EDGE,"E7.5.5.2"),sQuery(id+"F0.wireOp",EDGE,"E7.5.5.3"),sQuery(id+"F0.wireOp",EDGE,"E7.6.0.0"),sQuery(id+"F0.wireOp",EDGE,"E7.6.0.1"),sQuery(id+"F0.wireOp",EDGE,"E7.6.0.2"),sQuery(id+"F0.wireOp",EDGE,"E7.6.0.3"),sQuery(id+"F0.wireOp",EDGE,"E7.6.1.0"),sQuery(id+"F0.wireOp",EDGE,"E7.6.1.1"),sQuery(id+"F0.wireOp",EDGE,"E7.6.1.2"),sQuery(id+"F0.wireOp",EDGE,"E7.6.1.3"),sQuery(id+"F0.wireOp",EDGE,"E7.6.2.0"),sQuery(id+"F0.wireOp",EDGE,"E7.6.2.1"),sQuery(id+"F0.wireOp",EDGE,"E7.6.2.2"),sQuery(id+"F0.wireOp",EDGE,"E7.6.2.3"),sQuery(id+"F0.wireOp",EDGE,"E7.6.3.0"),sQuery(id+"F0.wireOp",EDGE,"E7.6.3.1"),sQuery(id+"F0.wireOp",EDGE,"E7.6.3.2"),sQuery(id+"F0.wireOp",EDGE,"E7.6.3.3"),sQuery(id+"F0.wireOp",EDGE,"E7.6.4.0"),sQuery(id+"F0.wireOp",EDGE,"E7.6.4.1"),sQuery(id+"F0.wireOp",EDGE,"E7.6.4.2"),sQuery(id+"F0.wireOp",EDGE,"E7.6.4.3"),sQuery(id+"F0.wireOp",EDGE,"E7.6.5.0"),sQuery(id+"F0.wireOp",EDGE,"E7.6.5.1"),sQuery(id+"F0.wireOp",EDGE,"E7.6.5.2"),sQuery(id+"F0.wireOp",EDGE,"E7.6.5.3"),sQuery(id+"F0.wireOp",EDGE,"E7.7.0.0"),sQuery(id+"F0.wireOp",EDGE,"E7.7.0.1"),sQuery(id+"F0.wireOp",EDGE,"E7.7.0.2"),sQuery(id+"F0.wireOp",EDGE,"E7.7.0.3"),sQuery(id+"F0.wireOp",EDGE,"E7.7.1.0"),sQuery(id+"F0.wireOp",EDGE,"E7.7.1.1"),sQuery(id+"F0.wireOp",EDGE,"E7.7.1.2"),sQuery(id+"F0.wireOp",EDGE,"E7.7.1.3"),sQuery(id+"F0.wireOp",EDGE,"E7.7.2.0"),sQuery(id+"F0.wireOp",EDGE,"E7.7.2.1"),sQuery(id+"F0.wireOp",EDGE,"E7.7.2.2"),sQuery(id+"F0.wireOp",EDGE,"E7.7.2.3"),sQuery(id+"F0.wireOp",EDGE,"E7.7.3.0"),sQuery(id+"F0.wireOp",EDGE,"E7.7.3.1"),sQuery(id+"F0.wireOp",EDGE,"E7.7.3.2"),sQuery(id+"F0.wireOp",EDGE,"E7.7.3.3"),sQuery(id+"F0.wireOp",EDGE,"E7.7.4.0"),sQuery(id+"F0.wireOp",EDGE,"E7.7.4.1"),sQuery(id+"F0.wireOp",EDGE,"E7.7.4.2"),sQuery(id+"F0.wireOp",EDGE,"E7.7.4.3"),sQuery(id+"F0.wireOp",EDGE,"E7.7.5.0"),sQuery(id+"F0.wireOp",EDGE,"E7.7.5.1"),sQuery(id+"F0.wireOp",EDGE,"E7.7.5.2"),sQuery(id+"F0.wireOp",EDGE,"E7.7.5.3"),sQuery(id+"F0.wireOp",EDGE,"E7.8.0.0"),sQuery(id+"F0.wireOp",EDGE,"E7.8.0.1"),sQuery(id+"F0.wireOp",EDGE,"E7.8.0.2"),sQuery(id+"F0.wireOp",EDGE,"E7.8.0.3"),sQuery(id+"F0.wireOp",EDGE,"E7.8.1.0"),sQuery(id+"F0.wireOp",EDGE,"E7.8.1.1"),sQuery(id+"F0.wireOp",EDGE,"E7.8.1.2"),sQuery(id+"F0.wireOp",EDGE,"E7.8.1.3"),sQuery(id+"F0.wireOp",EDGE,"E7.8.2.0"),sQuery(id+"F0.wireOp",EDGE,"E7.8.2.1"),sQuery(id+"F0.wireOp",EDGE,"E7.8.2.2"),sQuery(id+"F0.wireOp",EDGE,"E7.8.2.3"),sQuery(id+"F0.wireOp",EDGE,"E7.8.3.0"),sQuery(id+"F0.wireOp",EDGE,"E7.8.3.1"),sQuery(id+"F0.wireOp",EDGE,"E7.8.3.2"),sQuery(id+"F0.wireOp",EDGE,"E7.8.3.3"),sQuery(id+"F0.wireOp",EDGE,"E7.8.4.0"),sQuery(id+"F0.wireOp",EDGE,"E7.8.4.1"),sQuery(id+"F0.wireOp",EDGE,"E7.8.4.2"),sQuery(id+"F0.wireOp",EDGE,"E7.8.4.3"),sQuery(id+"F0.wireOp",EDGE,"E7.8.5.0"),sQuery(id+"F0.wireOp",EDGE,"E7.8.5.1"),sQuery(id+"F0.wireOp",EDGE,"E7.8.5.2"),sQuery(id+"F0.wireOp",EDGE,"E7.8.5.3"),sQuery(id+"F0.wireOp",EDGE,"E7.9.0.0"),sQuery(id+"F0.wireOp",EDGE,"E7.9.0.1"),sQuery(id+"F0.wireOp",EDGE,"E7.9.0.2"),sQuery(id+"F0.wireOp",EDGE,"E7.9.0.3"),sQuery(id+"F0.wireOp",EDGE,"E7.9.1.0"),sQuery(id+"F0.wireOp",EDGE,"E7.9.1.1"),sQuery(id+"F0.wireOp",EDGE,"E7.9.1.2"),sQuery(id+"F0.wireOp",EDGE,"E7.9.1.3"),sQuery(id+"F0.wireOp",EDGE,"E7.9.2.0"),sQuery(id+"F0.wireOp",EDGE,"E7.9.2.1"),sQuery(id+"F0.wireOp",EDGE,"E7.9.2.2"),sQuery(id+"F0.wireOp",EDGE,"E7.9.2.3"),sQuery(id+"F0.wireOp",EDGE,"E7.9.3.0"),sQuery(id+"F0.wireOp",EDGE,"E7.9.3.1"),sQuery(id+"F0.wireOp",EDGE,"E7.9.3.2"),sQuery(id+"F0.wireOp",EDGE,"E7.9.3.3"),sQuery(id+"F0.wireOp",EDGE,"E7.9.4.0"),sQuery(id+"F0.wireOp",EDGE,"E7.9.4.1"),sQuery(id+"F0.wireOp",EDGE,"E7.9.4.2"),sQuery(id+"F0.wireOp",EDGE,"E7.9.4.3"),sQuery(id+"F0.wireOp",EDGE,"E7.9.5.0"),sQuery(id+"F0.wireOp",EDGE,"E7.9.5.1"),sQuery(id+"F0.wireOp",EDGE,"E7.9.5.2"),sQuery(id+"F0.wireOp",EDGE,"E7.9.5.3"),sQuery(id+"F0.wireOp",EDGE,"E7.10.0.0"),sQuery(id+"F0.wireOp",EDGE,"E7.10.0.1"),sQuery(id+"F0.wireOp",EDGE,"E7.10.0.2"),sQuery(id+"F0.wireOp",EDGE,"E7.10.0.3"),sQuery(id+"F0.wireOp",EDGE,"E7.10.1.0"),sQuery(id+"F0.wireOp",EDGE,"E7.10.1.1"),sQuery(id+"F0.wireOp",EDGE,"E7.10.1.2"),sQuery(id+"F0.wireOp",EDGE,"E7.10.1.3"),sQuery(id+"F0.wireOp",EDGE,"E7.10.2.0"),sQuery(id+"F0.wireOp",EDGE,"E7.10.2.1"),sQuery(id+"F0.wireOp",EDGE,"E7.10.2.2"),sQuery(id+"F0.wireOp",EDGE,"E7.10.2.3"),sQuery(id+"F0.wireOp",EDGE,"E7.10.3.0"),sQuery(id+"F0.wireOp",EDGE,"E7.10.3.1"),sQuery(id+"F0.wireOp",EDGE,"E7.10.3.2"),sQuery(id+"F0.wireOp",EDGE,"E7.10.3.3"),sQuery(id+"F0.wireOp",EDGE,"E7.10.4.0"),sQuery(id+"F0.wireOp",EDGE,"E7.10.4.1"),sQuery(id+"F0.wireOp",EDGE,"E7.10.4.2"),sQuery(id+"F0.wireOp",EDGE,"E7.10.4.3"),sQuery(id+"F0.wireOp",EDGE,"E7.10.5.0"),sQuery(id+"F0.wireOp",EDGE,"E7.10.5.1"),sQuery(id+"F0.wireOp",EDGE,"E7.10.5.2"),sQuery(id+"F0.wireOp",EDGE,"E7.10.5.3"),sQuery(id+"F0.wireOp",EDGE,"E7.11.0.0"),sQuery(id+"F0.wireOp",EDGE,"E7.11.0.1"),sQuery(id+"F0.wireOp",EDGE,"E7.11.0.2"),sQuery(id+"F0.wireOp",EDGE,"E7.11.0.3"),sQuery(id+"F0.wireOp",EDGE,"E7.11.1.0"),sQuery(id+"F0.wireOp",EDGE,"E7.11.1.1"),sQuery(id+"F0.wireOp",EDGE,"E7.11.1.2"),sQuery(id+"F0.wireOp",EDGE,"E7.11.1.3"),sQuery(id+"F0.wireOp",EDGE,"E7.11.2.0"),sQuery(id+"F0.wireOp",EDGE,"E7.11.2.1"),sQuery(id+"F0.wireOp",EDGE,"E7.11.2.2"),sQuery(id+"F0.wireOp",EDGE,"E7.11.2.3"),sQuery(id+"F0.wireOp",EDGE,"E7.11.3.0"),sQuery(id+"F0.wireOp",EDGE,"E7.11.3.1"),sQuery(id+"F0.wireOp",EDGE,"E7.11.3.2"),sQuery(id+"F0.wireOp",EDGE,"E7.11.3.3"),sQuery(id+"F0.wireOp",EDGE,"E7.11.4.0"),sQuery(id+"F0.wireOp",EDGE,"E7.11.4.1"),sQuery(id+"F0.wireOp",EDGE,"E7.11.4.2"),sQuery(id+"F0.wireOp",EDGE,"E7.11.4.3"),sQuery(id+"F0.wireOp",EDGE,"E7.11.5.0"),sQuery(id+"F0.wireOp",EDGE,"E7.11.5.1"),sQuery(id+"F0.wireOp",EDGE,"E7.11.5.2"),sQuery(id+"F0.wireOp",EDGE,"E7.11.5.3")])],"isStart":false});
            var sketch = newSketch(context, id + "F2", { "sketchPlane" : qUnion([Q0, Q1])});
            skLineSegment(sketch, "E8.bottom", {"start": v(-118.79, 154.74) * mm, "end": v(-112.79, 154.74) * mm});
            skLineSegment(sketch, "E8.top", {"start": v(-118.79, 148.74) * mm, "end": v(-112.79, 148.74) * mm});
            skLineSegment(sketch, "E8.left", {"start": v(-118.79, 154.74) * mm, "end": v(-118.79, 148.74) * mm});
            skLineSegment(sketch, "E8.right", {"start": v(-112.79, 154.74) * mm, "end": v(-112.79, 148.74) * mm});
            skLineSegment(sketch, "E9.bottom", {"start": v(115.21, 154.74) * mm, "end": v(109.21, 154.74) * mm});
            skLineSegment(sketch, "E9.top", {"start": v(115.21, 148.74) * mm, "end": v(109.21, 148.74) * mm});
            skLineSegment(sketch, "E9.left", {"start": v(115.21, 154.74) * mm, "end": v(115.21, 148.74) * mm});
            skLineSegment(sketch, "E9.right", {"start": v(109.21, 154.74) * mm, "end": v(109.21, 148.74) * mm});
            skLineSegment(sketch, "E10.bottom", {"start": v(115.21, -79.26) * mm, "end": v(109.21, -79.26) * mm});
            skLineSegment(sketch, "E10.top", {"start": v(115.21, -73.26) * mm, "end": v(109.21, -73.26) * mm});
            skLineSegment(sketch, "E10.left", {"start": v(115.21, -79.26) * mm, "end": v(115.21, -73.26) * mm});
            skLineSegment(sketch, "E10.right", {"start": v(109.21, -79.26) * mm, "end": v(109.21, -73.26) * mm});
            skLineSegment(sketch, "E11.bottom", {"start": v(-118.79, -79.26) * mm, "end": v(-112.79, -79.26) * mm});
            skLineSegment(sketch, "E11.top", {"start": v(-118.79, -73.26) * mm, "end": v(-112.79, -73.26) * mm});
            skLineSegment(sketch, "E11.left", {"start": v(-118.79, -79.26) * mm, "end": v(-118.79, -73.26) * mm});
            skLineSegment(sketch, "E11.right", {"start": v(-112.79, -79.26) * mm, "end": v(-112.79, -73.26) * mm});
            skSolve(sketch);
        }
        {
            var Q0;
            Q0=makeQuery(id+"F2.imprint","IMPRINT",FACE,{"disambiguationData":[TD([[makeQuery(id+"F2.imprint","IMPRINT",EDGE,{"derivedFrom":sQuery(id+"F2.wireOp",EDGE,"E8.bottom")}),-1.0]])]});
            var Q1;
            Q1=makeQuery(id+"F2.imprint","IMPRINT",FACE,{"disambiguationData":[TD([[makeQuery(id+"F2.imprint","IMPRINT",EDGE,{"derivedFrom":sQuery(id+"F2.wireOp",EDGE,"E9.bottom")}),1.0]])]});
            var Q2;
            Q2=makeQuery(id+"F2.imprint","IMPRINT",FACE,{"disambiguationData":[TD([[makeQuery(id+"F2.imprint","IMPRINT",EDGE,{"derivedFrom":sQuery(id+"F2.wireOp",EDGE,"E10.bottom")}),-1.0]])]});
            var Q3;
            Q3=makeQuery(id+"F2.imprint","IMPRINT",FACE,{"disambiguationData":[TD([[makeQuery(id+"F2.imprint","IMPRINT",EDGE,{"derivedFrom":sQuery(id+"F2.wireOp",EDGE,"E11.bottom")}),1.0]])]});
            extrude(context, id + "F3", {"entities" : qUnion([Q0, Q1, Q2, Q3]), "operationType" : NewBodyOperationType.REMOVE, "endBound" : BoundingType.THROUGH_ALL, "oppositeDirection" : true, "depth" : 25 * mm});
        }
        {
            var Q0;
            Q0=makeQuery(id+"F1.opExtrude","CAP_FACE",FACE,{"disambiguationData":[OSD([sQuery(id+"F0.wireOp",EDGE,"E0.bottom"),sQuery(id+"F0.wireOp",EDGE,"E0.top"),sQuery(id+"F0.wireOp",EDGE,"E0.left"),sQuery(id+"F0.wireOp",EDGE,"E0.right"),sQuery(id+"F0.wireOp",EDGE,"E1.bottom"),sQuery(id+"F0.wireOp",EDGE,"E1.top"),sQuery(id+"F0.wireOp",EDGE,"E1.left"),sQuery(id+"F0.wireOp",EDGE,"E1.right"),sQuery(id+"F0.wireOp",EDGE,"E4.3.1.0"),sQuery(id+"F0.wireOp",EDGE,"E4.6.1.0"),sQuery(id+"F0.wireOp",EDGE,"E4.9.1.0"),sQuery(id+"F0.wireOp",EDGE,"E4.12.1.0"),sQuery(id+"F0.wireOp",EDGE,"E4.3.2.0"),sQuery(id+"F0.wireOp",EDGE,"E4.6.2.0"),sQuery(id+"F0.wireOp",EDGE,"E4.9.2.0"),sQuery(id+"F0.wireOp",EDGE,"E4.12.2.0"),sQuery(id+"F0.wireOp",EDGE,"E4.3.3.0"),sQuery(id+"F0.wireOp",EDGE,"E4.6.3.0"),sQuery(id+"F0.wireOp",EDGE,"E4.9.3.0"),sQuery(id+"F0.wireOp",EDGE,"E4.12.3.0"),sQuery(id+"F0.wireOp",EDGE,"E4.3.4.0"),sQuery(id+"F0.wireOp",EDGE,"E4.6.4.0"),sQuery(id+"F0.wireOp",EDGE,"E4.9.4.0"),sQuery(id+"F0.wireOp",EDGE,"E4.12.4.0"),sQuery(id+"F0.wireOp",EDGE,"E4.3.5.0"),sQuery(id+"F0.wireOp",EDGE,"E4.6.5.0"),sQuery(id+"F0.wireOp",EDGE,"E4.9.5.0"),sQuery(id+"F0.wireOp",EDGE,"E4.12.5.0"),sQuery(id+"F0.wireOp",EDGE,"E4.3.6.0"),sQuery(id+"F0.wireOp",EDGE,"E4.6.6.0"),sQuery(id+"F0.wireOp",EDGE,"E4.9.6.0"),sQuery(id+"F0.wireOp",EDGE,"E4.12.6.0"),sQuery(id+"F0.wireOp",EDGE,"E4.3.7.0"),sQuery(id+"F0.wireOp",EDGE,"E4.6.7.0"),sQuery(id+"F0.wireOp",EDGE,"E4.9.7.0"),sQuery(id+"F0.wireOp",EDGE,"E4.12.7.0"),sQuery(id+"F0.wireOp",EDGE,"E4.3.8.0"),sQuery(id+"F0.wireOp",EDGE,"E4.6.8.0"),sQuery(id+"F0.wireOp",EDGE,"E4.9.8.0"),sQuery(id+"F0.wireOp",EDGE,"E4.12.8.0"),sQuery(id+"F0.wireOp",EDGE,"E4.3.9.0"),sQuery(id+"F0.wireOp",EDGE,"E4.6.9.0"),sQuery(id+"F0.wireOp",EDGE,"E4.9.9.0"),sQuery(id+"F0.wireOp",EDGE,"E4.12.9.0"),sQuery(id+"F0.wireOp",EDGE,"E4.3.10.0"),sQuery(id+"F0.wireOp",EDGE,"E4.6.10.0"),sQuery(id+"F0.wireOp",EDGE,"E4.9.10.0"),sQuery(id+"F0.wireOp",EDGE,"E4.12.10.0"),sQuery(id+"F0.wireOp",EDGE,"E4.3.11.0"),sQuery(id+"F0.wireOp",EDGE,"E4.6.11.0"),sQuery(id+"F0.wireOp",EDGE,"E4.9.11.0"),sQuery(id+"F0.wireOp",EDGE,"E4.12.11.0"),sQuery(id+"F0.wireOp",EDGE,"E5.3.0.1"),sQuery(id+"F0.wireOp",EDGE,"E5.6.0.1"),sQuery(id+"F0.wireOp",EDGE,"E5.9.0.1"),sQuery(id+"F0.wireOp",EDGE,"E5.12.0.1"),sQuery(id+"F0.wireOp",EDGE,"E5.3.0.2"),sQuery(id+"F0.wireOp",EDGE,"E5.6.0.2"),sQuery(id+"F0.wireOp",EDGE,"E5.9.0.2"),sQuery(id+"F0.wireOp",EDGE,"E5.12.0.2"),sQuery(id+"F0.wireOp",EDGE,"E5.3.0.3"),sQuery(id+"F0.wireOp",EDGE,"E5.6.0.3"),sQuery(id+"F0.wireOp",EDGE,"E5.9.0.3"),sQuery(id+"F0.wireOp",EDGE,"E5.12.0.3"),sQuery(id+"F0.wireOp",EDGE,"E5.3.0.4"),sQuery(id+"F0.wireOp",EDGE,"E5.6.0.4"),sQuery(id+"F0.wireOp",EDGE,"E5.9.0.4"),sQuery(id+"F0.wireOp",EDGE,"E5.12.0.4"),sQuery(id+"F0.wireOp",EDGE,"E5.3.0.5"),sQuery(id+"F0.wireOp",EDGE,"E5.6.0.5"),sQuery(id+"F0.wireOp",EDGE,"E5.9.0.5"),sQuery(id+"F0.wireOp",EDGE,"E5.12.0.5"),sQuery(id+"F0.wireOp",EDGE,"E5.3.1.1"),sQuery(id+"F0.wireOp",EDGE,"E5.6.1.1"),sQuery(id+"F0.wireOp",EDGE,"E5.9.1.1"),sQuery(id+"F0.wireOp",EDGE,"E5.12.1.1"),sQuery(id+"F0.wireOp",EDGE,"E5.3.1.2"),sQuery(id+"F0.wireOp",EDGE,"E5.6.1.2"),sQuery(id+"F0.wireOp",EDGE,"E5.9.1.2"),sQuery(id+"F0.wireOp",EDGE,"E5.12.1.2"),sQuery(id+"F0.wireOp",EDGE,"E5.3.1.3"),sQuery(id+"F0.wireOp",EDGE,"E5.6.1.3"),sQuery(id+"F0.wireOp",EDGE,"E5.9.1.3"),sQuery(id+"F0.wireOp",EDGE,"E5.12.1.3"),sQuery(id+"F0.wireOp",EDGE,"E5.3.1.4"),sQuery(id+"F0.wireOp",EDGE,"E5.6.1.4"),sQuery(id+"F0.wireOp",EDGE,"E5.9.1.4"),sQuery(id+"F0.wireOp",EDGE,"E5.12.1.4"),sQuery(id+"F0.wireOp",EDGE,"E5.3.1.5"),sQuery(id+"F0.wireOp",EDGE,"E5.6.1.5"),sQuery(id+"F0.wireOp",EDGE,"E5.9.1.5"),sQuery(id+"F0.wireOp",EDGE,"E5.12.1.5"),sQuery(id+"F0.wireOp",EDGE,"E5.3.2.1"),sQuery(id+"F0.wireOp",EDGE,"E5.6.2.1"),sQuery(id+"F0.wireOp",EDGE,"E5.9.2.1"),sQuery(id+"F0.wireOp",EDGE,"E5.12.2.1"),sQuery(id+"F0.wireOp",EDGE,"E5.3.2.2"),sQuery(id+"F0.wireOp",EDGE,"E5.6.2.2"),sQuery(id+"F0.wireOp",EDGE,"E5.9.2.2"),sQuery(id+"F0.wireOp",EDGE,"E5.12.2.2"),sQuery(id+"F0.wireOp",EDGE,"E5.3.2.3"),sQuery(id+"F0.wireOp",EDGE,"E5.6.2.3"),sQuery(id+"F0.wireOp",EDGE,"E5.9.2.3"),sQuery(id+"F0.wireOp",EDGE,"E5.12.2.3"),sQuery(id+"F0.wireOp",EDGE,"E5.3.2.4"),sQuery(id+"F0.wireOp",EDGE,"E5.6.2.4"),sQuery(id+"F0.wireOp",EDGE,"E5.9.2.4"),sQuery(id+"F0.wireOp",EDGE,"E5.12.2.4"),sQuery(id+"F0.wireOp",EDGE,"E5.3.2.5"),sQuery(id+"F0.wireOp",EDGE,"E5.6.2.5"),sQuery(id+"F0.wireOp",EDGE,"E5.9.2.5"),sQuery(id+"F0.wireOp",EDGE,"E5.12.2.5"),sQuery(id+"F0.wireOp",EDGE,"E5.3.3.1"),sQuery(id+"F0.wireOp",EDGE,"E5.6.3.1"),sQuery(id+"F0.wireOp",EDGE,"E5.9.3.1"),sQuery(id+"F0.wireOp",EDGE,"E5.12.3.1"),sQuery(id+"F0.wireOp",EDGE,"E5.3.3.2"),sQuery(id+"F0.wireOp",EDGE,"E5.6.3.2"),sQuery(id+"F0.wireOp",EDGE,"E5.9.3.2"),sQuery(id+"F0.wireOp",EDGE,"E5.12.3.2"),sQuery(id+"F0.wireOp",EDGE,"E5.3.3.3"),sQuery(id+"F0.wireOp",EDGE,"E5.6.3.3"),sQuery(id+"F0.wireOp",EDGE,"E5.9.3.3"),sQuery(id+"F0.wireOp",EDGE,"E5.12.3.3"),sQuery(id+"F0.wireOp",EDGE,"E5.3.3.4"),sQuery(id+"F0.wireOp",EDGE,"E5.6.3.4"),sQuery(id+"F0.wireOp",EDGE,"E5.9.3.4"),sQuery(id+"F0.wireOp",EDGE,"E5.12.3.4"),sQuery(id+"F0.wireOp",EDGE,"E5.3.3.5"),sQuery(id+"F0.wireOp",EDGE,"E5.6.3.5"),sQuery(id+"F0.wireOp",EDGE,"E5.9.3.5"),sQuery(id+"F0.wireOp",EDGE,"E5.12.3.5"),sQuery(id+"F0.wireOp",EDGE,"E5.3.4.1"),sQuery(id+"F0.wireOp",EDGE,"E5.6.4.1"),sQuery(id+"F0.wireOp",EDGE,"E5.9.4.1"),sQuery(id+"F0.wireOp",EDGE,"E5.12.4.1"),sQuery(id+"F0.wireOp",EDGE,"E5.3.4.2"),sQuery(id+"F0.wireOp",EDGE,"E5.6.4.2"),sQuery(id+"F0.wireOp",EDGE,"E5.9.4.2"),sQuery(id+"F0.wireOp",EDGE,"E5.12.4.2"),sQuery(id+"F0.wireOp",EDGE,"E5.3.4.3"),sQuery(id+"F0.wireOp",EDGE,"E5.6.4.3"),sQuery(id+"F0.wireOp",EDGE,"E5.9.4.3"),sQuery(id+"F0.wireOp",EDGE,"E5.12.4.3"),sQuery(id+"F0.wireOp",EDGE,"E5.3.4.4"),sQuery(id+"F0.wireOp",EDGE,"E5.6.4.4"),sQuery(id+"F0.wireOp",EDGE,"E5.9.4.4"),sQuery(id+"F0.wireOp",EDGE,"E5.12.4.4"),sQuery(id+"F0.wireOp",EDGE,"E5.3.4.5"),sQuery(id+"F0.wireOp",EDGE,"E5.6.4.5"),sQuery(id+"F0.wireOp",EDGE,"E5.9.4.5"),sQuery(id+"F0.wireOp",EDGE,"E5.12.4.5"),sQuery(id+"F0.wireOp",EDGE,"E5.3.5.1"),sQuery(id+"F0.wireOp",EDGE,"E5.6.5.1"),sQuery(id+"F0.wireOp",EDGE,"E5.9.5.1"),sQuery(id+"F0.wireOp",EDGE,"E5.12.5.1"),sQuery(id+"F0.wireOp",EDGE,"E5.3.5.2"),sQuery(id+"F0.wireOp",EDGE,"E5.6.5.2"),sQuery(id+"F0.wireOp",EDGE,"E5.9.5.2"),sQuery(id+"F0.wireOp",EDGE,"E5.12.5.2"),sQuery(id+"F0.wireOp",EDGE,"E5.3.5.3"),sQuery(id+"F0.wireOp",EDGE,"E5.6.5.3"),sQuery(id+"F0.wireOp",EDGE,"E5.9.5.3"),sQuery(id+"F0.wireOp",EDGE,"E5.12.5.3"),sQuery(id+"F0.wireOp",EDGE,"E5.3.5.4"),sQuery(id+"F0.wireOp",EDGE,"E5.6.5.4"),sQuery(id+"F0.wireOp",EDGE,"E5.9.5.4"),sQuery(id+"F0.wireOp",EDGE,"E5.12.5.4"),sQuery(id+"F0.wireOp",EDGE,"E5.3.5.5"),sQuery(id+"F0.wireOp",EDGE,"E5.6.5.5"),sQuery(id+"F0.wireOp",EDGE,"E5.9.5.5"),sQuery(id+"F0.wireOp",EDGE,"E5.12.5.5"),sQuery(id+"F0.wireOp",EDGE,"E5.3.6.1"),sQuery(id+"F0.wireOp",EDGE,"E5.6.6.1"),sQuery(id+"F0.wireOp",EDGE,"E5.9.6.1"),sQuery(id+"F0.wireOp",EDGE,"E5.12.6.1"),sQuery(id+"F0.wireOp",EDGE,"E5.3.6.2"),sQuery(id+"F0.wireOp",EDGE,"E5.6.6.2"),sQuery(id+"F0.wireOp",EDGE,"E5.9.6.2"),sQuery(id+"F0.wireOp",EDGE,"E5.12.6.2"),sQuery(id+"F0.wireOp",EDGE,"E5.3.6.3"),sQuery(id+"F0.wireOp",EDGE,"E5.6.6.3"),sQuery(id+"F0.wireOp",EDGE,"E5.9.6.3"),sQuery(id+"F0.wireOp",EDGE,"E5.12.6.3"),sQuery(id+"F0.wireOp",EDGE,"E5.3.6.4"),sQuery(id+"F0.wireOp",EDGE,"E5.6.6.4"),sQuery(id+"F0.wireOp",EDGE,"E5.9.6.4"),sQuery(id+"F0.wireOp",EDGE,"E5.12.6.4"),sQuery(id+"F0.wireOp",EDGE,"E5.3.6.5"),sQuery(id+"F0.wireOp",EDGE,"E5.6.6.5"),sQuery(id+"F0.wireOp",EDGE,"E5.9.6.5"),sQuery(id+"F0.wireOp",EDGE,"E5.12.6.5"),sQuery(id+"F0.wireOp",EDGE,"E5.3.7.1"),sQuery(id+"F0.wireOp",EDGE,"E5.6.7.1"),sQuery(id+"F0.wireOp",EDGE,"E5.9.7.1"),sQuery(id+"F0.wireOp",EDGE,"E5.12.7.1"),sQuery(id+"F0.wireOp",EDGE,"E5.3.7.2"),sQuery(id+"F0.wireOp",EDGE,"E5.6.7.2"),sQuery(id+"F0.wireOp",EDGE,"E5.9.7.2"),sQuery(id+"F0.wireOp",EDGE,"E5.12.7.2"),sQuery(id+"F0.wireOp",EDGE,"E5.3.7.3"),sQuery(id+"F0.wireOp",EDGE,"E5.6.7.3"),sQuery(id+"F0.wireOp",EDGE,"E5.9.7.3"),sQuery(id+"F0.wireOp",EDGE,"E5.12.7.3"),sQuery(id+"F0.wireOp",EDGE,"E5.3.7.4"),sQuery(id+"F0.wireOp",EDGE,"E5.6.7.4"),sQuery(id+"F0.wireOp",EDGE,"E5.9.7.4"),sQuery(id+"F0.wireOp",EDGE,"E5.12.7.4"),sQuery(id+"F0.wireOp",EDGE,"E5.3.7.5"),sQuery(id+"F0.wireOp",EDGE,"E5.6.7.5"),sQuery(id+"F0.wireOp",EDGE,"E5.9.7.5"),sQuery(id+"F0.wireOp",EDGE,"E5.12.7.5"),sQuery(id+"F0.wireOp",EDGE,"E5.3.8.1"),sQuery(id+"F0.wireOp",EDGE,"E5.6.8.1"),sQuery(id+"F0.wireOp",EDGE,"E5.9.8.1"),sQuery(id+"F0.wireOp",EDGE,"E5.12.8.1"),sQuery(id+"F0.wireOp",EDGE,"E5.3.8.2"),sQuery(id+"F0.wireOp",EDGE,"E5.6.8.2"),sQuery(id+"F0.wireOp",EDGE,"E5.9.8.2"),sQuery(id+"F0.wireOp",EDGE,"E5.12.8.2"),sQuery(id+"F0.wireOp",EDGE,"E5.3.8.3"),sQuery(id+"F0.wireOp",EDGE,"E5.6.8.3"),sQuery(id+"F0.wireOp",EDGE,"E5.9.8.3"),sQuery(id+"F0.wireOp",EDGE,"E5.12.8.3"),sQuery(id+"F0.wireOp",EDGE,"E5.3.8.4"),sQuery(id+"F0.wireOp",EDGE,"E5.6.8.4"),sQuery(id+"F0.wireOp",EDGE,"E5.9.8.4"),sQuery(id+"F0.wireOp",EDGE,"E5.12.8.4"),sQuery(id+"F0.wireOp",EDGE,"E5.3.8.5"),sQuery(id+"F0.wireOp",EDGE,"E5.6.8.5"),sQuery(id+"F0.wireOp",EDGE,"E5.9.8.5"),sQuery(id+"F0.wireOp",EDGE,"E5.12.8.5"),sQuery(id+"F0.wireOp",EDGE,"E5.3.9.1"),sQuery(id+"F0.wireOp",EDGE,"E5.6.9.1"),sQuery(id+"F0.wireOp",EDGE,"E5.9.9.1"),sQuery(id+"F0.wireOp",EDGE,"E5.12.9.1"),sQuery(id+"F0.wireOp",EDGE,"E5.3.9.2"),sQuery(id+"F0.wireOp",EDGE,"E5.6.9.2"),sQuery(id+"F0.wireOp",EDGE,"E5.9.9.2"),sQuery(id+"F0.wireOp",EDGE,"E5.12.9.2"),sQuery(id+"F0.wireOp",EDGE,"E5.3.9.3"),sQuery(id+"F0.wireOp",EDGE,"E5.6.9.3"),sQuery(id+"F0.wireOp",EDGE,"E5.9.9.3"),sQuery(id+"F0.wireOp",EDGE,"E5.12.9.3"),sQuery(id+"F0.wireOp",EDGE,"E5.3.9.4"),sQuery(id+"F0.wireOp",EDGE,"E5.6.9.4"),sQuery(id+"F0.wireOp",EDGE,"E5.9.9.4"),sQuery(id+"F0.wireOp",EDGE,"E5.12.9.4"),sQuery(id+"F0.wireOp",EDGE,"E5.3.9.5"),sQuery(id+"F0.wireOp",EDGE,"E5.6.9.5"),sQuery(id+"F0.wireOp",EDGE,"E5.9.9.5"),sQuery(id+"F0.wireOp",EDGE,"E5.12.9.5"),sQuery(id+"F0.wireOp",EDGE,"E5.3.10.1"),sQuery(id+"F0.wireOp",EDGE,"E5.6.10.1"),sQuery(id+"F0.wireOp",EDGE,"E5.9.10.1"),sQuery(id+"F0.wireOp",EDGE,"E5.12.10.1"),sQuery(id+"F0.wireOp",EDGE,"E5.3.10.2"),sQuery(id+"F0.wireOp",EDGE,"E5.6.10.2"),sQuery(id+"F0.wireOp",EDGE,"E5.9.10.2"),sQuery(id+"F0.wireOp",EDGE,"E5.12.10.2"),sQuery(id+"F0.wireOp",EDGE,"E5.3.10.3"),sQuery(id+"F0.wireOp",EDGE,"E5.6.10.3"),sQuery(id+"F0.wireOp",EDGE,"E5.9.10.3"),sQuery(id+"F0.wireOp",EDGE,"E5.12.10.3"),sQuery(id+"F0.wireOp",EDGE,"E5.3.10.4"),sQuery(id+"F0.wireOp",EDGE,"E5.6.10.4"),sQuery(id+"F0.wireOp",EDGE,"E5.9.10.4"),sQuery(id+"F0.wireOp",EDGE,"E5.12.10.4"),sQuery(id+"F0.wireOp",EDGE,"E5.3.10.5"),sQuery(id+"F0.wireOp",EDGE,"E5.6.10.5"),sQuery(id+"F0.wireOp",EDGE,"E5.9.10.5"),sQuery(id+"F0.wireOp",EDGE,"E5.12.10.5"),sQuery(id+"F0.wireOp",EDGE,"E5.3.11.1"),sQuery(id+"F0.wireOp",EDGE,"E5.6.11.1"),sQuery(id+"F0.wireOp",EDGE,"E5.9.11.1"),sQuery(id+"F0.wireOp",EDGE,"E5.12.11.1"),sQuery(id+"F0.wireOp",EDGE,"E5.3.11.2"),sQuery(id+"F0.wireOp",EDGE,"E5.6.11.2"),sQuery(id+"F0.wireOp",EDGE,"E5.9.11.2"),sQuery(id+"F0.wireOp",EDGE,"E5.12.11.2"),sQuery(id+"F0.wireOp",EDGE,"E5.3.11.3"),sQuery(id+"F0.wireOp",EDGE,"E5.6.11.3"),sQuery(id+"F0.wireOp",EDGE,"E5.9.11.3"),sQuery(id+"F0.wireOp",EDGE,"E5.12.11.3"),sQuery(id+"F0.wireOp",EDGE,"E5.3.11.4"),sQuery(id+"F0.wireOp",EDGE,"E5.6.11.4"),sQuery(id+"F0.wireOp",EDGE,"E5.9.11.4"),sQuery(id+"F0.wireOp",EDGE,"E5.12.11.4"),sQuery(id+"F0.wireOp",EDGE,"E5.3.11.5"),sQuery(id+"F0.wireOp",EDGE,"E5.6.11.5"),sQuery(id+"F0.wireOp",EDGE,"E5.9.11.5"),sQuery(id+"F0.wireOp",EDGE,"E5.12.11.5"),sQuery(id+"F0.wireOp",EDGE,"E6.bottom"),sQuery(id+"F0.wireOp",EDGE,"E6.top"),sQuery(id+"F0.wireOp",EDGE,"E6.left"),sQuery(id+"F0.wireOp",EDGE,"E6.right"),sQuery(id+"F0.wireOp",EDGE,"E7.0.1.0"),sQuery(id+"F0.wireOp",EDGE,"E7.0.1.1"),sQuery(id+"F0.wireOp",EDGE,"E7.0.1.2"),sQuery(id+"F0.wireOp",EDGE,"E7.0.1.3"),sQuery(id+"F0.wireOp",EDGE,"E7.0.2.0"),sQuery(id+"F0.wireOp",EDGE,"E7.0.2.1"),sQuery(id+"F0.wireOp",EDGE,"E7.0.2.2"),sQuery(id+"F0.wireOp",EDGE,"E7.0.2.3"),sQuery(id+"F0.wireOp",EDGE,"E7.0.3.0"),sQuery(id+"F0.wireOp",EDGE,"E7.0.3.1"),sQuery(id+"F0.wireOp",EDGE,"E7.0.3.2"),sQuery(id+"F0.wireOp",EDGE,"E7.0.3.3"),sQuery(id+"F0.wireOp",EDGE,"E7.0.4.0"),sQuery(id+"F0.wireOp",EDGE,"E7.0.4.1"),sQuery(id+"F0.wireOp",EDGE,"E7.0.4.2"),sQuery(id+"F0.wireOp",EDGE,"E7.0.4.3"),sQuery(id+"F0.wireOp",EDGE,"E7.0.5.0"),sQuery(id+"F0.wireOp",EDGE,"E7.0.5.1"),sQuery(id+"F0.wireOp",EDGE,"E7.0.5.2"),sQuery(id+"F0.wireOp",EDGE,"E7.0.5.3"),sQuery(id+"F0.wireOp",EDGE,"E7.1.0.0"),sQuery(id+"F0.wireOp",EDGE,"E7.1.0.1"),sQuery(id+"F0.wireOp",EDGE,"E7.1.0.2"),sQuery(id+"F0.wireOp",EDGE,"E7.1.0.3"),sQuery(id+"F0.wireOp",EDGE,"E7.1.1.0"),sQuery(id+"F0.wireOp",EDGE,"E7.1.1.1"),sQuery(id+"F0.wireOp",EDGE,"E7.1.1.2"),sQuery(id+"F0.wireOp",EDGE,"E7.1.1.3"),sQuery(id+"F0.wireOp",EDGE,"E7.1.2.0"),sQuery(id+"F0.wireOp",EDGE,"E7.1.2.1"),sQuery(id+"F0.wireOp",EDGE,"E7.1.2.2"),sQuery(id+"F0.wireOp",EDGE,"E7.1.2.3"),sQuery(id+"F0.wireOp",EDGE,"E7.1.3.0"),sQuery(id+"F0.wireOp",EDGE,"E7.1.3.1"),sQuery(id+"F0.wireOp",EDGE,"E7.1.3.2"),sQuery(id+"F0.wireOp",EDGE,"E7.1.3.3"),sQuery(id+"F0.wireOp",EDGE,"E7.1.4.0"),sQuery(id+"F0.wireOp",EDGE,"E7.1.4.1"),sQuery(id+"F0.wireOp",EDGE,"E7.1.4.2"),sQuery(id+"F0.wireOp",EDGE,"E7.1.4.3"),sQuery(id+"F0.wireOp",EDGE,"E7.1.5.0"),sQuery(id+"F0.wireOp",EDGE,"E7.1.5.1"),sQuery(id+"F0.wireOp",EDGE,"E7.1.5.2"),sQuery(id+"F0.wireOp",EDGE,"E7.1.5.3"),sQuery(id+"F0.wireOp",EDGE,"E7.2.0.0"),sQuery(id+"F0.wireOp",EDGE,"E7.2.0.1"),sQuery(id+"F0.wireOp",EDGE,"E7.2.0.2"),sQuery(id+"F0.wireOp",EDGE,"E7.2.0.3"),sQuery(id+"F0.wireOp",EDGE,"E7.2.1.0"),sQuery(id+"F0.wireOp",EDGE,"E7.2.1.1"),sQuery(id+"F0.wireOp",EDGE,"E7.2.1.2"),sQuery(id+"F0.wireOp",EDGE,"E7.2.1.3"),sQuery(id+"F0.wireOp",EDGE,"E7.2.2.0"),sQuery(id+"F0.wireOp",EDGE,"E7.2.2.1"),sQuery(id+"F0.wireOp",EDGE,"E7.2.2.2"),sQuery(id+"F0.wireOp",EDGE,"E7.2.2.3"),sQuery(id+"F0.wireOp",EDGE,"E7.2.3.0"),sQuery(id+"F0.wireOp",EDGE,"E7.2.3.1"),sQuery(id+"F0.wireOp",EDGE,"E7.2.3.2"),sQuery(id+"F0.wireOp",EDGE,"E7.2.3.3"),sQuery(id+"F0.wireOp",EDGE,"E7.2.4.0"),sQuery(id+"F0.wireOp",EDGE,"E7.2.4.1"),sQuery(id+"F0.wireOp",EDGE,"E7.2.4.2"),sQuery(id+"F0.wireOp",EDGE,"E7.2.4.3"),sQuery(id+"F0.wireOp",EDGE,"E7.2.5.0"),sQuery(id+"F0.wireOp",EDGE,"E7.2.5.1"),sQuery(id+"F0.wireOp",EDGE,"E7.2.5.2"),sQuery(id+"F0.wireOp",EDGE,"E7.2.5.3"),sQuery(id+"F0.wireOp",EDGE,"E7.3.0.0"),sQuery(id+"F0.wireOp",EDGE,"E7.3.0.1"),sQuery(id+"F0.wireOp",EDGE,"E7.3.0.2"),sQuery(id+"F0.wireOp",EDGE,"E7.3.0.3"),sQuery(id+"F0.wireOp",EDGE,"E7.3.1.0"),sQuery(id+"F0.wireOp",EDGE,"E7.3.1.1"),sQuery(id+"F0.wireOp",EDGE,"E7.3.1.2"),sQuery(id+"F0.wireOp",EDGE,"E7.3.1.3"),sQuery(id+"F0.wireOp",EDGE,"E7.3.2.0"),sQuery(id+"F0.wireOp",EDGE,"E7.3.2.1"),sQuery(id+"F0.wireOp",EDGE,"E7.3.2.2"),sQuery(id+"F0.wireOp",EDGE,"E7.3.2.3"),sQuery(id+"F0.wireOp",EDGE,"E7.3.3.0"),sQuery(id+"F0.wireOp",EDGE,"E7.3.3.1"),sQuery(id+"F0.wireOp",EDGE,"E7.3.3.2"),sQuery(id+"F0.wireOp",EDGE,"E7.3.3.3"),sQuery(id+"F0.wireOp",EDGE,"E7.3.4.0"),sQuery(id+"F0.wireOp",EDGE,"E7.3.4.1"),sQuery(id+"F0.wireOp",EDGE,"E7.3.4.2"),sQuery(id+"F0.wireOp",EDGE,"E7.3.4.3"),sQuery(id+"F0.wireOp",EDGE,"E7.3.5.0"),sQuery(id+"F0.wireOp",EDGE,"E7.3.5.1"),sQuery(id+"F0.wireOp",EDGE,"E7.3.5.2"),sQuery(id+"F0.wireOp",EDGE,"E7.3.5.3"),sQuery(id+"F0.wireOp",EDGE,"E7.4.0.0"),sQuery(id+"F0.wireOp",EDGE,"E7.4.0.1"),sQuery(id+"F0.wireOp",EDGE,"E7.4.0.2"),sQuery(id+"F0.wireOp",EDGE,"E7.4.0.3"),sQuery(id+"F0.wireOp",EDGE,"E7.4.1.0"),sQuery(id+"F0.wireOp",EDGE,"E7.4.1.1"),sQuery(id+"F0.wireOp",EDGE,"E7.4.1.2"),sQuery(id+"F0.wireOp",EDGE,"E7.4.1.3"),sQuery(id+"F0.wireOp",EDGE,"E7.4.2.0"),sQuery(id+"F0.wireOp",EDGE,"E7.4.2.1"),sQuery(id+"F0.wireOp",EDGE,"E7.4.2.2"),sQuery(id+"F0.wireOp",EDGE,"E7.4.2.3"),sQuery(id+"F0.wireOp",EDGE,"E7.4.3.0"),sQuery(id+"F0.wireOp",EDGE,"E7.4.3.1"),sQuery(id+"F0.wireOp",EDGE,"E7.4.3.2"),sQuery(id+"F0.wireOp",EDGE,"E7.4.3.3"),sQuery(id+"F0.wireOp",EDGE,"E7.4.4.0"),sQuery(id+"F0.wireOp",EDGE,"E7.4.4.1"),sQuery(id+"F0.wireOp",EDGE,"E7.4.4.2"),sQuery(id+"F0.wireOp",EDGE,"E7.4.4.3"),sQuery(id+"F0.wireOp",EDGE,"E7.4.5.0"),sQuery(id+"F0.wireOp",EDGE,"E7.4.5.1"),sQuery(id+"F0.wireOp",EDGE,"E7.4.5.2"),sQuery(id+"F0.wireOp",EDGE,"E7.4.5.3"),sQuery(id+"F0.wireOp",EDGE,"E7.5.0.0"),sQuery(id+"F0.wireOp",EDGE,"E7.5.0.1"),sQuery(id+"F0.wireOp",EDGE,"E7.5.0.2"),sQuery(id+"F0.wireOp",EDGE,"E7.5.0.3"),sQuery(id+"F0.wireOp",EDGE,"E7.5.1.0"),sQuery(id+"F0.wireOp",EDGE,"E7.5.1.1"),sQuery(id+"F0.wireOp",EDGE,"E7.5.1.2"),sQuery(id+"F0.wireOp",EDGE,"E7.5.1.3"),sQuery(id+"F0.wireOp",EDGE,"E7.5.2.0"),sQuery(id+"F0.wireOp",EDGE,"E7.5.2.1"),sQuery(id+"F0.wireOp",EDGE,"E7.5.2.2"),sQuery(id+"F0.wireOp",EDGE,"E7.5.2.3"),sQuery(id+"F0.wireOp",EDGE,"E7.5.3.0"),sQuery(id+"F0.wireOp",EDGE,"E7.5.3.1"),sQuery(id+"F0.wireOp",EDGE,"E7.5.3.2"),sQuery(id+"F0.wireOp",EDGE,"E7.5.3.3"),sQuery(id+"F0.wireOp",EDGE,"E7.5.4.0"),sQuery(id+"F0.wireOp",EDGE,"E7.5.4.1"),sQuery(id+"F0.wireOp",EDGE,"E7.5.4.2"),sQuery(id+"F0.wireOp",EDGE,"E7.5.4.3"),sQuery(id+"F0.wireOp",EDGE,"E7.5.5.0"),sQuery(id+"F0.wireOp",EDGE,"E7.5.5.1"),sQuery(id+"F0.wireOp",EDGE,"E7.5.5.2"),sQuery(id+"F0.wireOp",EDGE,"E7.5.5.3"),sQuery(id+"F0.wireOp",EDGE,"E7.6.0.0"),sQuery(id+"F0.wireOp",EDGE,"E7.6.0.1"),sQuery(id+"F0.wireOp",EDGE,"E7.6.0.2"),sQuery(id+"F0.wireOp",EDGE,"E7.6.0.3"),sQuery(id+"F0.wireOp",EDGE,"E7.6.1.0"),sQuery(id+"F0.wireOp",EDGE,"E7.6.1.1"),sQuery(id+"F0.wireOp",EDGE,"E7.6.1.2"),sQuery(id+"F0.wireOp",EDGE,"E7.6.1.3"),sQuery(id+"F0.wireOp",EDGE,"E7.6.2.0"),sQuery(id+"F0.wireOp",EDGE,"E7.6.2.1"),sQuery(id+"F0.wireOp",EDGE,"E7.6.2.2"),sQuery(id+"F0.wireOp",EDGE,"E7.6.2.3"),sQuery(id+"F0.wireOp",EDGE,"E7.6.3.0"),sQuery(id+"F0.wireOp",EDGE,"E7.6.3.1"),sQuery(id+"F0.wireOp",EDGE,"E7.6.3.2"),sQuery(id+"F0.wireOp",EDGE,"E7.6.3.3"),sQuery(id+"F0.wireOp",EDGE,"E7.6.4.0"),sQuery(id+"F0.wireOp",EDGE,"E7.6.4.1"),sQuery(id+"F0.wireOp",EDGE,"E7.6.4.2"),sQuery(id+"F0.wireOp",EDGE,"E7.6.4.3"),sQuery(id+"F0.wireOp",EDGE,"E7.6.5.0"),sQuery(id+"F0.wireOp",EDGE,"E7.6.5.1"),sQuery(id+"F0.wireOp",EDGE,"E7.6.5.2"),sQuery(id+"F0.wireOp",EDGE,"E7.6.5.3"),sQuery(id+"F0.wireOp",EDGE,"E7.7.0.0"),sQuery(id+"F0.wireOp",EDGE,"E7.7.0.1"),sQuery(id+"F0.wireOp",EDGE,"E7.7.0.2"),sQuery(id+"F0.wireOp",EDGE,"E7.7.0.3"),sQuery(id+"F0.wireOp",EDGE,"E7.7.1.0"),sQuery(id+"F0.wireOp",EDGE,"E7.7.1.1"),sQuery(id+"F0.wireOp",EDGE,"E7.7.1.2"),sQuery(id+"F0.wireOp",EDGE,"E7.7.1.3"),sQuery(id+"F0.wireOp",EDGE,"E7.7.2.0"),sQuery(id+"F0.wireOp",EDGE,"E7.7.2.1"),sQuery(id+"F0.wireOp",EDGE,"E7.7.2.2"),sQuery(id+"F0.wireOp",EDGE,"E7.7.2.3"),sQuery(id+"F0.wireOp",EDGE,"E7.7.3.0"),sQuery(id+"F0.wireOp",EDGE,"E7.7.3.1"),sQuery(id+"F0.wireOp",EDGE,"E7.7.3.2"),sQuery(id+"F0.wireOp",EDGE,"E7.7.3.3"),sQuery(id+"F0.wireOp",EDGE,"E7.7.4.0"),sQuery(id+"F0.wireOp",EDGE,"E7.7.4.1"),sQuery(id+"F0.wireOp",EDGE,"E7.7.4.2"),sQuery(id+"F0.wireOp",EDGE,"E7.7.4.3"),sQuery(id+"F0.wireOp",EDGE,"E7.7.5.0"),sQuery(id+"F0.wireOp",EDGE,"E7.7.5.1"),sQuery(id+"F0.wireOp",EDGE,"E7.7.5.2"),sQuery(id+"F0.wireOp",EDGE,"E7.7.5.3"),sQuery(id+"F0.wireOp",EDGE,"E7.8.0.0"),sQuery(id+"F0.wireOp",EDGE,"E7.8.0.1"),sQuery(id+"F0.wireOp",EDGE,"E7.8.0.2"),sQuery(id+"F0.wireOp",EDGE,"E7.8.0.3"),sQuery(id+"F0.wireOp",EDGE,"E7.8.1.0"),sQuery(id+"F0.wireOp",EDGE,"E7.8.1.1"),sQuery(id+"F0.wireOp",EDGE,"E7.8.1.2"),sQuery(id+"F0.wireOp",EDGE,"E7.8.1.3"),sQuery(id+"F0.wireOp",EDGE,"E7.8.2.0"),sQuery(id+"F0.wireOp",EDGE,"E7.8.2.1"),sQuery(id+"F0.wireOp",EDGE,"E7.8.2.2"),sQuery(id+"F0.wireOp",EDGE,"E7.8.2.3"),sQuery(id+"F0.wireOp",EDGE,"E7.8.3.0"),sQuery(id+"F0.wireOp",EDGE,"E7.8.3.1"),sQuery(id+"F0.wireOp",EDGE,"E7.8.3.2"),sQuery(id+"F0.wireOp",EDGE,"E7.8.3.3"),sQuery(id+"F0.wireOp",EDGE,"E7.8.4.0"),sQuery(id+"F0.wireOp",EDGE,"E7.8.4.1"),sQuery(id+"F0.wireOp",EDGE,"E7.8.4.2"),sQuery(id+"F0.wireOp",EDGE,"E7.8.4.3"),sQuery(id+"F0.wireOp",EDGE,"E7.8.5.0"),sQuery(id+"F0.wireOp",EDGE,"E7.8.5.1"),sQuery(id+"F0.wireOp",EDGE,"E7.8.5.2"),sQuery(id+"F0.wireOp",EDGE,"E7.8.5.3"),sQuery(id+"F0.wireOp",EDGE,"E7.9.0.0"),sQuery(id+"F0.wireOp",EDGE,"E7.9.0.1"),sQuery(id+"F0.wireOp",EDGE,"E7.9.0.2"),sQuery(id+"F0.wireOp",EDGE,"E7.9.0.3"),sQuery(id+"F0.wireOp",EDGE,"E7.9.1.0"),sQuery(id+"F0.wireOp",EDGE,"E7.9.1.1"),sQuery(id+"F0.wireOp",EDGE,"E7.9.1.2"),sQuery(id+"F0.wireOp",EDGE,"E7.9.1.3"),sQuery(id+"F0.wireOp",EDGE,"E7.9.2.0"),sQuery(id+"F0.wireOp",EDGE,"E7.9.2.1"),sQuery(id+"F0.wireOp",EDGE,"E7.9.2.2"),sQuery(id+"F0.wireOp",EDGE,"E7.9.2.3"),sQuery(id+"F0.wireOp",EDGE,"E7.9.3.0"),sQuery(id+"F0.wireOp",EDGE,"E7.9.3.1"),sQuery(id+"F0.wireOp",EDGE,"E7.9.3.2"),sQuery(id+"F0.wireOp",EDGE,"E7.9.3.3"),sQuery(id+"F0.wireOp",EDGE,"E7.9.4.0"),sQuery(id+"F0.wireOp",EDGE,"E7.9.4.1"),sQuery(id+"F0.wireOp",EDGE,"E7.9.4.2"),sQuery(id+"F0.wireOp",EDGE,"E7.9.4.3"),sQuery(id+"F0.wireOp",EDGE,"E7.9.5.0"),sQuery(id+"F0.wireOp",EDGE,"E7.9.5.1"),sQuery(id+"F0.wireOp",EDGE,"E7.9.5.2"),sQuery(id+"F0.wireOp",EDGE,"E7.9.5.3"),sQuery(id+"F0.wireOp",EDGE,"E7.10.0.0"),sQuery(id+"F0.wireOp",EDGE,"E7.10.0.1"),sQuery(id+"F0.wireOp",EDGE,"E7.10.0.2"),sQuery(id+"F0.wireOp",EDGE,"E7.10.0.3"),sQuery(id+"F0.wireOp",EDGE,"E7.10.1.0"),sQuery(id+"F0.wireOp",EDGE,"E7.10.1.1"),sQuery(id+"F0.wireOp",EDGE,"E7.10.1.2"),sQuery(id+"F0.wireOp",EDGE,"E7.10.1.3"),sQuery(id+"F0.wireOp",EDGE,"E7.10.2.0"),sQuery(id+"F0.wireOp",EDGE,"E7.10.2.1"),sQuery(id+"F0.wireOp",EDGE,"E7.10.2.2"),sQuery(id+"F0.wireOp",EDGE,"E7.10.2.3"),sQuery(id+"F0.wireOp",EDGE,"E7.10.3.0"),sQuery(id+"F0.wireOp",EDGE,"E7.10.3.1"),sQuery(id+"F0.wireOp",EDGE,"E7.10.3.2"),sQuery(id+"F0.wireOp",EDGE,"E7.10.3.3"),sQuery(id+"F0.wireOp",EDGE,"E7.10.4.0"),sQuery(id+"F0.wireOp",EDGE,"E7.10.4.1"),sQuery(id+"F0.wireOp",EDGE,"E7.10.4.2"),sQuery(id+"F0.wireOp",EDGE,"E7.10.4.3"),sQuery(id+"F0.wireOp",EDGE,"E7.10.5.0"),sQuery(id+"F0.wireOp",EDGE,"E7.10.5.1"),sQuery(id+"F0.wireOp",EDGE,"E7.10.5.2"),sQuery(id+"F0.wireOp",EDGE,"E7.10.5.3"),sQuery(id+"F0.wireOp",EDGE,"E7.11.0.0"),sQuery(id+"F0.wireOp",EDGE,"E7.11.0.1"),sQuery(id+"F0.wireOp",EDGE,"E7.11.0.2"),sQuery(id+"F0.wireOp",EDGE,"E7.11.0.3"),sQuery(id+"F0.wireOp",EDGE,"E7.11.1.0"),sQuery(id+"F0.wireOp",EDGE,"E7.11.1.1"),sQuery(id+"F0.wireOp",EDGE,"E7.11.1.2"),sQuery(id+"F0.wireOp",EDGE,"E7.11.1.3"),sQuery(id+"F0.wireOp",EDGE,"E7.11.2.0"),sQuery(id+"F0.wireOp",EDGE,"E7.11.2.1"),sQuery(id+"F0.wireOp",EDGE,"E7.11.2.2"),sQuery(id+"F0.wireOp",EDGE,"E7.11.2.3"),sQuery(id+"F0.wireOp",EDGE,"E7.11.3.0"),sQuery(id+"F0.wireOp",EDGE,"E7.11.3.1"),sQuery(id+"F0.wireOp",EDGE,"E7.11.3.2"),sQuery(id+"F0.wireOp",EDGE,"E7.11.3.3"),sQuery(id+"F0.wireOp",EDGE,"E7.11.4.0"),sQuery(id+"F0.wireOp",EDGE,"E7.11.4.1"),sQuery(id+"F0.wireOp",EDGE,"E7.11.4.2"),sQuery(id+"F0.wireOp",EDGE,"E7.11.4.3"),sQuery(id+"F0.wireOp",EDGE,"E7.11.5.0"),sQuery(id+"F0.wireOp",EDGE,"E7.11.5.1"),sQuery(id+"F0.wireOp",EDGE,"E7.11.5.2"),sQuery(id+"F0.wireOp",EDGE,"E7.11.5.3")])],"isStart":false});
            var sketch = newSketch(context, id + "F4", { "sketchPlane" : qUnion([Q0])});
            skLineSegment(sketch, "E12.bottom", {"start": v(-111.79, 142.74) * mm, "end": v(-91.79, 142.74) * mm});
            skLineSegment(sketch, "E12.top", {"start": v(-111.79, -67.26) * mm, "end": v(-91.79, -67.26) * mm});
            skLineSegment(sketch, "E12.left", {"start": v(-111.79, 142.74) * mm, "end": v(-111.79, -67.26) * mm});
            skLineSegment(sketch, "E12.right", {"start": v(-91.79, 142.74) * mm, "end": v(-91.79, -67.26) * mm});
            skLineSegment(sketch, "E13", {"start": v(-1.79, 157.74) * mm, "end": v(-1.79, -82.26) * mm, "construction": true});
            skLineSegment(sketch, "E14.MirrorCS", {"start": v(108.21, -67.26) * mm, "end": v(88.21, -67.26) * mm});
            skLineSegment(sketch, "E15.MirrorCS", {"start": v(88.21, 142.74) * mm, "end": v(88.21, -67.26) * mm});
            skLineSegment(sketch, "E16.MirrorCS", {"start": v(108.21, 142.74) * mm, "end": v(88.21, 142.74) * mm});
            skLineSegment(sketch, "E17.MirrorCS", {"start": v(108.21, 142.74) * mm, "end": v(108.21, -67.26) * mm});
            skSolve(sketch);
        }
        {
            var Q0;
            {var subQ47=sQuery(id+"F4.wireOp",EDGE,"E12.bottom");Q0=makeQuery(id+"F4.imprint","IMPRINT",FACE,{"disambiguationData":[TD([[makeQuery(id+"F4.imprint","IMPRINT",EDGE,{"derivedFrom":subQ47}),-1.0]])]});}
            var Q1;
            {var subQ36=sQuery(id+"F4.wireOp",EDGE,"E14.MirrorCS");Q1=makeQuery(id+"F4.imprint","IMPRINT",FACE,{"disambiguationData":[TD([[makeQuery(id+"F4.imprint","IMPRINT",EDGE,{"derivedFrom":subQ36}),-1.0]])]});}
            extrude(context, id + "F5", {"entities" : qUnion([Q0, Q1]), "operationType" : NewBodyOperationType.REMOVE, "endBound" : BoundingType.THROUGH_ALL, "oppositeDirection" : true, "depth" : 25 * mm});
        }
        {
            var Q0;
            Q0=makeQuery(id+"F1.opExtrude","CAP_FACE",FACE,{"disambiguationData":[OSD([sQuery(id+"F0.wireOp",EDGE,"E0.bottom"),sQuery(id+"F0.wireOp",EDGE,"E0.top"),sQuery(id+"F0.wireOp",EDGE,"E0.left"),sQuery(id+"F0.wireOp",EDGE,"E0.right"),sQuery(id+"F0.wireOp",EDGE,"E1.bottom"),sQuery(id+"F0.wireOp",EDGE,"E1.top"),sQuery(id+"F0.wireOp",EDGE,"E1.left"),sQuery(id+"F0.wireOp",EDGE,"E1.right"),sQuery(id+"F0.wireOp",EDGE,"E4.3.1.0"),sQuery(id+"F0.wireOp",EDGE,"E4.6.1.0"),sQuery(id+"F0.wireOp",EDGE,"E4.9.1.0"),sQuery(id+"F0.wireOp",EDGE,"E4.12.1.0"),sQuery(id+"F0.wireOp",EDGE,"E4.3.2.0"),sQuery(id+"F0.wireOp",EDGE,"E4.6.2.0"),sQuery(id+"F0.wireOp",EDGE,"E4.9.2.0"),sQuery(id+"F0.wireOp",EDGE,"E4.12.2.0"),sQuery(id+"F0.wireOp",EDGE,"E4.3.3.0"),sQuery(id+"F0.wireOp",EDGE,"E4.6.3.0"),sQuery(id+"F0.wireOp",EDGE,"E4.9.3.0"),sQuery(id+"F0.wireOp",EDGE,"E4.12.3.0"),sQuery(id+"F0.wireOp",EDGE,"E4.3.4.0"),sQuery(id+"F0.wireOp",EDGE,"E4.6.4.0"),sQuery(id+"F0.wireOp",EDGE,"E4.9.4.0"),sQuery(id+"F0.wireOp",EDGE,"E4.12.4.0"),sQuery(id+"F0.wireOp",EDGE,"E4.3.5.0"),sQuery(id+"F0.wireOp",EDGE,"E4.6.5.0"),sQuery(id+"F0.wireOp",EDGE,"E4.9.5.0"),sQuery(id+"F0.wireOp",EDGE,"E4.12.5.0"),sQuery(id+"F0.wireOp",EDGE,"E4.3.6.0"),sQuery(id+"F0.wireOp",EDGE,"E4.6.6.0"),sQuery(id+"F0.wireOp",EDGE,"E4.9.6.0"),sQuery(id+"F0.wireOp",EDGE,"E4.12.6.0"),sQuery(id+"F0.wireOp",EDGE,"E4.3.7.0"),sQuery(id+"F0.wireOp",EDGE,"E4.6.7.0"),sQuery(id+"F0.wireOp",EDGE,"E4.9.7.0"),sQuery(id+"F0.wireOp",EDGE,"E4.12.7.0"),sQuery(id+"F0.wireOp",EDGE,"E4.3.8.0"),sQuery(id+"F0.wireOp",EDGE,"E4.6.8.0"),sQuery(id+"F0.wireOp",EDGE,"E4.9.8.0"),sQuery(id+"F0.wireOp",EDGE,"E4.12.8.0"),sQuery(id+"F0.wireOp",EDGE,"E4.3.9.0"),sQuery(id+"F0.wireOp",EDGE,"E4.6.9.0"),sQuery(id+"F0.wireOp",EDGE,"E4.9.9.0"),sQuery(id+"F0.wireOp",EDGE,"E4.12.9.0"),sQuery(id+"F0.wireOp",EDGE,"E4.3.10.0"),sQuery(id+"F0.wireOp",EDGE,"E4.6.10.0"),sQuery(id+"F0.wireOp",EDGE,"E4.9.10.0"),sQuery(id+"F0.wireOp",EDGE,"E4.12.10.0"),sQuery(id+"F0.wireOp",EDGE,"E4.3.11.0"),sQuery(id+"F0.wireOp",EDGE,"E4.6.11.0"),sQuery(id+"F0.wireOp",EDGE,"E4.9.11.0"),sQuery(id+"F0.wireOp",EDGE,"E4.12.11.0"),sQuery(id+"F0.wireOp",EDGE,"E5.3.0.1"),sQuery(id+"F0.wireOp",EDGE,"E5.6.0.1"),sQuery(id+"F0.wireOp",EDGE,"E5.9.0.1"),sQuery(id+"F0.wireOp",EDGE,"E5.12.0.1"),sQuery(id+"F0.wireOp",EDGE,"E5.3.0.2"),sQuery(id+"F0.wireOp",EDGE,"E5.6.0.2"),sQuery(id+"F0.wireOp",EDGE,"E5.9.0.2"),sQuery(id+"F0.wireOp",EDGE,"E5.12.0.2"),sQuery(id+"F0.wireOp",EDGE,"E5.3.0.3"),sQuery(id+"F0.wireOp",EDGE,"E5.6.0.3"),sQuery(id+"F0.wireOp",EDGE,"E5.9.0.3"),sQuery(id+"F0.wireOp",EDGE,"E5.12.0.3"),sQuery(id+"F0.wireOp",EDGE,"E5.3.0.4"),sQuery(id+"F0.wireOp",EDGE,"E5.6.0.4"),sQuery(id+"F0.wireOp",EDGE,"E5.9.0.4"),sQuery(id+"F0.wireOp",EDGE,"E5.12.0.4"),sQuery(id+"F0.wireOp",EDGE,"E5.3.0.5"),sQuery(id+"F0.wireOp",EDGE,"E5.6.0.5"),sQuery(id+"F0.wireOp",EDGE,"E5.9.0.5"),sQuery(id+"F0.wireOp",EDGE,"E5.12.0.5"),sQuery(id+"F0.wireOp",EDGE,"E5.3.1.1"),sQuery(id+"F0.wireOp",EDGE,"E5.6.1.1"),sQuery(id+"F0.wireOp",EDGE,"E5.9.1.1"),sQuery(id+"F0.wireOp",EDGE,"E5.12.1.1"),sQuery(id+"F0.wireOp",EDGE,"E5.3.1.2"),sQuery(id+"F0.wireOp",EDGE,"E5.6.1.2"),sQuery(id+"F0.wireOp",EDGE,"E5.9.1.2"),sQuery(id+"F0.wireOp",EDGE,"E5.12.1.2"),sQuery(id+"F0.wireOp",EDGE,"E5.3.1.3"),sQuery(id+"F0.wireOp",EDGE,"E5.6.1.3"),sQuery(id+"F0.wireOp",EDGE,"E5.9.1.3"),sQuery(id+"F0.wireOp",EDGE,"E5.12.1.3"),sQuery(id+"F0.wireOp",EDGE,"E5.3.1.4"),sQuery(id+"F0.wireOp",EDGE,"E5.6.1.4"),sQuery(id+"F0.wireOp",EDGE,"E5.9.1.4"),sQuery(id+"F0.wireOp",EDGE,"E5.12.1.4"),sQuery(id+"F0.wireOp",EDGE,"E5.3.1.5"),sQuery(id+"F0.wireOp",EDGE,"E5.6.1.5"),sQuery(id+"F0.wireOp",EDGE,"E5.9.1.5"),sQuery(id+"F0.wireOp",EDGE,"E5.12.1.5"),sQuery(id+"F0.wireOp",EDGE,"E5.3.2.1"),sQuery(id+"F0.wireOp",EDGE,"E5.6.2.1"),sQuery(id+"F0.wireOp",EDGE,"E5.9.2.1"),sQuery(id+"F0.wireOp",EDGE,"E5.12.2.1"),sQuery(id+"F0.wireOp",EDGE,"E5.3.2.2"),sQuery(id+"F0.wireOp",EDGE,"E5.6.2.2"),sQuery(id+"F0.wireOp",EDGE,"E5.9.2.2"),sQuery(id+"F0.wireOp",EDGE,"E5.12.2.2"),sQuery(id+"F0.wireOp",EDGE,"E5.3.2.3"),sQuery(id+"F0.wireOp",EDGE,"E5.6.2.3"),sQuery(id+"F0.wireOp",EDGE,"E5.9.2.3"),sQuery(id+"F0.wireOp",EDGE,"E5.12.2.3"),sQuery(id+"F0.wireOp",EDGE,"E5.3.2.4"),sQuery(id+"F0.wireOp",EDGE,"E5.6.2.4"),sQuery(id+"F0.wireOp",EDGE,"E5.9.2.4"),sQuery(id+"F0.wireOp",EDGE,"E5.12.2.4"),sQuery(id+"F0.wireOp",EDGE,"E5.3.2.5"),sQuery(id+"F0.wireOp",EDGE,"E5.6.2.5"),sQuery(id+"F0.wireOp",EDGE,"E5.9.2.5"),sQuery(id+"F0.wireOp",EDGE,"E5.12.2.5"),sQuery(id+"F0.wireOp",EDGE,"E5.3.3.1"),sQuery(id+"F0.wireOp",EDGE,"E5.6.3.1"),sQuery(id+"F0.wireOp",EDGE,"E5.9.3.1"),sQuery(id+"F0.wireOp",EDGE,"E5.12.3.1"),sQuery(id+"F0.wireOp",EDGE,"E5.3.3.2"),sQuery(id+"F0.wireOp",EDGE,"E5.6.3.2"),sQuery(id+"F0.wireOp",EDGE,"E5.9.3.2"),sQuery(id+"F0.wireOp",EDGE,"E5.12.3.2"),sQuery(id+"F0.wireOp",EDGE,"E5.3.3.3"),sQuery(id+"F0.wireOp",EDGE,"E5.6.3.3"),sQuery(id+"F0.wireOp",EDGE,"E5.9.3.3"),sQuery(id+"F0.wireOp",EDGE,"E5.12.3.3"),sQuery(id+"F0.wireOp",EDGE,"E5.3.3.4"),sQuery(id+"F0.wireOp",EDGE,"E5.6.3.4"),sQuery(id+"F0.wireOp",EDGE,"E5.9.3.4"),sQuery(id+"F0.wireOp",EDGE,"E5.12.3.4"),sQuery(id+"F0.wireOp",EDGE,"E5.3.3.5"),sQuery(id+"F0.wireOp",EDGE,"E5.6.3.5"),sQuery(id+"F0.wireOp",EDGE,"E5.9.3.5"),sQuery(id+"F0.wireOp",EDGE,"E5.12.3.5"),sQuery(id+"F0.wireOp",EDGE,"E5.3.4.1"),sQuery(id+"F0.wireOp",EDGE,"E5.6.4.1"),sQuery(id+"F0.wireOp",EDGE,"E5.9.4.1"),sQuery(id+"F0.wireOp",EDGE,"E5.12.4.1"),sQuery(id+"F0.wireOp",EDGE,"E5.3.4.2"),sQuery(id+"F0.wireOp",EDGE,"E5.6.4.2"),sQuery(id+"F0.wireOp",EDGE,"E5.9.4.2"),sQuery(id+"F0.wireOp",EDGE,"E5.12.4.2"),sQuery(id+"F0.wireOp",EDGE,"E5.3.4.3"),sQuery(id+"F0.wireOp",EDGE,"E5.6.4.3"),sQuery(id+"F0.wireOp",EDGE,"E5.9.4.3"),sQuery(id+"F0.wireOp",EDGE,"E5.12.4.3"),sQuery(id+"F0.wireOp",EDGE,"E5.3.4.4"),sQuery(id+"F0.wireOp",EDGE,"E5.6.4.4"),sQuery(id+"F0.wireOp",EDGE,"E5.9.4.4"),sQuery(id+"F0.wireOp",EDGE,"E5.12.4.4"),sQuery(id+"F0.wireOp",EDGE,"E5.3.4.5"),sQuery(id+"F0.wireOp",EDGE,"E5.6.4.5"),sQuery(id+"F0.wireOp",EDGE,"E5.9.4.5"),sQuery(id+"F0.wireOp",EDGE,"E5.12.4.5"),sQuery(id+"F0.wireOp",EDGE,"E5.3.5.1"),sQuery(id+"F0.wireOp",EDGE,"E5.6.5.1"),sQuery(id+"F0.wireOp",EDGE,"E5.9.5.1"),sQuery(id+"F0.wireOp",EDGE,"E5.12.5.1"),sQuery(id+"F0.wireOp",EDGE,"E5.3.5.2"),sQuery(id+"F0.wireOp",EDGE,"E5.6.5.2"),sQuery(id+"F0.wireOp",EDGE,"E5.9.5.2"),sQuery(id+"F0.wireOp",EDGE,"E5.12.5.2"),sQuery(id+"F0.wireOp",EDGE,"E5.3.5.3"),sQuery(id+"F0.wireOp",EDGE,"E5.6.5.3"),sQuery(id+"F0.wireOp",EDGE,"E5.9.5.3"),sQuery(id+"F0.wireOp",EDGE,"E5.12.5.3"),sQuery(id+"F0.wireOp",EDGE,"E5.3.5.4"),sQuery(id+"F0.wireOp",EDGE,"E5.6.5.4"),sQuery(id+"F0.wireOp",EDGE,"E5.9.5.4"),sQuery(id+"F0.wireOp",EDGE,"E5.12.5.4"),sQuery(id+"F0.wireOp",EDGE,"E5.3.5.5"),sQuery(id+"F0.wireOp",EDGE,"E5.6.5.5"),sQuery(id+"F0.wireOp",EDGE,"E5.9.5.5"),sQuery(id+"F0.wireOp",EDGE,"E5.12.5.5"),sQuery(id+"F0.wireOp",EDGE,"E5.3.6.1"),sQuery(id+"F0.wireOp",EDGE,"E5.6.6.1"),sQuery(id+"F0.wireOp",EDGE,"E5.9.6.1"),sQuery(id+"F0.wireOp",EDGE,"E5.12.6.1"),sQuery(id+"F0.wireOp",EDGE,"E5.3.6.2"),sQuery(id+"F0.wireOp",EDGE,"E5.6.6.2"),sQuery(id+"F0.wireOp",EDGE,"E5.9.6.2"),sQuery(id+"F0.wireOp",EDGE,"E5.12.6.2"),sQuery(id+"F0.wireOp",EDGE,"E5.3.6.3"),sQuery(id+"F0.wireOp",EDGE,"E5.6.6.3"),sQuery(id+"F0.wireOp",EDGE,"E5.9.6.3"),sQuery(id+"F0.wireOp",EDGE,"E5.12.6.3"),sQuery(id+"F0.wireOp",EDGE,"E5.3.6.4"),sQuery(id+"F0.wireOp",EDGE,"E5.6.6.4"),sQuery(id+"F0.wireOp",EDGE,"E5.9.6.4"),sQuery(id+"F0.wireOp",EDGE,"E5.12.6.4"),sQuery(id+"F0.wireOp",EDGE,"E5.3.6.5"),sQuery(id+"F0.wireOp",EDGE,"E5.6.6.5"),sQuery(id+"F0.wireOp",EDGE,"E5.9.6.5"),sQuery(id+"F0.wireOp",EDGE,"E5.12.6.5"),sQuery(id+"F0.wireOp",EDGE,"E5.3.7.1"),sQuery(id+"F0.wireOp",EDGE,"E5.6.7.1"),sQuery(id+"F0.wireOp",EDGE,"E5.9.7.1"),sQuery(id+"F0.wireOp",EDGE,"E5.12.7.1"),sQuery(id+"F0.wireOp",EDGE,"E5.3.7.2"),sQuery(id+"F0.wireOp",EDGE,"E5.6.7.2"),sQuery(id+"F0.wireOp",EDGE,"E5.9.7.2"),sQuery(id+"F0.wireOp",EDGE,"E5.12.7.2"),sQuery(id+"F0.wireOp",EDGE,"E5.3.7.3"),sQuery(id+"F0.wireOp",EDGE,"E5.6.7.3"),sQuery(id+"F0.wireOp",EDGE,"E5.9.7.3"),sQuery(id+"F0.wireOp",EDGE,"E5.12.7.3"),sQuery(id+"F0.wireOp",EDGE,"E5.3.7.4"),sQuery(id+"F0.wireOp",EDGE,"E5.6.7.4"),sQuery(id+"F0.wireOp",EDGE,"E5.9.7.4"),sQuery(id+"F0.wireOp",EDGE,"E5.12.7.4"),sQuery(id+"F0.wireOp",EDGE,"E5.3.7.5"),sQuery(id+"F0.wireOp",EDGE,"E5.6.7.5"),sQuery(id+"F0.wireOp",EDGE,"E5.9.7.5"),sQuery(id+"F0.wireOp",EDGE,"E5.12.7.5"),sQuery(id+"F0.wireOp",EDGE,"E5.3.8.1"),sQuery(id+"F0.wireOp",EDGE,"E5.6.8.1"),sQuery(id+"F0.wireOp",EDGE,"E5.9.8.1"),sQuery(id+"F0.wireOp",EDGE,"E5.12.8.1"),sQuery(id+"F0.wireOp",EDGE,"E5.3.8.2"),sQuery(id+"F0.wireOp",EDGE,"E5.6.8.2"),sQuery(id+"F0.wireOp",EDGE,"E5.9.8.2"),sQuery(id+"F0.wireOp",EDGE,"E5.12.8.2"),sQuery(id+"F0.wireOp",EDGE,"E5.3.8.3"),sQuery(id+"F0.wireOp",EDGE,"E5.6.8.3"),sQuery(id+"F0.wireOp",EDGE,"E5.9.8.3"),sQuery(id+"F0.wireOp",EDGE,"E5.12.8.3"),sQuery(id+"F0.wireOp",EDGE,"E5.3.8.4"),sQuery(id+"F0.wireOp",EDGE,"E5.6.8.4"),sQuery(id+"F0.wireOp",EDGE,"E5.9.8.4"),sQuery(id+"F0.wireOp",EDGE,"E5.12.8.4"),sQuery(id+"F0.wireOp",EDGE,"E5.3.8.5"),sQuery(id+"F0.wireOp",EDGE,"E5.6.8.5"),sQuery(id+"F0.wireOp",EDGE,"E5.9.8.5"),sQuery(id+"F0.wireOp",EDGE,"E5.12.8.5"),sQuery(id+"F0.wireOp",EDGE,"E5.3.9.1"),sQuery(id+"F0.wireOp",EDGE,"E5.6.9.1"),sQuery(id+"F0.wireOp",EDGE,"E5.9.9.1"),sQuery(id+"F0.wireOp",EDGE,"E5.12.9.1"),sQuery(id+"F0.wireOp",EDGE,"E5.3.9.2"),sQuery(id+"F0.wireOp",EDGE,"E5.6.9.2"),sQuery(id+"F0.wireOp",EDGE,"E5.9.9.2"),sQuery(id+"F0.wireOp",EDGE,"E5.12.9.2"),sQuery(id+"F0.wireOp",EDGE,"E5.3.9.3"),sQuery(id+"F0.wireOp",EDGE,"E5.6.9.3"),sQuery(id+"F0.wireOp",EDGE,"E5.9.9.3"),sQuery(id+"F0.wireOp",EDGE,"E5.12.9.3"),sQuery(id+"F0.wireOp",EDGE,"E5.3.9.4"),sQuery(id+"F0.wireOp",EDGE,"E5.6.9.4"),sQuery(id+"F0.wireOp",EDGE,"E5.9.9.4"),sQuery(id+"F0.wireOp",EDGE,"E5.12.9.4"),sQuery(id+"F0.wireOp",EDGE,"E5.3.9.5"),sQuery(id+"F0.wireOp",EDGE,"E5.6.9.5"),sQuery(id+"F0.wireOp",EDGE,"E5.9.9.5"),sQuery(id+"F0.wireOp",EDGE,"E5.12.9.5"),sQuery(id+"F0.wireOp",EDGE,"E5.3.10.1"),sQuery(id+"F0.wireOp",EDGE,"E5.6.10.1"),sQuery(id+"F0.wireOp",EDGE,"E5.9.10.1"),sQuery(id+"F0.wireOp",EDGE,"E5.12.10.1"),sQuery(id+"F0.wireOp",EDGE,"E5.3.10.2"),sQuery(id+"F0.wireOp",EDGE,"E5.6.10.2"),sQuery(id+"F0.wireOp",EDGE,"E5.9.10.2"),sQuery(id+"F0.wireOp",EDGE,"E5.12.10.2"),sQuery(id+"F0.wireOp",EDGE,"E5.3.10.3"),sQuery(id+"F0.wireOp",EDGE,"E5.6.10.3"),sQuery(id+"F0.wireOp",EDGE,"E5.9.10.3"),sQuery(id+"F0.wireOp",EDGE,"E5.12.10.3"),sQuery(id+"F0.wireOp",EDGE,"E5.3.10.4"),sQuery(id+"F0.wireOp",EDGE,"E5.6.10.4"),sQuery(id+"F0.wireOp",EDGE,"E5.9.10.4"),sQuery(id+"F0.wireOp",EDGE,"E5.12.10.4"),sQuery(id+"F0.wireOp",EDGE,"E5.3.10.5"),sQuery(id+"F0.wireOp",EDGE,"E5.6.10.5"),sQuery(id+"F0.wireOp",EDGE,"E5.9.10.5"),sQuery(id+"F0.wireOp",EDGE,"E5.12.10.5"),sQuery(id+"F0.wireOp",EDGE,"E5.3.11.1"),sQuery(id+"F0.wireOp",EDGE,"E5.6.11.1"),sQuery(id+"F0.wireOp",EDGE,"E5.9.11.1"),sQuery(id+"F0.wireOp",EDGE,"E5.12.11.1"),sQuery(id+"F0.wireOp",EDGE,"E5.3.11.2"),sQuery(id+"F0.wireOp",EDGE,"E5.6.11.2"),sQuery(id+"F0.wireOp",EDGE,"E5.9.11.2"),sQuery(id+"F0.wireOp",EDGE,"E5.12.11.2"),sQuery(id+"F0.wireOp",EDGE,"E5.3.11.3"),sQuery(id+"F0.wireOp",EDGE,"E5.6.11.3"),sQuery(id+"F0.wireOp",EDGE,"E5.9.11.3"),sQuery(id+"F0.wireOp",EDGE,"E5.12.11.3"),sQuery(id+"F0.wireOp",EDGE,"E5.3.11.4"),sQuery(id+"F0.wireOp",EDGE,"E5.6.11.4"),sQuery(id+"F0.wireOp",EDGE,"E5.9.11.4"),sQuery(id+"F0.wireOp",EDGE,"E5.12.11.4"),sQuery(id+"F0.wireOp",EDGE,"E5.3.11.5"),sQuery(id+"F0.wireOp",EDGE,"E5.6.11.5"),sQuery(id+"F0.wireOp",EDGE,"E5.9.11.5"),sQuery(id+"F0.wireOp",EDGE,"E5.12.11.5"),sQuery(id+"F0.wireOp",EDGE,"E6.bottom"),sQuery(id+"F0.wireOp",EDGE,"E6.top"),sQuery(id+"F0.wireOp",EDGE,"E6.left"),sQuery(id+"F0.wireOp",EDGE,"E6.right"),sQuery(id+"F0.wireOp",EDGE,"E7.0.1.0"),sQuery(id+"F0.wireOp",EDGE,"E7.0.1.1"),sQuery(id+"F0.wireOp",EDGE,"E7.0.1.2"),sQuery(id+"F0.wireOp",EDGE,"E7.0.1.3"),sQuery(id+"F0.wireOp",EDGE,"E7.0.2.0"),sQuery(id+"F0.wireOp",EDGE,"E7.0.2.1"),sQuery(id+"F0.wireOp",EDGE,"E7.0.2.2"),sQuery(id+"F0.wireOp",EDGE,"E7.0.2.3"),sQuery(id+"F0.wireOp",EDGE,"E7.0.3.0"),sQuery(id+"F0.wireOp",EDGE,"E7.0.3.1"),sQuery(id+"F0.wireOp",EDGE,"E7.0.3.2"),sQuery(id+"F0.wireOp",EDGE,"E7.0.3.3"),sQuery(id+"F0.wireOp",EDGE,"E7.0.4.0"),sQuery(id+"F0.wireOp",EDGE,"E7.0.4.1"),sQuery(id+"F0.wireOp",EDGE,"E7.0.4.2"),sQuery(id+"F0.wireOp",EDGE,"E7.0.4.3"),sQuery(id+"F0.wireOp",EDGE,"E7.0.5.0"),sQuery(id+"F0.wireOp",EDGE,"E7.0.5.1"),sQuery(id+"F0.wireOp",EDGE,"E7.0.5.2"),sQuery(id+"F0.wireOp",EDGE,"E7.0.5.3"),sQuery(id+"F0.wireOp",EDGE,"E7.1.0.0"),sQuery(id+"F0.wireOp",EDGE,"E7.1.0.1"),sQuery(id+"F0.wireOp",EDGE,"E7.1.0.2"),sQuery(id+"F0.wireOp",EDGE,"E7.1.0.3"),sQuery(id+"F0.wireOp",EDGE,"E7.1.1.0"),sQuery(id+"F0.wireOp",EDGE,"E7.1.1.1"),sQuery(id+"F0.wireOp",EDGE,"E7.1.1.2"),sQuery(id+"F0.wireOp",EDGE,"E7.1.1.3"),sQuery(id+"F0.wireOp",EDGE,"E7.1.2.0"),sQuery(id+"F0.wireOp",EDGE,"E7.1.2.1"),sQuery(id+"F0.wireOp",EDGE,"E7.1.2.2"),sQuery(id+"F0.wireOp",EDGE,"E7.1.2.3"),sQuery(id+"F0.wireOp",EDGE,"E7.1.3.0"),sQuery(id+"F0.wireOp",EDGE,"E7.1.3.1"),sQuery(id+"F0.wireOp",EDGE,"E7.1.3.2"),sQuery(id+"F0.wireOp",EDGE,"E7.1.3.3"),sQuery(id+"F0.wireOp",EDGE,"E7.1.4.0"),sQuery(id+"F0.wireOp",EDGE,"E7.1.4.1"),sQuery(id+"F0.wireOp",EDGE,"E7.1.4.2"),sQuery(id+"F0.wireOp",EDGE,"E7.1.4.3"),sQuery(id+"F0.wireOp",EDGE,"E7.1.5.0"),sQuery(id+"F0.wireOp",EDGE,"E7.1.5.1"),sQuery(id+"F0.wireOp",EDGE,"E7.1.5.2"),sQuery(id+"F0.wireOp",EDGE,"E7.1.5.3"),sQuery(id+"F0.wireOp",EDGE,"E7.2.0.0"),sQuery(id+"F0.wireOp",EDGE,"E7.2.0.1"),sQuery(id+"F0.wireOp",EDGE,"E7.2.0.2"),sQuery(id+"F0.wireOp",EDGE,"E7.2.0.3"),sQuery(id+"F0.wireOp",EDGE,"E7.2.1.0"),sQuery(id+"F0.wireOp",EDGE,"E7.2.1.1"),sQuery(id+"F0.wireOp",EDGE,"E7.2.1.2"),sQuery(id+"F0.wireOp",EDGE,"E7.2.1.3"),sQuery(id+"F0.wireOp",EDGE,"E7.2.2.0"),sQuery(id+"F0.wireOp",EDGE,"E7.2.2.1"),sQuery(id+"F0.wireOp",EDGE,"E7.2.2.2"),sQuery(id+"F0.wireOp",EDGE,"E7.2.2.3"),sQuery(id+"F0.wireOp",EDGE,"E7.2.3.0"),sQuery(id+"F0.wireOp",EDGE,"E7.2.3.1"),sQuery(id+"F0.wireOp",EDGE,"E7.2.3.2"),sQuery(id+"F0.wireOp",EDGE,"E7.2.3.3"),sQuery(id+"F0.wireOp",EDGE,"E7.2.4.0"),sQuery(id+"F0.wireOp",EDGE,"E7.2.4.1"),sQuery(id+"F0.wireOp",EDGE,"E7.2.4.2"),sQuery(id+"F0.wireOp",EDGE,"E7.2.4.3"),sQuery(id+"F0.wireOp",EDGE,"E7.2.5.0"),sQuery(id+"F0.wireOp",EDGE,"E7.2.5.1"),sQuery(id+"F0.wireOp",EDGE,"E7.2.5.2"),sQuery(id+"F0.wireOp",EDGE,"E7.2.5.3"),sQuery(id+"F0.wireOp",EDGE,"E7.3.0.0"),sQuery(id+"F0.wireOp",EDGE,"E7.3.0.1"),sQuery(id+"F0.wireOp",EDGE,"E7.3.0.2"),sQuery(id+"F0.wireOp",EDGE,"E7.3.0.3"),sQuery(id+"F0.wireOp",EDGE,"E7.3.1.0"),sQuery(id+"F0.wireOp",EDGE,"E7.3.1.1"),sQuery(id+"F0.wireOp",EDGE,"E7.3.1.2"),sQuery(id+"F0.wireOp",EDGE,"E7.3.1.3"),sQuery(id+"F0.wireOp",EDGE,"E7.3.2.0"),sQuery(id+"F0.wireOp",EDGE,"E7.3.2.1"),sQuery(id+"F0.wireOp",EDGE,"E7.3.2.2"),sQuery(id+"F0.wireOp",EDGE,"E7.3.2.3"),sQuery(id+"F0.wireOp",EDGE,"E7.3.3.0"),sQuery(id+"F0.wireOp",EDGE,"E7.3.3.1"),sQuery(id+"F0.wireOp",EDGE,"E7.3.3.2"),sQuery(id+"F0.wireOp",EDGE,"E7.3.3.3"),sQuery(id+"F0.wireOp",EDGE,"E7.3.4.0"),sQuery(id+"F0.wireOp",EDGE,"E7.3.4.1"),sQuery(id+"F0.wireOp",EDGE,"E7.3.4.2"),sQuery(id+"F0.wireOp",EDGE,"E7.3.4.3"),sQuery(id+"F0.wireOp",EDGE,"E7.3.5.0"),sQuery(id+"F0.wireOp",EDGE,"E7.3.5.1"),sQuery(id+"F0.wireOp",EDGE,"E7.3.5.2"),sQuery(id+"F0.wireOp",EDGE,"E7.3.5.3"),sQuery(id+"F0.wireOp",EDGE,"E7.4.0.0"),sQuery(id+"F0.wireOp",EDGE,"E7.4.0.1"),sQuery(id+"F0.wireOp",EDGE,"E7.4.0.2"),sQuery(id+"F0.wireOp",EDGE,"E7.4.0.3"),sQuery(id+"F0.wireOp",EDGE,"E7.4.1.0"),sQuery(id+"F0.wireOp",EDGE,"E7.4.1.1"),sQuery(id+"F0.wireOp",EDGE,"E7.4.1.2"),sQuery(id+"F0.wireOp",EDGE,"E7.4.1.3"),sQuery(id+"F0.wireOp",EDGE,"E7.4.2.0"),sQuery(id+"F0.wireOp",EDGE,"E7.4.2.1"),sQuery(id+"F0.wireOp",EDGE,"E7.4.2.2"),sQuery(id+"F0.wireOp",EDGE,"E7.4.2.3"),sQuery(id+"F0.wireOp",EDGE,"E7.4.3.0"),sQuery(id+"F0.wireOp",EDGE,"E7.4.3.1"),sQuery(id+"F0.wireOp",EDGE,"E7.4.3.2"),sQuery(id+"F0.wireOp",EDGE,"E7.4.3.3"),sQuery(id+"F0.wireOp",EDGE,"E7.4.4.0"),sQuery(id+"F0.wireOp",EDGE,"E7.4.4.1"),sQuery(id+"F0.wireOp",EDGE,"E7.4.4.2"),sQuery(id+"F0.wireOp",EDGE,"E7.4.4.3"),sQuery(id+"F0.wireOp",EDGE,"E7.4.5.0"),sQuery(id+"F0.wireOp",EDGE,"E7.4.5.1"),sQuery(id+"F0.wireOp",EDGE,"E7.4.5.2"),sQuery(id+"F0.wireOp",EDGE,"E7.4.5.3"),sQuery(id+"F0.wireOp",EDGE,"E7.5.0.0"),sQuery(id+"F0.wireOp",EDGE,"E7.5.0.1"),sQuery(id+"F0.wireOp",EDGE,"E7.5.0.2"),sQuery(id+"F0.wireOp",EDGE,"E7.5.0.3"),sQuery(id+"F0.wireOp",EDGE,"E7.5.1.0"),sQuery(id+"F0.wireOp",EDGE,"E7.5.1.1"),sQuery(id+"F0.wireOp",EDGE,"E7.5.1.2"),sQuery(id+"F0.wireOp",EDGE,"E7.5.1.3"),sQuery(id+"F0.wireOp",EDGE,"E7.5.2.0"),sQuery(id+"F0.wireOp",EDGE,"E7.5.2.1"),sQuery(id+"F0.wireOp",EDGE,"E7.5.2.2"),sQuery(id+"F0.wireOp",EDGE,"E7.5.2.3"),sQuery(id+"F0.wireOp",EDGE,"E7.5.3.0"),sQuery(id+"F0.wireOp",EDGE,"E7.5.3.1"),sQuery(id+"F0.wireOp",EDGE,"E7.5.3.2"),sQuery(id+"F0.wireOp",EDGE,"E7.5.3.3"),sQuery(id+"F0.wireOp",EDGE,"E7.5.4.0"),sQuery(id+"F0.wireOp",EDGE,"E7.5.4.1"),sQuery(id+"F0.wireOp",EDGE,"E7.5.4.2"),sQuery(id+"F0.wireOp",EDGE,"E7.5.4.3"),sQuery(id+"F0.wireOp",EDGE,"E7.5.5.0"),sQuery(id+"F0.wireOp",EDGE,"E7.5.5.1"),sQuery(id+"F0.wireOp",EDGE,"E7.5.5.2"),sQuery(id+"F0.wireOp",EDGE,"E7.5.5.3"),sQuery(id+"F0.wireOp",EDGE,"E7.6.0.0"),sQuery(id+"F0.wireOp",EDGE,"E7.6.0.1"),sQuery(id+"F0.wireOp",EDGE,"E7.6.0.2"),sQuery(id+"F0.wireOp",EDGE,"E7.6.0.3"),sQuery(id+"F0.wireOp",EDGE,"E7.6.1.0"),sQuery(id+"F0.wireOp",EDGE,"E7.6.1.1"),sQuery(id+"F0.wireOp",EDGE,"E7.6.1.2"),sQuery(id+"F0.wireOp",EDGE,"E7.6.1.3"),sQuery(id+"F0.wireOp",EDGE,"E7.6.2.0"),sQuery(id+"F0.wireOp",EDGE,"E7.6.2.1"),sQuery(id+"F0.wireOp",EDGE,"E7.6.2.2"),sQuery(id+"F0.wireOp",EDGE,"E7.6.2.3"),sQuery(id+"F0.wireOp",EDGE,"E7.6.3.0"),sQuery(id+"F0.wireOp",EDGE,"E7.6.3.1"),sQuery(id+"F0.wireOp",EDGE,"E7.6.3.2"),sQuery(id+"F0.wireOp",EDGE,"E7.6.3.3"),sQuery(id+"F0.wireOp",EDGE,"E7.6.4.0"),sQuery(id+"F0.wireOp",EDGE,"E7.6.4.1"),sQuery(id+"F0.wireOp",EDGE,"E7.6.4.2"),sQuery(id+"F0.wireOp",EDGE,"E7.6.4.3"),sQuery(id+"F0.wireOp",EDGE,"E7.6.5.0"),sQuery(id+"F0.wireOp",EDGE,"E7.6.5.1"),sQuery(id+"F0.wireOp",EDGE,"E7.6.5.2"),sQuery(id+"F0.wireOp",EDGE,"E7.6.5.3"),sQuery(id+"F0.wireOp",EDGE,"E7.7.0.0"),sQuery(id+"F0.wireOp",EDGE,"E7.7.0.1"),sQuery(id+"F0.wireOp",EDGE,"E7.7.0.2"),sQuery(id+"F0.wireOp",EDGE,"E7.7.0.3"),sQuery(id+"F0.wireOp",EDGE,"E7.7.1.0"),sQuery(id+"F0.wireOp",EDGE,"E7.7.1.1"),sQuery(id+"F0.wireOp",EDGE,"E7.7.1.2"),sQuery(id+"F0.wireOp",EDGE,"E7.7.1.3"),sQuery(id+"F0.wireOp",EDGE,"E7.7.2.0"),sQuery(id+"F0.wireOp",EDGE,"E7.7.2.1"),sQuery(id+"F0.wireOp",EDGE,"E7.7.2.2"),sQuery(id+"F0.wireOp",EDGE,"E7.7.2.3"),sQuery(id+"F0.wireOp",EDGE,"E7.7.3.0"),sQuery(id+"F0.wireOp",EDGE,"E7.7.3.1"),sQuery(id+"F0.wireOp",EDGE,"E7.7.3.2"),sQuery(id+"F0.wireOp",EDGE,"E7.7.3.3"),sQuery(id+"F0.wireOp",EDGE,"E7.7.4.0"),sQuery(id+"F0.wireOp",EDGE,"E7.7.4.1"),sQuery(id+"F0.wireOp",EDGE,"E7.7.4.2"),sQuery(id+"F0.wireOp",EDGE,"E7.7.4.3"),sQuery(id+"F0.wireOp",EDGE,"E7.7.5.0"),sQuery(id+"F0.wireOp",EDGE,"E7.7.5.1"),sQuery(id+"F0.wireOp",EDGE,"E7.7.5.2"),sQuery(id+"F0.wireOp",EDGE,"E7.7.5.3"),sQuery(id+"F0.wireOp",EDGE,"E7.8.0.0"),sQuery(id+"F0.wireOp",EDGE,"E7.8.0.1"),sQuery(id+"F0.wireOp",EDGE,"E7.8.0.2"),sQuery(id+"F0.wireOp",EDGE,"E7.8.0.3"),sQuery(id+"F0.wireOp",EDGE,"E7.8.1.0"),sQuery(id+"F0.wireOp",EDGE,"E7.8.1.1"),sQuery(id+"F0.wireOp",EDGE,"E7.8.1.2"),sQuery(id+"F0.wireOp",EDGE,"E7.8.1.3"),sQuery(id+"F0.wireOp",EDGE,"E7.8.2.0"),sQuery(id+"F0.wireOp",EDGE,"E7.8.2.1"),sQuery(id+"F0.wireOp",EDGE,"E7.8.2.2"),sQuery(id+"F0.wireOp",EDGE,"E7.8.2.3"),sQuery(id+"F0.wireOp",EDGE,"E7.8.3.0"),sQuery(id+"F0.wireOp",EDGE,"E7.8.3.1"),sQuery(id+"F0.wireOp",EDGE,"E7.8.3.2"),sQuery(id+"F0.wireOp",EDGE,"E7.8.3.3"),sQuery(id+"F0.wireOp",EDGE,"E7.8.4.0"),sQuery(id+"F0.wireOp",EDGE,"E7.8.4.1"),sQuery(id+"F0.wireOp",EDGE,"E7.8.4.2"),sQuery(id+"F0.wireOp",EDGE,"E7.8.4.3"),sQuery(id+"F0.wireOp",EDGE,"E7.8.5.0"),sQuery(id+"F0.wireOp",EDGE,"E7.8.5.1"),sQuery(id+"F0.wireOp",EDGE,"E7.8.5.2"),sQuery(id+"F0.wireOp",EDGE,"E7.8.5.3"),sQuery(id+"F0.wireOp",EDGE,"E7.9.0.0"),sQuery(id+"F0.wireOp",EDGE,"E7.9.0.1"),sQuery(id+"F0.wireOp",EDGE,"E7.9.0.2"),sQuery(id+"F0.wireOp",EDGE,"E7.9.0.3"),sQuery(id+"F0.wireOp",EDGE,"E7.9.1.0"),sQuery(id+"F0.wireOp",EDGE,"E7.9.1.1"),sQuery(id+"F0.wireOp",EDGE,"E7.9.1.2"),sQuery(id+"F0.wireOp",EDGE,"E7.9.1.3"),sQuery(id+"F0.wireOp",EDGE,"E7.9.2.0"),sQuery(id+"F0.wireOp",EDGE,"E7.9.2.1"),sQuery(id+"F0.wireOp",EDGE,"E7.9.2.2"),sQuery(id+"F0.wireOp",EDGE,"E7.9.2.3"),sQuery(id+"F0.wireOp",EDGE,"E7.9.3.0"),sQuery(id+"F0.wireOp",EDGE,"E7.9.3.1"),sQuery(id+"F0.wireOp",EDGE,"E7.9.3.2"),sQuery(id+"F0.wireOp",EDGE,"E7.9.3.3"),sQuery(id+"F0.wireOp",EDGE,"E7.9.4.0"),sQuery(id+"F0.wireOp",EDGE,"E7.9.4.1"),sQuery(id+"F0.wireOp",EDGE,"E7.9.4.2"),sQuery(id+"F0.wireOp",EDGE,"E7.9.4.3"),sQuery(id+"F0.wireOp",EDGE,"E7.9.5.0"),sQuery(id+"F0.wireOp",EDGE,"E7.9.5.1"),sQuery(id+"F0.wireOp",EDGE,"E7.9.5.2"),sQuery(id+"F0.wireOp",EDGE,"E7.9.5.3"),sQuery(id+"F0.wireOp",EDGE,"E7.10.0.0"),sQuery(id+"F0.wireOp",EDGE,"E7.10.0.1"),sQuery(id+"F0.wireOp",EDGE,"E7.10.0.2"),sQuery(id+"F0.wireOp",EDGE,"E7.10.0.3"),sQuery(id+"F0.wireOp",EDGE,"E7.10.1.0"),sQuery(id+"F0.wireOp",EDGE,"E7.10.1.1"),sQuery(id+"F0.wireOp",EDGE,"E7.10.1.2"),sQuery(id+"F0.wireOp",EDGE,"E7.10.1.3"),sQuery(id+"F0.wireOp",EDGE,"E7.10.2.0"),sQuery(id+"F0.wireOp",EDGE,"E7.10.2.1"),sQuery(id+"F0.wireOp",EDGE,"E7.10.2.2"),sQuery(id+"F0.wireOp",EDGE,"E7.10.2.3"),sQuery(id+"F0.wireOp",EDGE,"E7.10.3.0"),sQuery(id+"F0.wireOp",EDGE,"E7.10.3.1"),sQuery(id+"F0.wireOp",EDGE,"E7.10.3.2"),sQuery(id+"F0.wireOp",EDGE,"E7.10.3.3"),sQuery(id+"F0.wireOp",EDGE,"E7.10.4.0"),sQuery(id+"F0.wireOp",EDGE,"E7.10.4.1"),sQuery(id+"F0.wireOp",EDGE,"E7.10.4.2"),sQuery(id+"F0.wireOp",EDGE,"E7.10.4.3"),sQuery(id+"F0.wireOp",EDGE,"E7.10.5.0"),sQuery(id+"F0.wireOp",EDGE,"E7.10.5.1"),sQuery(id+"F0.wireOp",EDGE,"E7.10.5.2"),sQuery(id+"F0.wireOp",EDGE,"E7.10.5.3"),sQuery(id+"F0.wireOp",EDGE,"E7.11.0.0"),sQuery(id+"F0.wireOp",EDGE,"E7.11.0.1"),sQuery(id+"F0.wireOp",EDGE,"E7.11.0.2"),sQuery(id+"F0.wireOp",EDGE,"E7.11.0.3"),sQuery(id+"F0.wireOp",EDGE,"E7.11.1.0"),sQuery(id+"F0.wireOp",EDGE,"E7.11.1.1"),sQuery(id+"F0.wireOp",EDGE,"E7.11.1.2"),sQuery(id+"F0.wireOp",EDGE,"E7.11.1.3"),sQuery(id+"F0.wireOp",EDGE,"E7.11.2.0"),sQuery(id+"F0.wireOp",EDGE,"E7.11.2.1"),sQuery(id+"F0.wireOp",EDGE,"E7.11.2.2"),sQuery(id+"F0.wireOp",EDGE,"E7.11.2.3"),sQuery(id+"F0.wireOp",EDGE,"E7.11.3.0"),sQuery(id+"F0.wireOp",EDGE,"E7.11.3.1"),sQuery(id+"F0.wireOp",EDGE,"E7.11.3.2"),sQuery(id+"F0.wireOp",EDGE,"E7.11.3.3"),sQuery(id+"F0.wireOp",EDGE,"E7.11.4.0"),sQuery(id+"F0.wireOp",EDGE,"E7.11.4.1"),sQuery(id+"F0.wireOp",EDGE,"E7.11.4.2"),sQuery(id+"F0.wireOp",EDGE,"E7.11.4.3"),sQuery(id+"F0.wireOp",EDGE,"E7.11.5.0"),sQuery(id+"F0.wireOp",EDGE,"E7.11.5.1"),sQuery(id+"F0.wireOp",EDGE,"E7.11.5.2"),sQuery(id+"F0.wireOp",EDGE,"E7.11.5.3")])],"isStart":false});
            var sketch = newSketch(context, id + "F6", { "sketchPlane" : qUnion([Q0])});
            skPoint(sketch, "E18.endSnap0", {"position": v(85.71, 128.74) * mm});
            skLineSegment(sketch, "E19", {"start": v(-88.79, 112.24) * mm, "end": v(-81.29, 112.24) * mm});
            skCircle(sketch, "E20", {"center": v(-85.04, 112.24) * mm, "radius": 2 * mm});
            skLineSegment(sketch, "E21", {"start": v(-1.79, 157.74) * mm, "end": v(-1.79, -82.26) * mm});
            skLineSegment(sketch, "E22", {"start": v(-86.79, 128.74) * mm, "end": v(-79.29, 128.74) * mm});
            skCircle(sketch, "E23", {"center": v(-83.04, 128.74) * mm, "radius": 2 * mm});
            skCircle(sketch, "E24.0.1.0", {"center": v(-83.04, 95.74) * mm, "radius": 2 * mm});
            skCircle(sketch, "E24.0.1.1", {"center": v(-85.04, 79.24) * mm, "radius": 2 * mm});
            skCircle(sketch, "E24.0.2.0", {"center": v(-83.04, 62.74) * mm, "radius": 2 * mm});
            skCircle(sketch, "E24.0.2.1", {"center": v(-85.04, 46.24) * mm, "radius": 2 * mm});
            skCircle(sketch, "E24.0.3.0", {"center": v(-83.04, 29.74) * mm, "radius": 2 * mm});
            skCircle(sketch, "E24.0.3.1", {"center": v(-85.04, 13.24) * mm, "radius": 2 * mm});
            skCircle(sketch, "E24.0.4.0", {"center": v(-83.04, -3.26) * mm, "radius": 2 * mm});
            skCircle(sketch, "E24.0.4.1", {"center": v(-85.04, -19.76) * mm, "radius": 2 * mm});
            skCircle(sketch, "E24.0.5.0", {"center": v(-83.04, -36.26) * mm, "radius": 2 * mm});
            skCircle(sketch, "E24.0.5.1", {"center": v(-85.04, -52.76) * mm, "radius": 2 * mm});
            skLineSegment(sketch, "E24.direction1", {"start": v(-83.04, 128.74) * mm, "end": v(-58.04, 128.74) * mm, "construction": true});
            skLineSegment(sketch, "E24.direction2", {"start": v(-83.04, 128.74) * mm, "end": v(-83.04, 95.74) * mm, "construction": true});
            skLineSegment(sketch, "E25", {"start": v(78.21, 128.74) * mm, "end": v(85.71, 128.74) * mm});
            skLineSegment(sketch, "E26", {"start": v(76.21, 112.24) * mm, "end": v(83.71, 112.24) * mm});
            skCircle(sketch, "E27", {"center": v(81.96, 128.74) * mm, "radius": 2 * mm});
            skCircle(sketch, "E28", {"center": v(79.96, 112.24) * mm, "radius": 2 * mm});
            skCircle(sketch, "E29.0.1.0", {"center": v(81.96, 95.74) * mm, "radius": 2 * mm});
            skCircle(sketch, "E29.0.1.1", {"center": v(79.96, 79.24) * mm, "radius": 2 * mm});
            skCircle(sketch, "E29.0.2.0", {"center": v(81.96, 62.74) * mm, "radius": 2 * mm});
            skCircle(sketch, "E29.0.2.1", {"center": v(79.96, 46.24) * mm, "radius": 2 * mm});
            skCircle(sketch, "E29.0.3.0", {"center": v(81.96, 29.74) * mm, "radius": 2 * mm});
            skCircle(sketch, "E29.0.3.1", {"center": v(79.96, 13.24) * mm, "radius": 2 * mm});
            skCircle(sketch, "E29.0.4.0", {"center": v(81.96, -3.26) * mm, "radius": 2 * mm});
            skCircle(sketch, "E29.0.4.1", {"center": v(79.96, -19.76) * mm, "radius": 2 * mm});
            skCircle(sketch, "E29.0.5.0", {"center": v(81.96, -36.26) * mm, "radius": 2 * mm});
            skCircle(sketch, "E29.0.5.1", {"center": v(79.96, -52.76) * mm, "radius": 2 * mm});
            skLineSegment(sketch, "E29.direction1", {"start": v(81.96, 128.74) * mm, "end": v(106.96, 128.74) * mm, "construction": true});
            skLineSegment(sketch, "E29.direction2", {"start": v(81.96, 128.74) * mm, "end": v(81.96, 95.74) * mm, "construction": true});
            skSolve(sketch);
        }
        {
            var Q0;
            Q0 = qSketchRegion(id + "F6", true);
            extrude(context, id + "F7", {"entities" : qUnion([Q0]), "operationType" : NewBodyOperationType.REMOVE, "endBound" : BoundingType.THROUGH_ALL, "oppositeDirection" : true, "depth" : 25 * mm});
        }
    });
